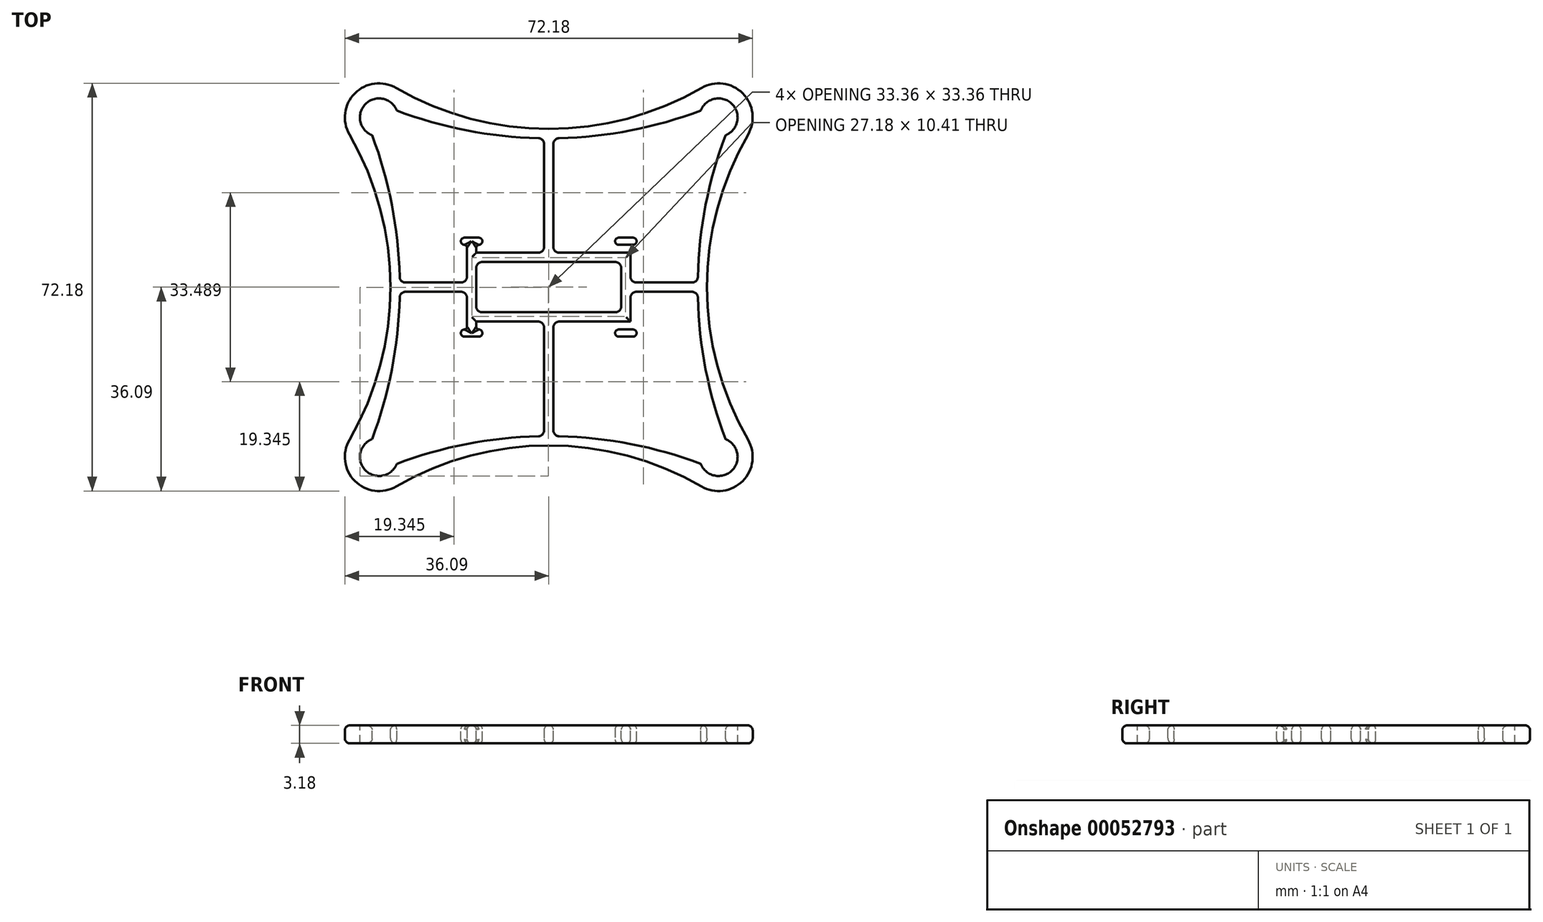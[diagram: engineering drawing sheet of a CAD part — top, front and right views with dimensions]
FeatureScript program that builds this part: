
annotation { "Feature Type Name" : "Feature", "Feature Type Description" : "" }
export const myFeature = defineFeature(function(context is Context, id is Id, definition is map)
    precondition{}
    {
        {
            var Q0;
            Q0=qCreatedBy(makeId("Top.planeOp"),FACE);
            var sketch = newSketch(context, id + "F0", { "sketchPlane" : qUnion([Q0])});
            skCircle(sketch, "E0", {"center": v(-30.05, 30.05) * mm, "radius": 3.38 * mm});
            skCircle(sketch, "E1", {"center": v(30.05, 30.05) * mm, "radius": 3.38 * mm});
            skCircle(sketch, "E2", {"center": v(30.05, -30.05) * mm, "radius": 3.38 * mm});
            skCircle(sketch, "E3", {"center": v(-30.05, -30.05) * mm, "radius": 3.38 * mm});
            skCircle(sketch, "E4", {"center": v(-30.05, 30.05) * mm, "radius": 6.05 * mm});
            skCircle(sketch, "E5", {"center": v(-30.05, -30.05) * mm, "radius": 6.05 * mm});
            skCircle(sketch, "E6", {"center": v(30.05, -30.05) * mm, "radius": 6.05 * mm});
            skCircle(sketch, "E7", {"center": v(30.05, 30.05) * mm, "radius": 6.05 * mm});
            skCircle(sketch, "E8", {"center": v(-102.57, 0) * mm, "radius": 76.2 * mm});
            skCircle(sketch, "E9", {"center": v(-81.9, 0) * mm, "radius": 53.88 * mm});
            skCircle(sketch, "E10", {"center": v(0, 102.57) * mm, "radius": 76.2 * mm});
            skCircle(sketch, "E11", {"center": v(0, 81.9) * mm, "radius": 53.88 * mm});
            skCircle(sketch, "E12", {"center": v(102.57, 0) * mm, "radius": 76.2 * mm});
            skCircle(sketch, "E13", {"center": v(81.9, 0) * mm, "radius": 53.88 * mm});
            skCircle(sketch, "E14", {"center": v(0, -102.57) * mm, "radius": 76.2 * mm});
            skCircle(sketch, "E15", {"center": v(0, -81.9) * mm, "radius": 53.88 * mm});
            skPoint(sketch, "E16.rect.middle", {"position": v(0, 0) * mm});
            skLineSegment(sketch, "E17.rect.bottom", {"start": v(14.48, 6.1) * mm, "end": v(-14.48, 6.1) * mm});
            skLineSegment(sketch, "E17.rect.top", {"start": v(14.48, -6.1) * mm, "end": v(-14.48, -6.1) * mm});
            skLineSegment(sketch, "E17.rect.left", {"start": v(14.48, 6.1) * mm, "end": v(14.48, -6.1) * mm});
            skLineSegment(sketch, "E17.rect.right", {"start": v(-14.48, 6.1) * mm, "end": v(-14.48, -6.1) * mm});
            skLineSegment(sketch, "E18.rect.bottom", {"start": v(12.83, 4.44) * mm, "end": v(-12.83, 4.45) * mm});
            skLineSegment(sketch, "E18.rect.top", {"start": v(12.83, -4.45) * mm, "end": v(-12.83, -4.44) * mm});
            skLineSegment(sketch, "E18.rect.left", {"start": v(12.83, 4.44) * mm, "end": v(12.83, -4.45) * mm});
            skLineSegment(sketch, "E18.rect.right", {"start": v(-12.83, 4.45) * mm, "end": v(-12.83, -4.44) * mm});
            skLineSegment(sketch, "E19.rect.bottom", {"start": v(0.83, 28.02) * mm, "end": v(-0.83, 28.02) * mm});
            skLineSegment(sketch, "E19.rect.top", {"start": v(0.83, -28.02) * mm, "end": v(-0.83, -28.02) * mm});
            skLineSegment(sketch, "E19.rect.left", {"start": v(0.83, 28.02) * mm, "end": v(0.83, -28.02) * mm});
            skLineSegment(sketch, "E19.rect.right", {"start": v(-0.83, 28.02) * mm, "end": v(-0.83, -28.02) * mm});
            skLineSegment(sketch, "E20.rect.bottom", {"start": v(28.02, 0.83) * mm, "end": v(-28.02, 0.83) * mm});
            skLineSegment(sketch, "E20.rect.top", {"start": v(28.02, -0.83) * mm, "end": v(-28.02, -0.83) * mm});
            skLineSegment(sketch, "E20.rect.left", {"start": v(28.02, 0.83) * mm, "end": v(28.02, -0.83) * mm});
            skLineSegment(sketch, "E20.rect.right", {"start": v(-28.02, 0.83) * mm, "end": v(-28.02, -0.83) * mm});
            skLineSegment(sketch, "E21.left", {"start": v(14.48, 6.1) * mm, "end": v(14.48, 6.1) * mm});
            skLineSegment(sketch, "E22.left", {"start": v(14.48, -6.1) * mm, "end": v(14.48, -6.1) * mm});
            skLineSegment(sketch, "E23.bottom", {"start": v(-14.48, 6.1) * mm, "end": v(-12.83, 6.1) * mm});
            skLineSegment(sketch, "E23.top", {"start": v(-14.48, 8.13) * mm, "end": v(-12.83, 8.13) * mm});
            skLineSegment(sketch, "E23.left", {"start": v(-14.48, 6.1) * mm, "end": v(-14.48, 8.13) * mm});
            skLineSegment(sketch, "E23.right", {"start": v(-12.83, 6.1) * mm, "end": v(-12.83, 8.13) * mm});
            skLineSegment(sketch, "E24.bottom", {"start": v(-14.48, -6.1) * mm, "end": v(-12.83, -6.1) * mm});
            skLineSegment(sketch, "E24.top", {"start": v(-14.48, -8.13) * mm, "end": v(-12.83, -8.13) * mm});
            skLineSegment(sketch, "E24.left", {"start": v(-14.48, -6.1) * mm, "end": v(-14.48, -8.13) * mm});
            skLineSegment(sketch, "E24.right", {"start": v(-12.83, -6.1) * mm, "end": v(-12.83, -8.13) * mm});
            skLineSegment(sketch, "E25.bottom", {"start": v(14.48, -6.1) * mm, "end": v(12.83, -6.1) * mm});
            skLineSegment(sketch, "E25.top", {"start": v(14.48, -8.13) * mm, "end": v(12.83, -8.13) * mm});
            skLineSegment(sketch, "E25.left", {"start": v(14.48, -6.1) * mm, "end": v(14.48, -8.13) * mm});
            skLineSegment(sketch, "E25.right", {"start": v(12.83, -6.1) * mm, "end": v(12.83, -8.13) * mm});
            skLineSegment(sketch, "E26.bottom", {"start": v(14.48, 6.1) * mm, "end": v(12.83, 6.1) * mm});
            skLineSegment(sketch, "E26.top", {"start": v(14.48, 8.13) * mm, "end": v(12.83, 8.13) * mm});
            skLineSegment(sketch, "E26.left", {"start": v(14.48, 6.1) * mm, "end": v(14.48, 8.13) * mm});
            skLineSegment(sketch, "E26.right", {"start": v(12.83, 6.1) * mm, "end": v(12.83, 8.13) * mm});
            skLineSegment(sketch, "E27.rect.bottom", {"start": v(-11.75, 8.76) * mm, "end": v(-15.56, 8.76) * mm});
            skLineSegment(sketch, "E27.rect.top", {"start": v(-11.75, 7.5) * mm, "end": v(-15.56, 7.5) * mm});
            skLineSegment(sketch, "E27.rect.left", {"start": v(-11.75, 8.76) * mm, "end": v(-11.75, 7.5) * mm});
            skLineSegment(sketch, "E27.rect.right", {"start": v(-15.56, 8.76) * mm, "end": v(-15.56, 7.5) * mm});
            skPoint(sketch, "E27.rect.middle", {"position": v(-13.65, 8.13) * mm});
            skLineSegment(sketch, "E28.rect.bottom", {"start": v(11.75, 8.76) * mm, "end": v(15.56, 8.76) * mm});
            skLineSegment(sketch, "E28.rect.top", {"start": v(11.75, 7.5) * mm, "end": v(15.56, 7.5) * mm});
            skLineSegment(sketch, "E28.rect.left", {"start": v(11.75, 8.76) * mm, "end": v(11.75, 7.5) * mm});
            skLineSegment(sketch, "E28.rect.right", {"start": v(15.56, 8.76) * mm, "end": v(15.56, 7.5) * mm});
            skPoint(sketch, "E28.rect.middle", {"position": v(13.65, 8.13) * mm});
            skLineSegment(sketch, "E29.rect.bottom", {"start": v(11.75, -7.5) * mm, "end": v(15.56, -7.5) * mm});
            skLineSegment(sketch, "E29.rect.top", {"start": v(11.75, -8.76) * mm, "end": v(15.56, -8.76) * mm});
            skLineSegment(sketch, "E29.rect.left", {"start": v(11.75, -7.5) * mm, "end": v(11.75, -8.76) * mm});
            skLineSegment(sketch, "E29.rect.right", {"start": v(15.56, -7.5) * mm, "end": v(15.56, -8.76) * mm});
            skPoint(sketch, "E29.rect.middle", {"position": v(13.65, -8.13) * mm});
            skLineSegment(sketch, "E30.rect.bottom", {"start": v(-11.75, -8.76) * mm, "end": v(-15.56, -8.76) * mm});
            skLineSegment(sketch, "E30.rect.top", {"start": v(-11.75, -7.5) * mm, "end": v(-15.56, -7.5) * mm});
            skLineSegment(sketch, "E30.rect.left", {"start": v(-11.75, -8.76) * mm, "end": v(-11.75, -7.5) * mm});
            skLineSegment(sketch, "E30.rect.right", {"start": v(-15.56, -8.76) * mm, "end": v(-15.56, -7.5) * mm});
            skPoint(sketch, "E30.rect.middle", {"position": v(-13.65, -8.13) * mm});
            skSolve(sketch);
        }
        {
            var Q0;
            {var subQ3=sQuery(id+"F0.wireOp",EDGE,"E4");var subQ5=sQuery(id+"F0.wireOp",EDGE,"E9");var subQ7=makeQuery(id+"F0.imprint","INTERSECT",VERTEX,{"derivedFrom":[subQ3,subQ5]});Q0=makeQuery(id+"F0.imprint","IMPRINT",FACE,{"disambiguationData":[TD([[makeQuery(id+"F0.imprint","IMPRINT",EDGE,{"disambiguationData":[TD([[subQ7,-1.0]])],"derivedFrom":subQ3}),-1.0]])]});}
            var Q1;
            {var subQ0=sQuery(id+"F0.wireOp",EDGE,"E8");var subQ1=sQuery(id+"F0.wireOp",EDGE,"E0");var subQ2=makeQuery(id+"F0.imprint","INTERSECT",VERTEX,{"disambiguationData":[OD(0.0)],"derivedFrom":[subQ1,subQ0]});Q1=makeQuery(id+"F0.imprint","IMPRINT",FACE,{"disambiguationData":[TD([[makeQuery(id+"F0.imprint","IMPRINT",EDGE,{"disambiguationData":[TD([[subQ2,-1.0]])],"derivedFrom":subQ1}),-1.0]])]});}
            var Q2;
            {var subQ0=sQuery(id+"F0.wireOp",EDGE,"E10");var subQ1=sQuery(id+"F0.wireOp",EDGE,"E0");var subQ2=makeQuery(id+"F0.imprint","INTERSECT",VERTEX,{"disambiguationData":[OD(0.0)],"derivedFrom":[subQ1,subQ0]});Q2=makeQuery(id+"F0.imprint","IMPRINT",FACE,{"disambiguationData":[TD([[makeQuery(id+"F0.imprint","IMPRINT",EDGE,{"disambiguationData":[TD([[subQ2,-1.0]])],"derivedFrom":subQ1}),-1.0]])]});}
            var Q3;
            {var subQ0=sQuery(id+"F0.wireOp",EDGE,"E0");var subQ1=sQuery(id+"F0.wireOp",EDGE,"E10");var subQ3=makeQuery(id+"F0.imprint","INTERSECT",VERTEX,{"disambiguationData":[OD(0.0)],"derivedFrom":[subQ0,subQ1]});Q3=makeQuery(id+"F0.imprint","IMPRINT",FACE,{"disambiguationData":[TD([[makeQuery(id+"F0.imprint","IMPRINT",EDGE,{"disambiguationData":[TD([[subQ3,1.0]])],"derivedFrom":subQ0}),-1.0]])]});}
            var Q4;
            {var subQ0=sQuery(id+"F0.wireOp",EDGE,"E11");var subQ3=sQuery(id+"F0.wireOp",EDGE,"E4");var subQ4=makeQuery(id+"F0.imprint","INTERSECT",VERTEX,{"derivedFrom":[subQ3,subQ0]});Q4=makeQuery(id+"F0.imprint","IMPRINT",FACE,{"disambiguationData":[TD([[makeQuery(id+"F0.imprint","IMPRINT",EDGE,{"disambiguationData":[TD([[subQ4,1.0]])],"derivedFrom":subQ3}),-1.0]])]});}
            var Q5;
            {var subQ0=sQuery(id+"F0.wireOp",EDGE,"E10");var subQ1=sQuery(id+"F0.wireOp",EDGE,"E1");var subQ5=makeQuery(id+"F0.imprint","INTERSECT",VERTEX,{"disambiguationData":[OD(0.0)],"derivedFrom":[subQ1,subQ0]});Q5=makeQuery(id+"F0.imprint","IMPRINT",FACE,{"disambiguationData":[TD([[makeQuery(id+"F0.imprint","IMPRINT",EDGE,{"disambiguationData":[TD([[subQ5,1.0]])],"derivedFrom":subQ1}),-1.0]])]});}
            var Q6;
            {var subQ1=sQuery(id+"F0.wireOp",EDGE,"E1");var subQ5=sQuery(id+"F0.wireOp",EDGE,"E10");var subQ6=makeQuery(id+"F0.imprint","INTERSECT",VERTEX,{"disambiguationData":[OD(1.0)],"derivedFrom":[subQ1,subQ5]});Q6=makeQuery(id+"F0.imprint","IMPRINT",FACE,{"disambiguationData":[TD([[makeQuery(id+"F0.imprint","IMPRINT",EDGE,{"disambiguationData":[TD([[subQ6,1.0]])],"derivedFrom":subQ1}),-1.0]])]});}
            var Q7;
            {var subQ0=sQuery(id+"F0.wireOp",EDGE,"E12");var subQ3=sQuery(id+"F0.wireOp",EDGE,"E1");var subQ4=makeQuery(id+"F0.imprint","INTERSECT",VERTEX,{"disambiguationData":[OD(0.0)],"derivedFrom":[subQ3,subQ0]});Q7=makeQuery(id+"F0.imprint","IMPRINT",FACE,{"disambiguationData":[TD([[makeQuery(id+"F0.imprint","IMPRINT",EDGE,{"disambiguationData":[TD([[subQ4,-1.0]])],"derivedFrom":subQ3}),-1.0]])]});}
            var Q8;
            {var subQ0=sQuery(id+"F0.wireOp",EDGE,"E12");var subQ1=sQuery(id+"F0.wireOp",EDGE,"E2");var subQ5=makeQuery(id+"F0.imprint","INTERSECT",VERTEX,{"disambiguationData":[OD(0.0)],"derivedFrom":[subQ1,subQ0]});Q8=makeQuery(id+"F0.imprint","IMPRINT",FACE,{"disambiguationData":[TD([[makeQuery(id+"F0.imprint","IMPRINT",EDGE,{"disambiguationData":[TD([[subQ5,1.0]])],"derivedFrom":subQ1}),-1.0]])]});}
            var Q9;
            {var subQ0=sQuery(id+"F0.wireOp",EDGE,"E12");var subQ1=sQuery(id+"F0.wireOp",EDGE,"E2");var subQ2=makeQuery(id+"F0.imprint","INTERSECT",VERTEX,{"disambiguationData":[OD(1.0)],"derivedFrom":[subQ1,subQ0]});Q9=makeQuery(id+"F0.imprint","IMPRINT",FACE,{"disambiguationData":[TD([[makeQuery(id+"F0.imprint","IMPRINT",EDGE,{"disambiguationData":[TD([[subQ2,1.0]])],"derivedFrom":subQ1}),-1.0]])]});}
            var Q10;
            {var subQ0=sQuery(id+"F0.wireOp",EDGE,"E14");var subQ3=sQuery(id+"F0.wireOp",EDGE,"E2");var subQ4=makeQuery(id+"F0.imprint","INTERSECT",VERTEX,{"disambiguationData":[OD(0.0)],"derivedFrom":[subQ3,subQ0]});Q10=makeQuery(id+"F0.imprint","IMPRINT",FACE,{"disambiguationData":[TD([[makeQuery(id+"F0.imprint","IMPRINT",EDGE,{"disambiguationData":[TD([[subQ4,-1.0]])],"derivedFrom":subQ3}),-1.0]])]});}
            var Q11;
            {var subQ0=sQuery(id+"F0.wireOp",EDGE,"E3");var subQ1=sQuery(id+"F0.wireOp",EDGE,"E14");var subQ3=makeQuery(id+"F0.imprint","INTERSECT",VERTEX,{"disambiguationData":[OD(0.0)],"derivedFrom":[subQ0,subQ1]});Q11=makeQuery(id+"F0.imprint","IMPRINT",FACE,{"disambiguationData":[TD([[makeQuery(id+"F0.imprint","IMPRINT",EDGE,{"disambiguationData":[TD([[subQ3,-1.0]])],"derivedFrom":subQ0}),-1.0]])]});}
            var Q12;
            {var subQ1=sQuery(id+"F0.wireOp",EDGE,"E3");var subQ5=sQuery(id+"F0.wireOp",EDGE,"E8");var subQ7=makeQuery(id+"F0.imprint","INTERSECT",VERTEX,{"disambiguationData":[OD(0.0)],"derivedFrom":[subQ1,subQ5]});Q12=makeQuery(id+"F0.imprint","IMPRINT",FACE,{"disambiguationData":[TD([[makeQuery(id+"F0.imprint","IMPRINT",EDGE,{"disambiguationData":[TD([[subQ7,-1.0]])],"derivedFrom":subQ1}),-1.0]])]});}
            var Q13;
            {var subQ0=sQuery(id+"F0.wireOp",EDGE,"E8");var subQ3=sQuery(id+"F0.wireOp",EDGE,"E3");var subQ5=makeQuery(id+"F0.imprint","INTERSECT",VERTEX,{"disambiguationData":[OD(0.0)],"derivedFrom":[subQ3,subQ0]});Q13=makeQuery(id+"F0.imprint","IMPRINT",FACE,{"disambiguationData":[TD([[makeQuery(id+"F0.imprint","IMPRINT",EDGE,{"disambiguationData":[TD([[subQ5,1.0]])],"derivedFrom":subQ3}),-1.0]])]});}
            var Q14;
            {var subQ0=sQuery(id+"F0.wireOp",EDGE,"E12");var subQ3=sQuery(id+"F0.wireOp",EDGE,"E1");var subQ6=makeQuery(id+"F0.imprint","INTERSECT",VERTEX,{"disambiguationData":[OD(0.0)],"derivedFrom":[subQ3,subQ0]});Q14=makeQuery(id+"F0.imprint","IMPRINT",FACE,{"disambiguationData":[TD([[makeQuery(id+"F0.imprint","IMPRINT",EDGE,{"disambiguationData":[TD([[subQ6,1.0]])],"derivedFrom":subQ3}),-1.0]])]});}
            var Q15;
            {var subQ3=sQuery(id+"F0.wireOp",EDGE,"E6");var subQ5=sQuery(id+"F0.wireOp",EDGE,"E12");var subQ7=makeQuery(id+"F0.imprint","INTERSECT",VERTEX,{"disambiguationData":[OD(0.0)],"derivedFrom":[subQ3,subQ5]});Q15=makeQuery(id+"F0.imprint","IMPRINT",FACE,{"disambiguationData":[TD([[makeQuery(id+"F0.imprint","IMPRINT",EDGE,{"disambiguationData":[TD([[subQ7,1.0]])],"derivedFrom":subQ3}),-1.0]])]});}
            var Q16;
            {var subQ0=sQuery(id+"F0.wireOp",EDGE,"97792d4c-2e40-4aaa-a942-c1651c489ece.rect.left");var subQ6=sQuery(id+"F0.wireOp",EDGE,"E17.rect.bottom");var subQ7=makeQuery(id+"F0.imprint","INTERSECT",VERTEX,{"derivedFrom":[subQ0,subQ6]});Q16=makeQuery(id+"F0.imprint","IMPRINT",FACE,{"disambiguationData":[TD([[makeQuery(id+"F0.imprint","IMPRINT",EDGE,{"disambiguationData":[TD([[subQ7,-1.0]])],"derivedFrom":subQ6}),-1.0]])]});}
            var Q17;
            {var subQ3=sQuery(id+"F0.wireOp",EDGE,"E16.rect.bottom");var subQ9=sQuery(id+"F0.wireOp",EDGE,"E18.rect.right");var subQ11=makeQuery(id+"F0.imprint","INTERSECT",VERTEX,{"derivedFrom":[subQ3,subQ9]});Q17=makeQuery(id+"F0.imprint","IMPRINT",FACE,{"disambiguationData":[TD([[makeQuery(id+"F0.imprint","IMPRINT",EDGE,{"disambiguationData":[TD([[subQ11,-1.0]])],"derivedFrom":subQ3}),-1.0]])]});}
            var Q18;
            {var subQ0=sQuery(id+"F0.wireOp",EDGE,"E17.rect.bottom");var subQ1=sQuery(id+"F0.wireOp",EDGE,"97792d4c-2e40-4aaa-a942-c1651c489ece.rect.left");var subQ2=makeQuery(id+"F0.imprint","INTERSECT",VERTEX,{"derivedFrom":[subQ1,subQ0]});Q18=makeQuery(id+"F0.imprint","IMPRINT",FACE,{"disambiguationData":[TD([[makeQuery(id+"F0.imprint","IMPRINT",EDGE,{"disambiguationData":[TD([[subQ2,-1.0]])],"derivedFrom":subQ1}),-1.0]])]});}
            var Q19;
            {var subQ0=sQuery(id+"F0.wireOp",EDGE,"E17.rect.left");var subQ3=sQuery(id+"F0.wireOp",EDGE,"E16.rect.bottom");var subQ4=makeQuery(id+"F0.imprint","INTERSECT",VERTEX,{"derivedFrom":[subQ3,subQ0]});Q19=makeQuery(id+"F0.imprint","IMPRINT",FACE,{"disambiguationData":[TD([[makeQuery(id+"F0.imprint","IMPRINT",EDGE,{"disambiguationData":[TD([[subQ4,-1.0]])],"derivedFrom":subQ3}),-1.0]])]});}
            var Q20;
            {var subQ0=sQuery(id+"F0.wireOp",EDGE,"E17.rect.left");var subQ1=sQuery(id+"F0.wireOp",EDGE,"E16.rect.bottom");var subQ2=makeQuery(id+"F0.imprint","INTERSECT",VERTEX,{"derivedFrom":[subQ1,subQ0]});Q20=makeQuery(id+"F0.imprint","IMPRINT",FACE,{"disambiguationData":[TD([[makeQuery(id+"F0.imprint","IMPRINT",EDGE,{"disambiguationData":[TD([[subQ2,-1.0]])],"derivedFrom":subQ1}),1.0]])]});}
            var Q21;
            {var subQ0=sQuery(id+"F0.wireOp",EDGE,"E17.rect.left");var subQ3=sQuery(id+"F0.wireOp",EDGE,"E16.rect.top");var subQ4=makeQuery(id+"F0.imprint","INTERSECT",VERTEX,{"derivedFrom":[subQ3,subQ0]});Q21=makeQuery(id+"F0.imprint","IMPRINT",FACE,{"disambiguationData":[TD([[makeQuery(id+"F0.imprint","IMPRINT",EDGE,{"disambiguationData":[TD([[subQ4,-1.0]])],"derivedFrom":subQ3}),1.0]])]});}
            var Q22;
            {var subQ0=sQuery(id+"F0.wireOp",EDGE,"E18.rect.top");var subQ1=sQuery(id+"F0.wireOp",EDGE,"97792d4c-2e40-4aaa-a942-c1651c489ece.rect.left");var subQ2=makeQuery(id+"F0.imprint","INTERSECT",VERTEX,{"derivedFrom":[subQ1,subQ0]});Q22=makeQuery(id+"F0.imprint","IMPRINT",FACE,{"disambiguationData":[TD([[makeQuery(id+"F0.imprint","IMPRINT",EDGE,{"disambiguationData":[TD([[subQ2,-1.0]])],"derivedFrom":subQ1}),-1.0]])]});}
            var Q23;
            {var subQ5=sQuery(id+"F0.wireOp",EDGE,"E16.rect.top");var subQ9=sQuery(id+"F0.wireOp",EDGE,"E18.rect.right");var subQ11=makeQuery(id+"F0.imprint","INTERSECT",VERTEX,{"derivedFrom":[subQ5,subQ9]});Q23=makeQuery(id+"F0.imprint","IMPRINT",FACE,{"disambiguationData":[TD([[makeQuery(id+"F0.imprint","IMPRINT",EDGE,{"disambiguationData":[TD([[subQ11,-1.0]])],"derivedFrom":subQ5}),1.0]])]});}
            var Q24;
            {var subQ0=sQuery(id+"F0.wireOp",EDGE,"E18.rect.right");var subQ1=sQuery(id+"F0.wireOp",EDGE,"E16.rect.bottom");var subQ2=makeQuery(id+"F0.imprint","INTERSECT",VERTEX,{"derivedFrom":[subQ1,subQ0]});Q24=makeQuery(id+"F0.imprint","IMPRINT",FACE,{"disambiguationData":[TD([[makeQuery(id+"F0.imprint","IMPRINT",EDGE,{"disambiguationData":[TD([[subQ2,-1.0]])],"derivedFrom":subQ1}),1.0]])]});}
            var Q25;
            {var subQ1=sQuery(id+"F0.wireOp",EDGE,"E16.rect.bottom");var subQ6=sQuery(id+"F0.wireOp",EDGE,"E17.rect.right");var subQ7=makeQuery(id+"F0.imprint","INTERSECT",VERTEX,{"derivedFrom":[subQ1,subQ6]});Q25=makeQuery(id+"F0.imprint","IMPRINT",FACE,{"disambiguationData":[TD([[makeQuery(id+"F0.imprint","IMPRINT",EDGE,{"disambiguationData":[TD([[subQ7,-1.0]])],"derivedFrom":subQ6}),-1.0]])]});}
            var Q26;
            {var subQ1=sQuery(id+"F0.wireOp",EDGE,"E16.rect.bottom");var subQ6=sQuery(id+"F0.wireOp",EDGE,"E17.rect.left");var subQ7=makeQuery(id+"F0.imprint","INTERSECT",VERTEX,{"derivedFrom":[subQ1,subQ6]});Q26=makeQuery(id+"F0.imprint","IMPRINT",FACE,{"disambiguationData":[TD([[makeQuery(id+"F0.imprint","IMPRINT",EDGE,{"disambiguationData":[TD([[subQ7,-1.0]])],"derivedFrom":subQ6}),1.0]])]});}
            var Q27;
            {var subQ0=sQuery(id+"F0.wireOp",EDGE,"97792d4c-2e40-4aaa-a942-c1651c489ece.rect.left");var subQ6=sQuery(id+"F0.wireOp",EDGE,"E17.rect.top");var subQ7=makeQuery(id+"F0.imprint","INTERSECT",VERTEX,{"derivedFrom":[subQ0,subQ6]});Q27=makeQuery(id+"F0.imprint","IMPRINT",FACE,{"disambiguationData":[TD([[makeQuery(id+"F0.imprint","IMPRINT",EDGE,{"disambiguationData":[TD([[subQ7,-1.0]])],"derivedFrom":subQ6}),1.0]])]});}
            var Q28;
            Q28=makeQuery(id+"F0.imprint","IMPRINT",FACE,{"disambiguationData":[TD([[makeQuery(id+"F0.imprint","IMPRINT",EDGE,{"derivedFrom":sQuery(id+"F0.wireOp",EDGE,"de616939-67df-4de1-98a8-b123298b16c6.bottom")}),-1.0]])]});
            var Q29;
            Q29=makeQuery(id+"F0.imprint","IMPRINT",FACE,{"disambiguationData":[TD([[makeQuery(id+"F0.imprint","IMPRINT",EDGE,{"derivedFrom":sQuery(id+"F0.wireOp",EDGE,"6e18662c-c205-4df8-b961-8c52012f615d.bottom")}),1.0]])]});
            var Q30;
            Q30=makeQuery(id+"F0.imprint","IMPRINT",FACE,{"disambiguationData":[TD([[makeQuery(id+"F0.imprint","IMPRINT",EDGE,{"derivedFrom":sQuery(id+"F0.wireOp",EDGE,"e5e8593a-10a3-4d83-983c-bc6820abb37f.bottom")}),-1.0]])]});
            var Q31;
            Q31=makeQuery(id+"F0.imprint","IMPRINT",FACE,{"disambiguationData":[TD([[makeQuery(id+"F0.imprint","IMPRINT",EDGE,{"derivedFrom":sQuery(id+"F0.wireOp",EDGE,"fe4e9a62-022c-4ccf-87c7-29a0906fb106.bottom")}),1.0]])]});
            var Q32;
            {var subQ0=sQuery(id+"F0.wireOp",EDGE,"E20.rect.bottom");var subQ1=sQuery(id+"F0.wireOp",EDGE,"E8");var subQ2=makeQuery(id+"F0.imprint","INTERSECT",VERTEX,{"derivedFrom":[subQ1,subQ0]});Q32=makeQuery(id+"F0.imprint","IMPRINT",FACE,{"disambiguationData":[TD([[makeQuery(id+"F0.imprint","IMPRINT",EDGE,{"disambiguationData":[TD([[subQ2,1.0]])],"derivedFrom":subQ1}),1.0]])]});}
            var Q33;
            {var subQ0=sQuery(id+"F0.wireOp",EDGE,"E8");var subQ1=sQuery(id+"F0.wireOp",EDGE,"E5");var subQ2=makeQuery(id+"F0.imprint","INTERSECT",VERTEX,{"disambiguationData":[OD(0.0)],"derivedFrom":[subQ1,subQ0]});Q33=makeQuery(id+"F0.imprint","IMPRINT",FACE,{"disambiguationData":[TD([[makeQuery(id+"F0.imprint","IMPRINT",EDGE,{"disambiguationData":[TD([[subQ2,-1.0]])],"derivedFrom":subQ1}),-1.0]])]});}
            var Q34;
            {var subQ0=sQuery(id+"F0.wireOp",EDGE,"E19.rect.left");var subQ1=sQuery(id+"F0.wireOp",EDGE,"E14");var subQ2=makeQuery(id+"F0.imprint","INTERSECT",VERTEX,{"derivedFrom":[subQ1,subQ0]});Q34=makeQuery(id+"F0.imprint","IMPRINT",FACE,{"disambiguationData":[TD([[makeQuery(id+"F0.imprint","IMPRINT",EDGE,{"disambiguationData":[TD([[subQ2,-1.0]])],"derivedFrom":subQ1}),1.0]])]});}
            var Q35;
            {var subQ0=sQuery(id+"F0.wireOp",EDGE,"E14");var subQ1=sQuery(id+"F0.wireOp",EDGE,"E6");var subQ2=makeQuery(id+"F0.imprint","INTERSECT",VERTEX,{"disambiguationData":[OD(0.0)],"derivedFrom":[subQ1,subQ0]});Q35=makeQuery(id+"F0.imprint","IMPRINT",FACE,{"disambiguationData":[TD([[makeQuery(id+"F0.imprint","IMPRINT",EDGE,{"disambiguationData":[TD([[subQ2,-1.0]])],"derivedFrom":subQ1}),-1.0]])]});}
            var Q36;
            {var subQ0=sQuery(id+"F0.wireOp",EDGE,"E20.rect.bottom");var subQ1=sQuery(id+"F0.wireOp",EDGE,"E12");var subQ2=makeQuery(id+"F0.imprint","INTERSECT",VERTEX,{"derivedFrom":[subQ1,subQ0]});Q36=makeQuery(id+"F0.imprint","IMPRINT",FACE,{"disambiguationData":[TD([[makeQuery(id+"F0.imprint","IMPRINT",EDGE,{"disambiguationData":[TD([[subQ2,-1.0]])],"derivedFrom":subQ1}),1.0]])]});}
            var Q37;
            {var subQ7=sQuery(id+"F0.wireOp",EDGE,"E17.rect.left");var subQ8=sQuery(id+"F0.wireOp",EDGE,"E17.rect.top");var subQ9=makeQuery(id+"F0.imprint","INTERSECT",VERTEX,{"derivedFrom":[subQ8,subQ7]});Q37=makeQuery(id+"F0.imprint","IMPRINT",FACE,{"disambiguationData":[TD([[makeQuery(id+"F0.imprint","IMPRINT",EDGE,{"disambiguationData":[TD([[subQ9,-1.0]])],"derivedFrom":subQ8}),-1.0]])]});}
            var Q38;
            {var subQ0=sQuery(id+"F0.wireOp",EDGE,"E19.rect.left");var subQ1=sQuery(id+"F0.wireOp",EDGE,"E17.rect.top");var subQ2=makeQuery(id+"F0.imprint","INTERSECT",VERTEX,{"derivedFrom":[subQ1,subQ0]});Q38=makeQuery(id+"F0.imprint","IMPRINT",FACE,{"disambiguationData":[TD([[makeQuery(id+"F0.imprint","IMPRINT",EDGE,{"disambiguationData":[TD([[subQ2,-1.0]])],"derivedFrom":subQ1}),-1.0]])]});}
            var Q39;
            {var subQ5=sQuery(id+"F0.wireOp",EDGE,"E17.rect.top");var subQ7=sQuery(id+"F0.wireOp",EDGE,"E17.rect.right");var subQ8=makeQuery(id+"F0.imprint","INTERSECT",VERTEX,{"derivedFrom":[subQ5,subQ7]});Q39=makeQuery(id+"F0.imprint","IMPRINT",FACE,{"disambiguationData":[TD([[makeQuery(id+"F0.imprint","IMPRINT",EDGE,{"disambiguationData":[TD([[subQ8,1.0]])],"derivedFrom":subQ5}),-1.0]])]});}
            var Q40;
            {var subQ0=sQuery(id+"F0.wireOp",EDGE,"E20.rect.bottom");var subQ1=sQuery(id+"F0.wireOp",EDGE,"E17.rect.right");var subQ2=makeQuery(id+"F0.imprint","INTERSECT",VERTEX,{"derivedFrom":[subQ1,subQ0]});Q40=makeQuery(id+"F0.imprint","IMPRINT",FACE,{"disambiguationData":[TD([[makeQuery(id+"F0.imprint","IMPRINT",EDGE,{"disambiguationData":[TD([[subQ2,-1.0]])],"derivedFrom":subQ1}),1.0]])]});}
            var Q41;
            {var subQ7=sQuery(id+"F0.wireOp",EDGE,"E17.rect.right");var subQ8=sQuery(id+"F0.wireOp",EDGE,"E17.rect.bottom");var subQ9=makeQuery(id+"F0.imprint","INTERSECT",VERTEX,{"derivedFrom":[subQ8,subQ7]});Q41=makeQuery(id+"F0.imprint","IMPRINT",FACE,{"disambiguationData":[TD([[makeQuery(id+"F0.imprint","IMPRINT",EDGE,{"disambiguationData":[TD([[subQ9,1.0]])],"derivedFrom":subQ8}),1.0]])]});}
            var Q42;
            {var subQ7=sQuery(id+"F0.wireOp",EDGE,"E17.rect.left");var subQ8=sQuery(id+"F0.wireOp",EDGE,"E17.rect.bottom");var subQ9=makeQuery(id+"F0.imprint","INTERSECT",VERTEX,{"derivedFrom":[subQ8,subQ7]});Q42=makeQuery(id+"F0.imprint","IMPRINT",FACE,{"disambiguationData":[TD([[makeQuery(id+"F0.imprint","IMPRINT",EDGE,{"disambiguationData":[TD([[subQ9,-1.0]])],"derivedFrom":subQ8}),1.0]])]});}
            var Q43;
            {var subQ0=sQuery(id+"F0.wireOp",EDGE,"E20.rect.bottom");var subQ1=sQuery(id+"F0.wireOp",EDGE,"E17.rect.left");var subQ2=makeQuery(id+"F0.imprint","INTERSECT",VERTEX,{"derivedFrom":[subQ1,subQ0]});Q43=makeQuery(id+"F0.imprint","IMPRINT",FACE,{"disambiguationData":[TD([[makeQuery(id+"F0.imprint","IMPRINT",EDGE,{"disambiguationData":[TD([[subQ2,-1.0]])],"derivedFrom":subQ1}),-1.0]])]});}
            var Q44;
            {var subQ0=sQuery(id+"F0.wireOp",EDGE,"E12");var subQ1=sQuery(id+"F0.wireOp",EDGE,"E7");var subQ2=makeQuery(id+"F0.imprint","INTERSECT",VERTEX,{"disambiguationData":[OD(1.0)],"derivedFrom":[subQ1,subQ0]});Q44=makeQuery(id+"F0.imprint","IMPRINT",FACE,{"disambiguationData":[TD([[makeQuery(id+"F0.imprint","IMPRINT",EDGE,{"disambiguationData":[TD([[subQ2,-1.0]])],"derivedFrom":subQ1}),-1.0]])]});}
            var Q45;
            {var subQ0=sQuery(id+"F0.wireOp",EDGE,"E19.rect.left");var subQ1=sQuery(id+"F0.wireOp",EDGE,"E17.rect.bottom");var subQ2=makeQuery(id+"F0.imprint","INTERSECT",VERTEX,{"derivedFrom":[subQ1,subQ0]});Q45=makeQuery(id+"F0.imprint","IMPRINT",FACE,{"disambiguationData":[TD([[makeQuery(id+"F0.imprint","IMPRINT",EDGE,{"disambiguationData":[TD([[subQ2,-1.0]])],"derivedFrom":subQ1}),1.0]])]});}
            var Q46;
            {var subQ0=sQuery(id+"F0.wireOp",EDGE,"E19.rect.right");var subQ1=sQuery(id+"F0.wireOp",EDGE,"E10");var subQ2=makeQuery(id+"F0.imprint","INTERSECT",VERTEX,{"derivedFrom":[subQ1,subQ0]});Q46=makeQuery(id+"F0.imprint","IMPRINT",FACE,{"disambiguationData":[TD([[makeQuery(id+"F0.imprint","IMPRINT",EDGE,{"disambiguationData":[TD([[subQ2,-1.0]])],"derivedFrom":subQ1}),1.0]])]});}
            var Q47;
            {var subQ0=sQuery(id+"F0.wireOp",EDGE,"E11");var subQ1=sQuery(id+"F0.wireOp",EDGE,"E7");var subQ2=makeQuery(id+"F0.imprint","INTERSECT",VERTEX,{"derivedFrom":[subQ1,subQ0]});Q47=makeQuery(id+"F0.imprint","IMPRINT",FACE,{"disambiguationData":[TD([[makeQuery(id+"F0.imprint","IMPRINT",EDGE,{"disambiguationData":[TD([[subQ2,-1.0]])],"derivedFrom":subQ1}),-1.0]])]});}
            var Q48;
            {var subQ7=sQuery(id+"F0.wireOp",EDGE,"f8660cd2-9a3a-46cf-8541-a55b21bbf2a2.left");Q48=makeQuery(id+"F0.imprint","IMPRINT",FACE,{"disambiguationData":[TD([[makeQuery(id+"F0.imprint","IMPRINT",EDGE,{"derivedFrom":subQ7}),1.0]])]});}
            var Q49;
            Q49=makeQuery(id+"F0.imprint","IMPRINT",FACE,{"disambiguationData":[TD([[makeQuery(id+"F0.imprint","IMPRINT",EDGE,{"derivedFrom":sQuery(id+"F0.wireOp",EDGE,"f8660cd2-9a3a-46cf-8541-a55b21bbf2a2.bottom")}),1.0]])]});
            var Q50;
            Q50=makeQuery(id+"F0.imprint","IMPRINT",FACE,{"disambiguationData":[TD([[makeQuery(id+"F0.imprint","IMPRINT",EDGE,{"derivedFrom":sQuery(id+"F0.wireOp",EDGE,"2a5b0057-8150-4ec5-9247-2ce1087ea529.bottom")}),-1.0]])]});
            var Q51;
            {var subQ7=sQuery(id+"F0.wireOp",EDGE,"2a5b0057-8150-4ec5-9247-2ce1087ea529.left");Q51=makeQuery(id+"F0.imprint","IMPRINT",FACE,{"disambiguationData":[TD([[makeQuery(id+"F0.imprint","IMPRINT",EDGE,{"derivedFrom":subQ7}),-1.0]])]});}
            var Q52;
            {var subQ7=sQuery(id+"F0.wireOp",EDGE,"E22.left");Q52=makeQuery(id+"F0.imprint","IMPRINT",FACE,{"disambiguationData":[TD([[makeQuery(id+"F0.imprint","IMPRINT",EDGE,{"derivedFrom":subQ7}),1.0]])]});}
            var Q53;
            Q53=makeQuery(id+"F0.imprint","IMPRINT",FACE,{"disambiguationData":[TD([[makeQuery(id+"F0.imprint","IMPRINT",EDGE,{"derivedFrom":sQuery(id+"F0.wireOp",EDGE,"E22.bottom")}),1.0]])]});
            var Q54;
            {var subQ7=sQuery(id+"F0.wireOp",EDGE,"E21.left");Q54=makeQuery(id+"F0.imprint","IMPRINT",FACE,{"disambiguationData":[TD([[makeQuery(id+"F0.imprint","IMPRINT",EDGE,{"derivedFrom":subQ7}),-1.0]])]});}
            var Q55;
            Q55=makeQuery(id+"F0.imprint","IMPRINT",FACE,{"disambiguationData":[TD([[makeQuery(id+"F0.imprint","IMPRINT",EDGE,{"derivedFrom":sQuery(id+"F0.wireOp",EDGE,"920944db-2e94-47ff-9106-445efe642f17.bottom")}),-1.0]])]});
            var Q56;
            {var subQ7=sQuery(id+"F0.wireOp",EDGE,"E23.bottom");Q56=makeQuery(id+"F0.imprint","IMPRINT",FACE,{"disambiguationData":[TD([[makeQuery(id+"F0.imprint","IMPRINT",EDGE,{"derivedFrom":subQ7}),-1.0]])]});}
            var Q57;
            Q57=makeQuery(id+"F0.imprint","IMPRINT",FACE,{"disambiguationData":[TD([[makeQuery(id+"F0.imprint","IMPRINT",EDGE,{"derivedFrom":sQuery(id+"F0.wireOp",EDGE,"E23.bottom")}),1.0]])]});
            var Q58;
            Q58=makeQuery(id+"F0.imprint","IMPRINT",FACE,{"disambiguationData":[TD([[makeQuery(id+"F0.imprint","IMPRINT",EDGE,{"derivedFrom":sQuery(id+"F0.wireOp",EDGE,"E26.bottom")}),-1.0]])]});
            var Q59;
            {var subQ7=sQuery(id+"F0.wireOp",EDGE,"E26.bottom");Q59=makeQuery(id+"F0.imprint","IMPRINT",FACE,{"disambiguationData":[TD([[makeQuery(id+"F0.imprint","IMPRINT",EDGE,{"derivedFrom":subQ7}),1.0]])]});}
            var Q60;
            {var subQ7=sQuery(id+"F0.wireOp",EDGE,"E25.bottom");Q60=makeQuery(id+"F0.imprint","IMPRINT",FACE,{"disambiguationData":[TD([[makeQuery(id+"F0.imprint","IMPRINT",EDGE,{"derivedFrom":subQ7}),-1.0]])]});}
            var Q61;
            Q61=makeQuery(id+"F0.imprint","IMPRINT",FACE,{"disambiguationData":[TD([[makeQuery(id+"F0.imprint","IMPRINT",EDGE,{"derivedFrom":sQuery(id+"F0.wireOp",EDGE,"E25.bottom")}),1.0]])]});
            var Q62;
            {var subQ7=sQuery(id+"F0.wireOp",EDGE,"E24.bottom");Q62=makeQuery(id+"F0.imprint","IMPRINT",FACE,{"disambiguationData":[TD([[makeQuery(id+"F0.imprint","IMPRINT",EDGE,{"derivedFrom":subQ7}),1.0]])]});}
            var Q63;
            Q63=makeQuery(id+"F0.imprint","IMPRINT",FACE,{"disambiguationData":[TD([[makeQuery(id+"F0.imprint","IMPRINT",EDGE,{"derivedFrom":sQuery(id+"F0.wireOp",EDGE,"E24.bottom")}),-1.0]])]});
            var Q64;
            {var subQ1=sQuery(id+"F0.wireOp",EDGE,"E26.top");Q64=makeQuery(id+"F0.imprint","IMPRINT",FACE,{"disambiguationData":[TD([[makeQuery(id+"F0.imprint","IMPRINT",EDGE,{"derivedFrom":subQ1}),-1.0]])]});}
            var Q65;
            {var subQ0=sQuery(id+"F0.wireOp",EDGE,"E26.top");Q65=makeQuery(id+"F0.imprint","IMPRINT",FACE,{"disambiguationData":[TD([[makeQuery(id+"F0.imprint","IMPRINT",EDGE,{"derivedFrom":subQ0}),1.0]])]});}
            var Q66;
            {var subQ0=sQuery(id+"F0.wireOp",EDGE,"E25.top");Q66=makeQuery(id+"F0.imprint","IMPRINT",FACE,{"disambiguationData":[TD([[makeQuery(id+"F0.imprint","IMPRINT",EDGE,{"derivedFrom":subQ0}),-1.0]])]});}
            var Q67;
            {var subQ4=sQuery(id+"F0.wireOp",EDGE,"E25.top");Q67=makeQuery(id+"F0.imprint","IMPRINT",FACE,{"disambiguationData":[TD([[makeQuery(id+"F0.imprint","IMPRINT",EDGE,{"derivedFrom":subQ4}),1.0]])]});}
            var Q68;
            {var subQ1=sQuery(id+"F0.wireOp",EDGE,"E24.top");Q68=makeQuery(id+"F0.imprint","IMPRINT",FACE,{"disambiguationData":[TD([[makeQuery(id+"F0.imprint","IMPRINT",EDGE,{"derivedFrom":subQ1}),-1.0]])]});}
            var Q69;
            {var subQ0=sQuery(id+"F0.wireOp",EDGE,"E24.top");Q69=makeQuery(id+"F0.imprint","IMPRINT",FACE,{"disambiguationData":[TD([[makeQuery(id+"F0.imprint","IMPRINT",EDGE,{"derivedFrom":subQ0}),1.0]])]});}
            var Q70;
            {var subQ0=sQuery(id+"F0.wireOp",EDGE,"E23.top");Q70=makeQuery(id+"F0.imprint","IMPRINT",FACE,{"disambiguationData":[TD([[makeQuery(id+"F0.imprint","IMPRINT",EDGE,{"derivedFrom":subQ0}),-1.0]])]});}
            var Q71;
            {var subQ1=sQuery(id+"F0.wireOp",EDGE,"E23.top");Q71=makeQuery(id+"F0.imprint","IMPRINT",FACE,{"disambiguationData":[TD([[makeQuery(id+"F0.imprint","IMPRINT",EDGE,{"derivedFrom":subQ1}),1.0]])]});}
            var Q72;
            {var subQ0=sQuery(id+"F0.wireOp",EDGE,"E15");var subQ1=sQuery(id+"F0.wireOp",EDGE,"E5");var subQ2=makeQuery(id+"F0.imprint","INTERSECT",VERTEX,{"derivedFrom":[subQ1,subQ0]});Q72=makeQuery(id+"F0.imprint","IMPRINT",FACE,{"disambiguationData":[TD([[makeQuery(id+"F0.imprint","IMPRINT",EDGE,{"disambiguationData":[TD([[subQ2,-1.0]])],"derivedFrom":subQ1}),-1.0]])]});}
            var Q73;
            {var subQ0=sQuery(id+"F0.wireOp",EDGE,"E8");var subQ1=sQuery(id+"F0.wireOp",EDGE,"E4");var subQ2=makeQuery(id+"F0.imprint","INTERSECT",VERTEX,{"disambiguationData":[OD(0.0)],"derivedFrom":[subQ1,subQ0]});Q73=makeQuery(id+"F0.imprint","IMPRINT",FACE,{"disambiguationData":[TD([[makeQuery(id+"F0.imprint","IMPRINT",EDGE,{"disambiguationData":[TD([[subQ2,-1.0]])],"derivedFrom":subQ1}),1.0]])]});}
            var Q74;
            {var subQ0=sQuery(id+"F0.wireOp",EDGE,"E4");var subQ1=makeQuery(id+"F0.imprint","INTERSECT",VERTEX,{"derivedFrom":[subQ0,sQuery(id+"F0.wireOp",EDGE,"E11")]});Q74=makeQuery(id+"F0.imprint","IMPRINT",FACE,{"disambiguationData":[TD([[makeQuery(id+"F0.imprint","IMPRINT",EDGE,{"disambiguationData":[TD([[subQ1,1.0]])],"derivedFrom":subQ0}),1.0]])]});}
            var Q75;
            {var subQ0=sQuery(id+"F0.wireOp",EDGE,"E10");var subQ1=sQuery(id+"F0.wireOp",EDGE,"E7");var subQ2=makeQuery(id+"F0.imprint","INTERSECT",VERTEX,{"disambiguationData":[OD(0.0)],"derivedFrom":[subQ1,subQ0]});Q75=makeQuery(id+"F0.imprint","IMPRINT",FACE,{"disambiguationData":[TD([[makeQuery(id+"F0.imprint","IMPRINT",EDGE,{"disambiguationData":[TD([[subQ2,-1.0]])],"derivedFrom":subQ1}),1.0]])]});}
            var Q76;
            {var subQ0=sQuery(id+"F0.wireOp",EDGE,"E12");var subQ1=sQuery(id+"F0.wireOp",EDGE,"E7");var subQ2=makeQuery(id+"F0.imprint","INTERSECT",VERTEX,{"disambiguationData":[OD(1.0)],"derivedFrom":[subQ1,subQ0]});Q76=makeQuery(id+"F0.imprint","IMPRINT",FACE,{"disambiguationData":[TD([[makeQuery(id+"F0.imprint","IMPRINT",EDGE,{"disambiguationData":[TD([[subQ2,-1.0]])],"derivedFrom":subQ1}),1.0]])]});}
            var Q77;
            {var subQ0=sQuery(id+"F0.wireOp",EDGE,"E12");var subQ1=sQuery(id+"F0.wireOp",EDGE,"E6");var subQ2=makeQuery(id+"F0.imprint","INTERSECT",VERTEX,{"disambiguationData":[OD(0.0)],"derivedFrom":[subQ1,subQ0]});Q77=makeQuery(id+"F0.imprint","IMPRINT",FACE,{"disambiguationData":[TD([[makeQuery(id+"F0.imprint","IMPRINT",EDGE,{"disambiguationData":[TD([[subQ2,1.0]])],"derivedFrom":subQ1}),1.0]])]});}
            var Q78;
            {var subQ0=sQuery(id+"F0.wireOp",EDGE,"E14");var subQ1=sQuery(id+"F0.wireOp",EDGE,"E6");var subQ2=makeQuery(id+"F0.imprint","INTERSECT",VERTEX,{"disambiguationData":[OD(0.0)],"derivedFrom":[subQ1,subQ0]});Q78=makeQuery(id+"F0.imprint","IMPRINT",FACE,{"disambiguationData":[TD([[makeQuery(id+"F0.imprint","IMPRINT",EDGE,{"disambiguationData":[TD([[subQ2,-1.0]])],"derivedFrom":subQ1}),1.0]])]});}
            var Q79;
            {var subQ0=sQuery(id+"F0.wireOp",EDGE,"E14");var subQ1=sQuery(id+"F0.wireOp",EDGE,"E5");var subQ2=makeQuery(id+"F0.imprint","INTERSECT",VERTEX,{"disambiguationData":[OD(0.0)],"derivedFrom":[subQ1,subQ0]});Q79=makeQuery(id+"F0.imprint","IMPRINT",FACE,{"disambiguationData":[TD([[makeQuery(id+"F0.imprint","IMPRINT",EDGE,{"disambiguationData":[TD([[subQ2,-1.0]])],"derivedFrom":subQ1}),1.0]])]});}
            var Q80;
            {var subQ0=sQuery(id+"F0.wireOp",EDGE,"E5");var subQ1=makeQuery(id+"F0.imprint","INTERSECT",VERTEX,{"derivedFrom":[subQ0,sQuery(id+"F0.wireOp",EDGE,"E9")]});Q80=makeQuery(id+"F0.imprint","IMPRINT",FACE,{"disambiguationData":[TD([[makeQuery(id+"F0.imprint","IMPRINT",EDGE,{"disambiguationData":[TD([[subQ1,1.0]])],"derivedFrom":subQ0}),1.0]])]});}
            extrude(context, id + "F1", {"entities" : qUnion([Q0, Q1, Q2, Q3, Q4, Q5, Q6, Q7, Q8, Q9, Q10, Q11, Q12, Q13, Q14, Q15, Q16, Q17, Q18, Q19, Q20, Q21, Q22, Q23, Q24, Q25, Q26, Q27, Q28, Q29, Q30, Q31, Q32, Q33, Q34, Q35, Q36, Q37, Q38, Q39, Q40, Q41, Q42, Q43, Q44, Q45, Q46, Q47, Q48, Q49, Q50, Q51, Q52, Q53, Q54, Q55, Q56, Q57, Q58, Q59, Q60, Q61, Q62, Q63, Q64, Q65, Q66, Q67, Q68, Q69, Q70, Q71, Q72, Q73, Q74, Q75, Q76, Q77, Q78, Q79, Q80]), "oppositeDirection" : true, "depth" : 3.17 * mm});
        }
        {
            var Q0;
            Q0=makeQuery(id+"F1.opExtrude","CAP_EDGE",EDGE,{"disambiguationData":[OSD([sQuery(id+"F0.wireOp",EDGE,"a5322268-e1dc-436a-8e73-038b822e4c18")])],"isStart":false});
            var Q1;
            Q1=makeQuery(id+"F1.opExtrude","CAP_EDGE",EDGE,{"disambiguationData":[OSD([sQuery(id+"F0.wireOp",EDGE,"E7")])],"isStart":false});
            var Q2;
            Q2=makeQuery(id+"F1.opExtrude","CAP_EDGE",EDGE,{"disambiguationData":[OSD([sQuery(id+"F0.wireOp",EDGE,"1cb2681a-f61c-4038-b64f-4d8f3c1fa337")])],"isStart":true});
            var Q3;
            Q3=makeQuery(id+"F1.opExtrude","CAP_EDGE",EDGE,{"disambiguationData":[OSD([sQuery(id+"F0.wireOp",EDGE,"1cb2681a-f61c-4038-b64f-4d8f3c1fa337")])],"isStart":false});
            var Q4;
            Q4=makeQuery(id+"F1.opExtrude","CAP_EDGE",EDGE,{"disambiguationData":[OSD([sQuery(id+"F0.wireOp",EDGE,"E6")])],"isStart":false});
            var Q5;
            Q5=makeQuery(id+"F1.opExtrude","CAP_EDGE",EDGE,{"disambiguationData":[OSD([sQuery(id+"F0.wireOp",EDGE,"90b38568-d89f-4760-90db-baeff50cd179")])],"isStart":false});
            var Q6;
            Q6=makeQuery(id+"F1.opExtrude","CAP_EDGE",EDGE,{"disambiguationData":[OSD([sQuery(id+"F0.wireOp",EDGE,"E5")])],"isStart":false});
            var Q7;
            Q7=makeQuery(id+"F1.opExtrude","CAP_EDGE",EDGE,{"disambiguationData":[OSD([sQuery(id+"F0.wireOp",EDGE,"a8b6ce6c-9c41-4146-a937-b0af54ecc49b")])],"isStart":false});
            var Q8;
            Q8=makeQuery(id+"F1.opExtrude","CAP_EDGE",EDGE,{"disambiguationData":[OSD([sQuery(id+"F0.wireOp",EDGE,"E4")])],"isStart":false});
            var Q9;
            Q9=makeQuery(id+"F1.opExtrude","CAP_EDGE",EDGE,{"disambiguationData":[OSD([sQuery(id+"F0.wireOp",EDGE,"E6")])],"isStart":true});
            var Q10;
            Q10=makeQuery(id+"F1.opExtrude","CAP_EDGE",EDGE,{"disambiguationData":[OSD([sQuery(id+"F0.wireOp",EDGE,"90b38568-d89f-4760-90db-baeff50cd179")])],"isStart":true});
            var Q11;
            Q11=makeQuery(id+"F1.opExtrude","CAP_EDGE",EDGE,{"disambiguationData":[OSD([sQuery(id+"F0.wireOp",EDGE,"E5")])],"isStart":true});
            var Q12;
            Q12=makeQuery(id+"F1.opExtrude","CAP_EDGE",EDGE,{"disambiguationData":[OSD([sQuery(id+"F0.wireOp",EDGE,"a8b6ce6c-9c41-4146-a937-b0af54ecc49b")])],"isStart":true});
            var Q13;
            Q13=makeQuery(id+"F1.opExtrude","CAP_EDGE",EDGE,{"disambiguationData":[OSD([sQuery(id+"F0.wireOp",EDGE,"a5322268-e1dc-436a-8e73-038b822e4c18")])],"isStart":true});
            var Q14;
            Q14=makeQuery(id+"F1.opExtrude","CAP_EDGE",EDGE,{"disambiguationData":[OSD([sQuery(id+"F0.wireOp",EDGE,"E7")])],"isStart":true});
            var Q15;
            Q15=makeQuery(id+"F1.opExtrude","CAP_EDGE",EDGE,{"disambiguationData":[OSD([sQuery(id+"F0.wireOp",EDGE,"E4")])],"isStart":true});
            fillet(context, id + "F2", {"entities" : qUnion([Q0, Q1, Q2, Q3, Q4, Q5, Q6, Q7, Q8, Q9, Q10, Q11, Q12, Q13, Q14, Q15]), "radius" : 0.89 * mm, "tangentPropagation" : true, "allowEdgeOverflow" : false});
        }
        {
            var Q0;
            Q0=makeQuery(id+"F1.opExtrude","SWEPT_EDGE",EDGE,{"disambiguationData":[OSD([sQuery(id+"F0.wireOp",EDGE,"E10"),sQuery(id+"F0.wireOp",EDGE,"E19.rect.right")])]});
            var Q1;
            Q1=makeQuery(id+"F1.opExtrude","SWEPT_EDGE",EDGE,{"disambiguationData":[OSD([sQuery(id+"F0.wireOp",EDGE,"E12"),sQuery(id+"F0.wireOp",EDGE,"E20.rect.top")])]});
            var Q2;
            Q2=makeQuery(id+"F1.opExtrude","SWEPT_EDGE",EDGE,{"disambiguationData":[OSD([sQuery(id+"F0.wireOp",EDGE,"E17.rect.right"),sQuery(id+"F0.wireOp",EDGE,"E20.rect.top")])]});
            var Q3;
            Q3=makeQuery(id+"F1.opExtrude","SWEPT_EDGE",EDGE,{"disambiguationData":[OSD([sQuery(id+"F0.wireOp",EDGE,"E17.rect.right"),sQuery(id+"F0.wireOp",EDGE,"E20.rect.bottom")])]});
            var Q4;
            Q4=makeQuery(id+"F1.opExtrude","SWEPT_EDGE",EDGE,{"disambiguationData":[OSD([sQuery(id+"F0.wireOp",EDGE,"E17.rect.bottom"),sQuery(id+"F0.wireOp",EDGE,"E19.rect.right")])]});
            var Q5;
            Q5=makeQuery(id+"F1.opExtrude","SWEPT_EDGE",EDGE,{"disambiguationData":[OSD([sQuery(id+"F0.wireOp",EDGE,"E14"),sQuery(id+"F0.wireOp",EDGE,"E19.rect.right")])]});
            var Q6;
            Q6=makeQuery(id+"F1.opExtrude","SWEPT_EDGE",EDGE,{"disambiguationData":[OSD([sQuery(id+"F0.wireOp",EDGE,"E14"),sQuery(id+"F0.wireOp",EDGE,"E19.rect.left")])]});
            var Q7;
            Q7=makeQuery(id+"F1.opExtrude","SWEPT_EDGE",EDGE,{"disambiguationData":[OSD([sQuery(id+"F0.wireOp",EDGE,"E17.rect.bottom"),sQuery(id+"F0.wireOp",EDGE,"E19.rect.left")])]});
            var Q8;
            Q8=makeQuery(id+"F1.opExtrude","SWEPT_EDGE",EDGE,{"disambiguationData":[OSD([sQuery(id+"F0.wireOp",EDGE,"E17.rect.left"),sQuery(id+"F0.wireOp",EDGE,"E20.rect.bottom")])]});
            var Q9;
            Q9=makeQuery(id+"F1.opExtrude","SWEPT_EDGE",EDGE,{"disambiguationData":[OSD([sQuery(id+"F0.wireOp",EDGE,"E17.rect.left"),sQuery(id+"F0.wireOp",EDGE,"E20.rect.top")])]});
            var Q10;
            Q10=makeQuery(id+"F1.opExtrude","SWEPT_EDGE",EDGE,{"disambiguationData":[OSD([sQuery(id+"F0.wireOp",EDGE,"E17.rect.top"),sQuery(id+"F0.wireOp",EDGE,"E19.rect.left")])]});
            var Q11;
            Q11=makeQuery(id+"F1.opExtrude","SWEPT_EDGE",EDGE,{"disambiguationData":[OSD([sQuery(id+"F0.wireOp",EDGE,"E18.rect.top"),sQuery(id+"F0.wireOp",EDGE,"E18.rect.left")])]});
            var Q12;
            Q12=makeQuery(id+"F1.opExtrude","SWEPT_EDGE",EDGE,{"disambiguationData":[OSD([sQuery(id+"F0.wireOp",EDGE,"E18.rect.bottom"),sQuery(id+"F0.wireOp",EDGE,"E18.rect.left")])]});
            var Q13;
            Q13=makeQuery(id+"F1.opExtrude","SWEPT_EDGE",EDGE,{"disambiguationData":[OSD([sQuery(id+"F0.wireOp",EDGE,"E18.rect.bottom"),sQuery(id+"F0.wireOp",EDGE,"E18.rect.right")])]});
            var Q14;
            Q14=makeQuery(id+"F1.opExtrude","SWEPT_EDGE",EDGE,{"disambiguationData":[OSD([sQuery(id+"F0.wireOp",EDGE,"E18.rect.top"),sQuery(id+"F0.wireOp",EDGE,"E18.rect.right")])]});
            var Q15;
            Q15=makeQuery(id+"F1.opExtrude","SWEPT_EDGE",EDGE,{"disambiguationData":[OSD([sQuery(id+"F0.wireOp",EDGE,"E10"),sQuery(id+"F0.wireOp",EDGE,"E19.rect.left")])]});
            var Q16;
            Q16=makeQuery(id+"F1.opExtrude","SWEPT_EDGE",EDGE,{"disambiguationData":[OSD([sQuery(id+"F0.wireOp",EDGE,"E8"),sQuery(id+"F0.wireOp",EDGE,"E20.rect.bottom")])]});
            var Q17;
            Q17=makeQuery(id+"F1.opExtrude","SWEPT_EDGE",EDGE,{"disambiguationData":[OSD([sQuery(id+"F0.wireOp",EDGE,"E12"),sQuery(id+"F0.wireOp",EDGE,"E20.rect.bottom")])]});
            var Q18;
            Q18=makeQuery(id+"F1.opExtrude","SWEPT_EDGE",EDGE,{"disambiguationData":[OSD([sQuery(id+"F0.wireOp",EDGE,"E17.rect.top"),sQuery(id+"F0.wireOp",EDGE,"E19.rect.right")])]});
            var Q19;
            Q19=makeQuery(id+"F1.opExtrude","SWEPT_EDGE",EDGE,{"disambiguationData":[OSD([sQuery(id+"F0.wireOp",EDGE,"E8"),sQuery(id+"F0.wireOp",EDGE,"E20.rect.top")])]});
            fillet(context, id + "F3", {"entities" : qUnion([Q0, Q1, Q2, Q3, Q4, Q5, Q6, Q7, Q8, Q9, Q10, Q11, Q12, Q13, Q14, Q15, Q16, Q17, Q18, Q19]), "radius" : 1.02 * mm, "tangentPropagation" : true, "allowEdgeOverflow" : false});
        }
        {
            var Q0;
            {var subQ0=sQuery(id+"F0.wireOp",EDGE,"E20.rect.bottom");Q0=makeQuery(id+"F1.opExtrude","CAP_EDGE",EDGE,{"disambiguationData":[OSD([subQ0]),TDD([makeQuery(id+"F0.imprint","IMPRINT",EDGE,{"disambiguationData":[TD([[makeQuery(id+"F0.imprint","INTERSECT",VERTEX,{"derivedFrom":[sQuery(id+"F0.wireOp",EDGE,"E8"),subQ0]}),1.0]])],"derivedFrom":subQ0})])],"isStart":true});}
            var Q1;
            {var subQ0=sQuery(id+"F0.wireOp",EDGE,"E20.rect.bottom");var subQ1=sQuery(id+"F0.wireOp",EDGE,"E8");Q1=makeQuery(id+"F3.opFillet","BLEND_EDGE",EDGE,{"blendedFrom":[makeQuery(id+"F1.opExtrude","SWEPT_EDGE",EDGE,{"disambiguationData":[OSD([subQ1,subQ0])]}),makeQuery(id+"F1.opExtrude","CAP_FACE",FACE,{"disambiguationData":[OSD([sQuery(id+"F0.wireOp",EDGE,"E0"),sQuery(id+"F0.wireOp",EDGE,"E1"),sQuery(id+"F0.wireOp",EDGE,"E2"),sQuery(id+"F0.wireOp",EDGE,"E3"),sQuery(id+"F0.wireOp",EDGE,"E4"),sQuery(id+"F0.wireOp",EDGE,"E5"),sQuery(id+"F0.wireOp",EDGE,"E6"),sQuery(id+"F0.wireOp",EDGE,"E7"),subQ1,sQuery(id+"F0.wireOp",EDGE,"E9"),sQuery(id+"F0.wireOp",EDGE,"E10"),sQuery(id+"F0.wireOp",EDGE,"E11"),sQuery(id+"F0.wireOp",EDGE,"E12"),sQuery(id+"F0.wireOp",EDGE,"E13"),sQuery(id+"F0.wireOp",EDGE,"E14"),sQuery(id+"F0.wireOp",EDGE,"E15"),sQuery(id+"F0.wireOp",EDGE,"E17.rect.bottom"),sQuery(id+"F0.wireOp",EDGE,"E17.rect.top"),sQuery(id+"F0.wireOp",EDGE,"E17.rect.left"),sQuery(id+"F0.wireOp",EDGE,"E17.rect.right"),sQuery(id+"F0.wireOp",EDGE,"E18.rect.bottom"),sQuery(id+"F0.wireOp",EDGE,"E18.rect.top"),sQuery(id+"F0.wireOp",EDGE,"E18.rect.left"),sQuery(id+"F0.wireOp",EDGE,"E18.rect.right"),sQuery(id+"F0.wireOp",EDGE,"E19.rect.left"),sQuery(id+"F0.wireOp",EDGE,"E19.rect.right"),subQ0,sQuery(id+"F0.wireOp",EDGE,"E20.rect.top"),sQuery(id+"F0.wireOp",EDGE,"E23.top"),sQuery(id+"F0.wireOp",EDGE,"E23.left"),sQuery(id+"F0.wireOp",EDGE,"E23.right"),sQuery(id+"F0.wireOp",EDGE,"E24.top"),sQuery(id+"F0.wireOp",EDGE,"E24.left"),sQuery(id+"F0.wireOp",EDGE,"E24.right"),sQuery(id+"F0.wireOp",EDGE,"E25.top"),sQuery(id+"F0.wireOp",EDGE,"E25.left"),sQuery(id+"F0.wireOp",EDGE,"E25.right"),sQuery(id+"F0.wireOp",EDGE,"E26.top"),sQuery(id+"F0.wireOp",EDGE,"E26.left"),sQuery(id+"F0.wireOp",EDGE,"E26.right")])],"isStart":true})],"blendedInto":[makeQuery(id+"F1.opExtrude","CAP_FACE",FACE,{"disambiguationData":[OSD([sQuery(id+"F0.wireOp",EDGE,"E0"),sQuery(id+"F0.wireOp",EDGE,"E1"),sQuery(id+"F0.wireOp",EDGE,"E2"),sQuery(id+"F0.wireOp",EDGE,"E3"),sQuery(id+"F0.wireOp",EDGE,"E4"),sQuery(id+"F0.wireOp",EDGE,"E5"),sQuery(id+"F0.wireOp",EDGE,"E6"),sQuery(id+"F0.wireOp",EDGE,"E7"),subQ1,sQuery(id+"F0.wireOp",EDGE,"E9"),sQuery(id+"F0.wireOp",EDGE,"E10"),sQuery(id+"F0.wireOp",EDGE,"E11"),sQuery(id+"F0.wireOp",EDGE,"E12"),sQuery(id+"F0.wireOp",EDGE,"E13"),sQuery(id+"F0.wireOp",EDGE,"E14"),sQuery(id+"F0.wireOp",EDGE,"E15"),sQuery(id+"F0.wireOp",EDGE,"E17.rect.bottom"),sQuery(id+"F0.wireOp",EDGE,"E17.rect.top"),sQuery(id+"F0.wireOp",EDGE,"E17.rect.left"),sQuery(id+"F0.wireOp",EDGE,"E17.rect.right"),sQuery(id+"F0.wireOp",EDGE,"E18.rect.bottom"),sQuery(id+"F0.wireOp",EDGE,"E18.rect.top"),sQuery(id+"F0.wireOp",EDGE,"E18.rect.left"),sQuery(id+"F0.wireOp",EDGE,"E18.rect.right"),sQuery(id+"F0.wireOp",EDGE,"E19.rect.left"),sQuery(id+"F0.wireOp",EDGE,"E19.rect.right"),subQ0,sQuery(id+"F0.wireOp",EDGE,"E20.rect.top"),sQuery(id+"F0.wireOp",EDGE,"E23.top"),sQuery(id+"F0.wireOp",EDGE,"E23.left"),sQuery(id+"F0.wireOp",EDGE,"E23.right"),sQuery(id+"F0.wireOp",EDGE,"E24.top"),sQuery(id+"F0.wireOp",EDGE,"E24.left"),sQuery(id+"F0.wireOp",EDGE,"E24.right"),sQuery(id+"F0.wireOp",EDGE,"E25.top"),sQuery(id+"F0.wireOp",EDGE,"E25.left"),sQuery(id+"F0.wireOp",EDGE,"E25.right"),sQuery(id+"F0.wireOp",EDGE,"E26.top"),sQuery(id+"F0.wireOp",EDGE,"E26.left"),sQuery(id+"F0.wireOp",EDGE,"E26.right")])],"isStart":true})]});}
            var Q2;
            {var subQ0=sQuery(id+"F0.wireOp",EDGE,"E8");var subQ1=makeQuery(id+"F0.imprint","INTERSECT",VERTEX,{"disambiguationData":[OD(1.0)],"derivedFrom":[sQuery(id+"F0.wireOp",EDGE,"E4"),subQ0]});Q2=makeQuery(id+"F1.opExtrude","CAP_EDGE",EDGE,{"disambiguationData":[OSD([subQ0]),TDD([makeQuery(id+"F0.imprint","IMPRINT",EDGE,{"disambiguationData":[TD([[subQ1,1.0]])],"derivedFrom":subQ0}),makeQuery(id+"F0.imprint","IMPRINT",EDGE,{"disambiguationData":[TD([[makeQuery(id+"F0.imprint","INTERSECT",VERTEX,{"disambiguationData":[OD(1.0)],"derivedFrom":[sQuery(id+"F0.wireOp",EDGE,"E0"),subQ0]}),1.0]])],"derivedFrom":subQ0})])],"isStart":true});}
            var Q3;
            {var subQ0=sQuery(id+"F0.wireOp",EDGE,"E20.rect.bottom");var subQ1=sQuery(id+"F0.wireOp",EDGE,"E17.rect.right");Q3=makeQuery(id+"F3.opFillet","BLEND_EDGE",EDGE,{"blendedFrom":[makeQuery(id+"F1.opExtrude","SWEPT_EDGE",EDGE,{"disambiguationData":[OSD([subQ1,subQ0])]}),makeQuery(id+"F1.opExtrude","CAP_FACE",FACE,{"disambiguationData":[OSD([sQuery(id+"F0.wireOp",EDGE,"E0"),sQuery(id+"F0.wireOp",EDGE,"E1"),sQuery(id+"F0.wireOp",EDGE,"E2"),sQuery(id+"F0.wireOp",EDGE,"E3"),sQuery(id+"F0.wireOp",EDGE,"E4"),sQuery(id+"F0.wireOp",EDGE,"E5"),sQuery(id+"F0.wireOp",EDGE,"E6"),sQuery(id+"F0.wireOp",EDGE,"E7"),sQuery(id+"F0.wireOp",EDGE,"E8"),sQuery(id+"F0.wireOp",EDGE,"E9"),sQuery(id+"F0.wireOp",EDGE,"E10"),sQuery(id+"F0.wireOp",EDGE,"E11"),sQuery(id+"F0.wireOp",EDGE,"E12"),sQuery(id+"F0.wireOp",EDGE,"E13"),sQuery(id+"F0.wireOp",EDGE,"E14"),sQuery(id+"F0.wireOp",EDGE,"E15"),sQuery(id+"F0.wireOp",EDGE,"E17.rect.bottom"),sQuery(id+"F0.wireOp",EDGE,"E17.rect.top"),sQuery(id+"F0.wireOp",EDGE,"E17.rect.left"),subQ1,sQuery(id+"F0.wireOp",EDGE,"E18.rect.bottom"),sQuery(id+"F0.wireOp",EDGE,"E18.rect.top"),sQuery(id+"F0.wireOp",EDGE,"E18.rect.left"),sQuery(id+"F0.wireOp",EDGE,"E18.rect.right"),sQuery(id+"F0.wireOp",EDGE,"E19.rect.left"),sQuery(id+"F0.wireOp",EDGE,"E19.rect.right"),subQ0,sQuery(id+"F0.wireOp",EDGE,"E20.rect.top"),sQuery(id+"F0.wireOp",EDGE,"E23.top"),sQuery(id+"F0.wireOp",EDGE,"E23.left"),sQuery(id+"F0.wireOp",EDGE,"E23.right"),sQuery(id+"F0.wireOp",EDGE,"E24.top"),sQuery(id+"F0.wireOp",EDGE,"E24.left"),sQuery(id+"F0.wireOp",EDGE,"E24.right"),sQuery(id+"F0.wireOp",EDGE,"E25.top"),sQuery(id+"F0.wireOp",EDGE,"E25.left"),sQuery(id+"F0.wireOp",EDGE,"E25.right"),sQuery(id+"F0.wireOp",EDGE,"E26.top"),sQuery(id+"F0.wireOp",EDGE,"E26.left"),sQuery(id+"F0.wireOp",EDGE,"E26.right")])],"isStart":true})],"blendedInto":[makeQuery(id+"F1.opExtrude","CAP_FACE",FACE,{"disambiguationData":[OSD([sQuery(id+"F0.wireOp",EDGE,"E0"),sQuery(id+"F0.wireOp",EDGE,"E1"),sQuery(id+"F0.wireOp",EDGE,"E2"),sQuery(id+"F0.wireOp",EDGE,"E3"),sQuery(id+"F0.wireOp",EDGE,"E4"),sQuery(id+"F0.wireOp",EDGE,"E5"),sQuery(id+"F0.wireOp",EDGE,"E6"),sQuery(id+"F0.wireOp",EDGE,"E7"),sQuery(id+"F0.wireOp",EDGE,"E8"),sQuery(id+"F0.wireOp",EDGE,"E9"),sQuery(id+"F0.wireOp",EDGE,"E10"),sQuery(id+"F0.wireOp",EDGE,"E11"),sQuery(id+"F0.wireOp",EDGE,"E12"),sQuery(id+"F0.wireOp",EDGE,"E13"),sQuery(id+"F0.wireOp",EDGE,"E14"),sQuery(id+"F0.wireOp",EDGE,"E15"),sQuery(id+"F0.wireOp",EDGE,"E17.rect.bottom"),sQuery(id+"F0.wireOp",EDGE,"E17.rect.top"),sQuery(id+"F0.wireOp",EDGE,"E17.rect.left"),subQ1,sQuery(id+"F0.wireOp",EDGE,"E18.rect.bottom"),sQuery(id+"F0.wireOp",EDGE,"E18.rect.top"),sQuery(id+"F0.wireOp",EDGE,"E18.rect.left"),sQuery(id+"F0.wireOp",EDGE,"E18.rect.right"),sQuery(id+"F0.wireOp",EDGE,"E19.rect.left"),sQuery(id+"F0.wireOp",EDGE,"E19.rect.right"),subQ0,sQuery(id+"F0.wireOp",EDGE,"E20.rect.top"),sQuery(id+"F0.wireOp",EDGE,"E23.top"),sQuery(id+"F0.wireOp",EDGE,"E23.left"),sQuery(id+"F0.wireOp",EDGE,"E23.right"),sQuery(id+"F0.wireOp",EDGE,"E24.top"),sQuery(id+"F0.wireOp",EDGE,"E24.left"),sQuery(id+"F0.wireOp",EDGE,"E24.right"),sQuery(id+"F0.wireOp",EDGE,"E25.top"),sQuery(id+"F0.wireOp",EDGE,"E25.left"),sQuery(id+"F0.wireOp",EDGE,"E25.right"),sQuery(id+"F0.wireOp",EDGE,"E26.top"),sQuery(id+"F0.wireOp",EDGE,"E26.left"),sQuery(id+"F0.wireOp",EDGE,"E26.right")])],"isStart":true})]});}
            var Q4;
            {var subQ0=sQuery(id+"F0.wireOp",EDGE,"E20.rect.top");Q4=makeQuery(id+"F1.opExtrude","CAP_EDGE",EDGE,{"disambiguationData":[OSD([subQ0]),TDD([makeQuery(id+"F0.imprint","IMPRINT",EDGE,{"disambiguationData":[TD([[makeQuery(id+"F0.imprint","INTERSECT",VERTEX,{"derivedFrom":[sQuery(id+"F0.wireOp",EDGE,"E8"),subQ0]}),1.0]])],"derivedFrom":subQ0})])],"isStart":true});}
            var Q5;
            {var subQ0=sQuery(id+"F0.wireOp",EDGE,"E20.rect.top");var subQ1=sQuery(id+"F0.wireOp",EDGE,"E8");Q5=makeQuery(id+"F3.opFillet","BLEND_EDGE",EDGE,{"blendedFrom":[makeQuery(id+"F1.opExtrude","SWEPT_EDGE",EDGE,{"disambiguationData":[OSD([subQ1,subQ0])]}),makeQuery(id+"F1.opExtrude","CAP_FACE",FACE,{"disambiguationData":[OSD([sQuery(id+"F0.wireOp",EDGE,"E0"),sQuery(id+"F0.wireOp",EDGE,"E1"),sQuery(id+"F0.wireOp",EDGE,"E2"),sQuery(id+"F0.wireOp",EDGE,"E3"),sQuery(id+"F0.wireOp",EDGE,"E4"),sQuery(id+"F0.wireOp",EDGE,"E5"),sQuery(id+"F0.wireOp",EDGE,"E6"),sQuery(id+"F0.wireOp",EDGE,"E7"),subQ1,sQuery(id+"F0.wireOp",EDGE,"E9"),sQuery(id+"F0.wireOp",EDGE,"E10"),sQuery(id+"F0.wireOp",EDGE,"E11"),sQuery(id+"F0.wireOp",EDGE,"E12"),sQuery(id+"F0.wireOp",EDGE,"E13"),sQuery(id+"F0.wireOp",EDGE,"E14"),sQuery(id+"F0.wireOp",EDGE,"E15"),sQuery(id+"F0.wireOp",EDGE,"E17.rect.bottom"),sQuery(id+"F0.wireOp",EDGE,"E17.rect.top"),sQuery(id+"F0.wireOp",EDGE,"E17.rect.left"),sQuery(id+"F0.wireOp",EDGE,"E17.rect.right"),sQuery(id+"F0.wireOp",EDGE,"E18.rect.bottom"),sQuery(id+"F0.wireOp",EDGE,"E18.rect.top"),sQuery(id+"F0.wireOp",EDGE,"E18.rect.left"),sQuery(id+"F0.wireOp",EDGE,"E18.rect.right"),sQuery(id+"F0.wireOp",EDGE,"E19.rect.left"),sQuery(id+"F0.wireOp",EDGE,"E19.rect.right"),sQuery(id+"F0.wireOp",EDGE,"E20.rect.bottom"),subQ0,sQuery(id+"F0.wireOp",EDGE,"E23.top"),sQuery(id+"F0.wireOp",EDGE,"E23.left"),sQuery(id+"F0.wireOp",EDGE,"E23.right"),sQuery(id+"F0.wireOp",EDGE,"E24.top"),sQuery(id+"F0.wireOp",EDGE,"E24.left"),sQuery(id+"F0.wireOp",EDGE,"E24.right"),sQuery(id+"F0.wireOp",EDGE,"E25.top"),sQuery(id+"F0.wireOp",EDGE,"E25.left"),sQuery(id+"F0.wireOp",EDGE,"E25.right"),sQuery(id+"F0.wireOp",EDGE,"E26.top"),sQuery(id+"F0.wireOp",EDGE,"E26.left"),sQuery(id+"F0.wireOp",EDGE,"E26.right")])],"isStart":true})],"blendedInto":[makeQuery(id+"F1.opExtrude","CAP_FACE",FACE,{"disambiguationData":[OSD([sQuery(id+"F0.wireOp",EDGE,"E0"),sQuery(id+"F0.wireOp",EDGE,"E1"),sQuery(id+"F0.wireOp",EDGE,"E2"),sQuery(id+"F0.wireOp",EDGE,"E3"),sQuery(id+"F0.wireOp",EDGE,"E4"),sQuery(id+"F0.wireOp",EDGE,"E5"),sQuery(id+"F0.wireOp",EDGE,"E6"),sQuery(id+"F0.wireOp",EDGE,"E7"),subQ1,sQuery(id+"F0.wireOp",EDGE,"E9"),sQuery(id+"F0.wireOp",EDGE,"E10"),sQuery(id+"F0.wireOp",EDGE,"E11"),sQuery(id+"F0.wireOp",EDGE,"E12"),sQuery(id+"F0.wireOp",EDGE,"E13"),sQuery(id+"F0.wireOp",EDGE,"E14"),sQuery(id+"F0.wireOp",EDGE,"E15"),sQuery(id+"F0.wireOp",EDGE,"E17.rect.bottom"),sQuery(id+"F0.wireOp",EDGE,"E17.rect.top"),sQuery(id+"F0.wireOp",EDGE,"E17.rect.left"),sQuery(id+"F0.wireOp",EDGE,"E17.rect.right"),sQuery(id+"F0.wireOp",EDGE,"E18.rect.bottom"),sQuery(id+"F0.wireOp",EDGE,"E18.rect.top"),sQuery(id+"F0.wireOp",EDGE,"E18.rect.left"),sQuery(id+"F0.wireOp",EDGE,"E18.rect.right"),sQuery(id+"F0.wireOp",EDGE,"E19.rect.left"),sQuery(id+"F0.wireOp",EDGE,"E19.rect.right"),sQuery(id+"F0.wireOp",EDGE,"E20.rect.bottom"),subQ0,sQuery(id+"F0.wireOp",EDGE,"E23.top"),sQuery(id+"F0.wireOp",EDGE,"E23.left"),sQuery(id+"F0.wireOp",EDGE,"E23.right"),sQuery(id+"F0.wireOp",EDGE,"E24.top"),sQuery(id+"F0.wireOp",EDGE,"E24.left"),sQuery(id+"F0.wireOp",EDGE,"E24.right"),sQuery(id+"F0.wireOp",EDGE,"E25.top"),sQuery(id+"F0.wireOp",EDGE,"E25.left"),sQuery(id+"F0.wireOp",EDGE,"E25.right"),sQuery(id+"F0.wireOp",EDGE,"E26.top"),sQuery(id+"F0.wireOp",EDGE,"E26.left"),sQuery(id+"F0.wireOp",EDGE,"E26.right")])],"isStart":true})]});}
            var Q6;
            {var subQ0=sQuery(id+"F0.wireOp",EDGE,"E8");var subQ1=makeQuery(id+"F0.imprint","INTERSECT",VERTEX,{"disambiguationData":[OD(0.0)],"derivedFrom":[sQuery(id+"F0.wireOp",EDGE,"E5"),subQ0]});Q6=makeQuery(id+"F1.opExtrude","CAP_EDGE",EDGE,{"disambiguationData":[OSD([subQ0]),TDD([makeQuery(id+"F0.imprint","IMPRINT",EDGE,{"disambiguationData":[TD([[makeQuery(id+"F0.imprint","INTERSECT",VERTEX,{"disambiguationData":[OD(1.0)],"derivedFrom":[sQuery(id+"F0.wireOp",EDGE,"E3"),subQ0]}),-1.0]])],"derivedFrom":subQ0}),makeQuery(id+"F0.imprint","IMPRINT",EDGE,{"disambiguationData":[TD([[subQ1,-1.0]])],"derivedFrom":subQ0})])],"isStart":true});}
            var Q7;
            {var subQ0=sQuery(id+"F0.wireOp",EDGE,"E20.rect.top");var subQ1=sQuery(id+"F0.wireOp",EDGE,"E17.rect.right");Q7=makeQuery(id+"F3.opFillet","BLEND_EDGE",EDGE,{"blendedFrom":[makeQuery(id+"F1.opExtrude","SWEPT_EDGE",EDGE,{"disambiguationData":[OSD([subQ1,subQ0])]}),makeQuery(id+"F1.opExtrude","CAP_FACE",FACE,{"disambiguationData":[OSD([sQuery(id+"F0.wireOp",EDGE,"E0"),sQuery(id+"F0.wireOp",EDGE,"E1"),sQuery(id+"F0.wireOp",EDGE,"E2"),sQuery(id+"F0.wireOp",EDGE,"E3"),sQuery(id+"F0.wireOp",EDGE,"E4"),sQuery(id+"F0.wireOp",EDGE,"E5"),sQuery(id+"F0.wireOp",EDGE,"E6"),sQuery(id+"F0.wireOp",EDGE,"E7"),sQuery(id+"F0.wireOp",EDGE,"E8"),sQuery(id+"F0.wireOp",EDGE,"E9"),sQuery(id+"F0.wireOp",EDGE,"E10"),sQuery(id+"F0.wireOp",EDGE,"E11"),sQuery(id+"F0.wireOp",EDGE,"E12"),sQuery(id+"F0.wireOp",EDGE,"E13"),sQuery(id+"F0.wireOp",EDGE,"E14"),sQuery(id+"F0.wireOp",EDGE,"E15"),sQuery(id+"F0.wireOp",EDGE,"E17.rect.bottom"),sQuery(id+"F0.wireOp",EDGE,"E17.rect.top"),sQuery(id+"F0.wireOp",EDGE,"E17.rect.left"),subQ1,sQuery(id+"F0.wireOp",EDGE,"E18.rect.bottom"),sQuery(id+"F0.wireOp",EDGE,"E18.rect.top"),sQuery(id+"F0.wireOp",EDGE,"E18.rect.left"),sQuery(id+"F0.wireOp",EDGE,"E18.rect.right"),sQuery(id+"F0.wireOp",EDGE,"E19.rect.left"),sQuery(id+"F0.wireOp",EDGE,"E19.rect.right"),sQuery(id+"F0.wireOp",EDGE,"E20.rect.bottom"),subQ0,sQuery(id+"F0.wireOp",EDGE,"E23.top"),sQuery(id+"F0.wireOp",EDGE,"E23.left"),sQuery(id+"F0.wireOp",EDGE,"E23.right"),sQuery(id+"F0.wireOp",EDGE,"E24.top"),sQuery(id+"F0.wireOp",EDGE,"E24.left"),sQuery(id+"F0.wireOp",EDGE,"E24.right"),sQuery(id+"F0.wireOp",EDGE,"E25.top"),sQuery(id+"F0.wireOp",EDGE,"E25.left"),sQuery(id+"F0.wireOp",EDGE,"E25.right"),sQuery(id+"F0.wireOp",EDGE,"E26.top"),sQuery(id+"F0.wireOp",EDGE,"E26.left"),sQuery(id+"F0.wireOp",EDGE,"E26.right")])],"isStart":true})],"blendedInto":[makeQuery(id+"F1.opExtrude","CAP_FACE",FACE,{"disambiguationData":[OSD([sQuery(id+"F0.wireOp",EDGE,"E0"),sQuery(id+"F0.wireOp",EDGE,"E1"),sQuery(id+"F0.wireOp",EDGE,"E2"),sQuery(id+"F0.wireOp",EDGE,"E3"),sQuery(id+"F0.wireOp",EDGE,"E4"),sQuery(id+"F0.wireOp",EDGE,"E5"),sQuery(id+"F0.wireOp",EDGE,"E6"),sQuery(id+"F0.wireOp",EDGE,"E7"),sQuery(id+"F0.wireOp",EDGE,"E8"),sQuery(id+"F0.wireOp",EDGE,"E9"),sQuery(id+"F0.wireOp",EDGE,"E10"),sQuery(id+"F0.wireOp",EDGE,"E11"),sQuery(id+"F0.wireOp",EDGE,"E12"),sQuery(id+"F0.wireOp",EDGE,"E13"),sQuery(id+"F0.wireOp",EDGE,"E14"),sQuery(id+"F0.wireOp",EDGE,"E15"),sQuery(id+"F0.wireOp",EDGE,"E17.rect.bottom"),sQuery(id+"F0.wireOp",EDGE,"E17.rect.top"),sQuery(id+"F0.wireOp",EDGE,"E17.rect.left"),subQ1,sQuery(id+"F0.wireOp",EDGE,"E18.rect.bottom"),sQuery(id+"F0.wireOp",EDGE,"E18.rect.top"),sQuery(id+"F0.wireOp",EDGE,"E18.rect.left"),sQuery(id+"F0.wireOp",EDGE,"E18.rect.right"),sQuery(id+"F0.wireOp",EDGE,"E19.rect.left"),sQuery(id+"F0.wireOp",EDGE,"E19.rect.right"),sQuery(id+"F0.wireOp",EDGE,"E20.rect.bottom"),subQ0,sQuery(id+"F0.wireOp",EDGE,"E23.top"),sQuery(id+"F0.wireOp",EDGE,"E23.left"),sQuery(id+"F0.wireOp",EDGE,"E23.right"),sQuery(id+"F0.wireOp",EDGE,"E24.top"),sQuery(id+"F0.wireOp",EDGE,"E24.left"),sQuery(id+"F0.wireOp",EDGE,"E24.right"),sQuery(id+"F0.wireOp",EDGE,"E25.top"),sQuery(id+"F0.wireOp",EDGE,"E25.left"),sQuery(id+"F0.wireOp",EDGE,"E25.right"),sQuery(id+"F0.wireOp",EDGE,"E26.top"),sQuery(id+"F0.wireOp",EDGE,"E26.left"),sQuery(id+"F0.wireOp",EDGE,"E26.right")])],"isStart":true})]});}
            var Q8;
            {var subQ0=sQuery(id+"F0.wireOp",EDGE,"E10");var subQ1=makeQuery(id+"F0.imprint","INTERSECT",VERTEX,{"disambiguationData":[OD(1.0)],"derivedFrom":[sQuery(id+"F0.wireOp",EDGE,"E4"),subQ0]});Q8=makeQuery(id+"F1.opExtrude","CAP_EDGE",EDGE,{"disambiguationData":[OSD([subQ0]),TDD([makeQuery(id+"F0.imprint","IMPRINT",EDGE,{"disambiguationData":[TD([[makeQuery(id+"F0.imprint","INTERSECT",VERTEX,{"disambiguationData":[OD(1.0)],"derivedFrom":[sQuery(id+"F0.wireOp",EDGE,"E0"),subQ0]}),-1.0]])],"derivedFrom":subQ0}),makeQuery(id+"F0.imprint","IMPRINT",EDGE,{"disambiguationData":[TD([[subQ1,-1.0]])],"derivedFrom":subQ0})])],"isStart":true});}
            var Q9;
            {var subQ0=sQuery(id+"F0.wireOp",EDGE,"E19.rect.right");var subQ1=sQuery(id+"F0.wireOp",EDGE,"E10");Q9=makeQuery(id+"F3.opFillet","BLEND_EDGE",EDGE,{"blendedFrom":[makeQuery(id+"F1.opExtrude","SWEPT_EDGE",EDGE,{"disambiguationData":[OSD([subQ1,subQ0])]}),makeQuery(id+"F1.opExtrude","CAP_FACE",FACE,{"disambiguationData":[OSD([sQuery(id+"F0.wireOp",EDGE,"E0"),sQuery(id+"F0.wireOp",EDGE,"E1"),sQuery(id+"F0.wireOp",EDGE,"E2"),sQuery(id+"F0.wireOp",EDGE,"E3"),sQuery(id+"F0.wireOp",EDGE,"E4"),sQuery(id+"F0.wireOp",EDGE,"E5"),sQuery(id+"F0.wireOp",EDGE,"E6"),sQuery(id+"F0.wireOp",EDGE,"E7"),sQuery(id+"F0.wireOp",EDGE,"E8"),sQuery(id+"F0.wireOp",EDGE,"E9"),subQ1,sQuery(id+"F0.wireOp",EDGE,"E11"),sQuery(id+"F0.wireOp",EDGE,"E12"),sQuery(id+"F0.wireOp",EDGE,"E13"),sQuery(id+"F0.wireOp",EDGE,"E14"),sQuery(id+"F0.wireOp",EDGE,"E15"),sQuery(id+"F0.wireOp",EDGE,"E17.rect.bottom"),sQuery(id+"F0.wireOp",EDGE,"E17.rect.top"),sQuery(id+"F0.wireOp",EDGE,"E17.rect.left"),sQuery(id+"F0.wireOp",EDGE,"E17.rect.right"),sQuery(id+"F0.wireOp",EDGE,"E18.rect.bottom"),sQuery(id+"F0.wireOp",EDGE,"E18.rect.top"),sQuery(id+"F0.wireOp",EDGE,"E18.rect.left"),sQuery(id+"F0.wireOp",EDGE,"E18.rect.right"),sQuery(id+"F0.wireOp",EDGE,"E19.rect.left"),subQ0,sQuery(id+"F0.wireOp",EDGE,"E20.rect.bottom"),sQuery(id+"F0.wireOp",EDGE,"E20.rect.top"),sQuery(id+"F0.wireOp",EDGE,"E23.top"),sQuery(id+"F0.wireOp",EDGE,"E23.left"),sQuery(id+"F0.wireOp",EDGE,"E23.right"),sQuery(id+"F0.wireOp",EDGE,"E24.top"),sQuery(id+"F0.wireOp",EDGE,"E24.left"),sQuery(id+"F0.wireOp",EDGE,"E24.right"),sQuery(id+"F0.wireOp",EDGE,"E25.top"),sQuery(id+"F0.wireOp",EDGE,"E25.left"),sQuery(id+"F0.wireOp",EDGE,"E25.right"),sQuery(id+"F0.wireOp",EDGE,"E26.top"),sQuery(id+"F0.wireOp",EDGE,"E26.left"),sQuery(id+"F0.wireOp",EDGE,"E26.right")])],"isStart":true})],"blendedInto":[makeQuery(id+"F1.opExtrude","CAP_FACE",FACE,{"disambiguationData":[OSD([sQuery(id+"F0.wireOp",EDGE,"E0"),sQuery(id+"F0.wireOp",EDGE,"E1"),sQuery(id+"F0.wireOp",EDGE,"E2"),sQuery(id+"F0.wireOp",EDGE,"E3"),sQuery(id+"F0.wireOp",EDGE,"E4"),sQuery(id+"F0.wireOp",EDGE,"E5"),sQuery(id+"F0.wireOp",EDGE,"E6"),sQuery(id+"F0.wireOp",EDGE,"E7"),sQuery(id+"F0.wireOp",EDGE,"E8"),sQuery(id+"F0.wireOp",EDGE,"E9"),subQ1,sQuery(id+"F0.wireOp",EDGE,"E11"),sQuery(id+"F0.wireOp",EDGE,"E12"),sQuery(id+"F0.wireOp",EDGE,"E13"),sQuery(id+"F0.wireOp",EDGE,"E14"),sQuery(id+"F0.wireOp",EDGE,"E15"),sQuery(id+"F0.wireOp",EDGE,"E17.rect.bottom"),sQuery(id+"F0.wireOp",EDGE,"E17.rect.top"),sQuery(id+"F0.wireOp",EDGE,"E17.rect.left"),sQuery(id+"F0.wireOp",EDGE,"E17.rect.right"),sQuery(id+"F0.wireOp",EDGE,"E18.rect.bottom"),sQuery(id+"F0.wireOp",EDGE,"E18.rect.top"),sQuery(id+"F0.wireOp",EDGE,"E18.rect.left"),sQuery(id+"F0.wireOp",EDGE,"E18.rect.right"),sQuery(id+"F0.wireOp",EDGE,"E19.rect.left"),subQ0,sQuery(id+"F0.wireOp",EDGE,"E20.rect.bottom"),sQuery(id+"F0.wireOp",EDGE,"E20.rect.top"),sQuery(id+"F0.wireOp",EDGE,"E23.top"),sQuery(id+"F0.wireOp",EDGE,"E23.left"),sQuery(id+"F0.wireOp",EDGE,"E23.right"),sQuery(id+"F0.wireOp",EDGE,"E24.top"),sQuery(id+"F0.wireOp",EDGE,"E24.left"),sQuery(id+"F0.wireOp",EDGE,"E24.right"),sQuery(id+"F0.wireOp",EDGE,"E25.top"),sQuery(id+"F0.wireOp",EDGE,"E25.left"),sQuery(id+"F0.wireOp",EDGE,"E25.right"),sQuery(id+"F0.wireOp",EDGE,"E26.top"),sQuery(id+"F0.wireOp",EDGE,"E26.left"),sQuery(id+"F0.wireOp",EDGE,"E26.right")])],"isStart":true})]});}
            var Q10;
            {var subQ0=sQuery(id+"F0.wireOp",EDGE,"E19.rect.right");Q10=makeQuery(id+"F1.opExtrude","CAP_EDGE",EDGE,{"disambiguationData":[OSD([subQ0]),TDD([makeQuery(id+"F0.imprint","IMPRINT",EDGE,{"disambiguationData":[TD([[makeQuery(id+"F0.imprint","INTERSECT",VERTEX,{"derivedFrom":[sQuery(id+"F0.wireOp",EDGE,"E10"),subQ0]}),-1.0]])],"derivedFrom":subQ0})])],"isStart":true});}
            var Q11;
            {var subQ0=sQuery(id+"F0.wireOp",EDGE,"E19.rect.right");var subQ1=sQuery(id+"F0.wireOp",EDGE,"E17.rect.bottom");Q11=makeQuery(id+"F3.opFillet","BLEND_EDGE",EDGE,{"blendedFrom":[makeQuery(id+"F1.opExtrude","SWEPT_EDGE",EDGE,{"disambiguationData":[OSD([subQ1,subQ0])]}),makeQuery(id+"F1.opExtrude","CAP_FACE",FACE,{"disambiguationData":[OSD([sQuery(id+"F0.wireOp",EDGE,"E0"),sQuery(id+"F0.wireOp",EDGE,"E1"),sQuery(id+"F0.wireOp",EDGE,"E2"),sQuery(id+"F0.wireOp",EDGE,"E3"),sQuery(id+"F0.wireOp",EDGE,"E4"),sQuery(id+"F0.wireOp",EDGE,"E5"),sQuery(id+"F0.wireOp",EDGE,"E6"),sQuery(id+"F0.wireOp",EDGE,"E7"),sQuery(id+"F0.wireOp",EDGE,"E8"),sQuery(id+"F0.wireOp",EDGE,"E9"),sQuery(id+"F0.wireOp",EDGE,"E10"),sQuery(id+"F0.wireOp",EDGE,"E11"),sQuery(id+"F0.wireOp",EDGE,"E12"),sQuery(id+"F0.wireOp",EDGE,"E13"),sQuery(id+"F0.wireOp",EDGE,"E14"),sQuery(id+"F0.wireOp",EDGE,"E15"),subQ1,sQuery(id+"F0.wireOp",EDGE,"E17.rect.top"),sQuery(id+"F0.wireOp",EDGE,"E17.rect.left"),sQuery(id+"F0.wireOp",EDGE,"E17.rect.right"),sQuery(id+"F0.wireOp",EDGE,"E18.rect.bottom"),sQuery(id+"F0.wireOp",EDGE,"E18.rect.top"),sQuery(id+"F0.wireOp",EDGE,"E18.rect.left"),sQuery(id+"F0.wireOp",EDGE,"E18.rect.right"),sQuery(id+"F0.wireOp",EDGE,"E19.rect.left"),subQ0,sQuery(id+"F0.wireOp",EDGE,"E20.rect.bottom"),sQuery(id+"F0.wireOp",EDGE,"E20.rect.top"),sQuery(id+"F0.wireOp",EDGE,"E23.top"),sQuery(id+"F0.wireOp",EDGE,"E23.left"),sQuery(id+"F0.wireOp",EDGE,"E23.right"),sQuery(id+"F0.wireOp",EDGE,"E24.top"),sQuery(id+"F0.wireOp",EDGE,"E24.left"),sQuery(id+"F0.wireOp",EDGE,"E24.right"),sQuery(id+"F0.wireOp",EDGE,"E25.top"),sQuery(id+"F0.wireOp",EDGE,"E25.left"),sQuery(id+"F0.wireOp",EDGE,"E25.right"),sQuery(id+"F0.wireOp",EDGE,"E26.top"),sQuery(id+"F0.wireOp",EDGE,"E26.left"),sQuery(id+"F0.wireOp",EDGE,"E26.right")])],"isStart":true})],"blendedInto":[makeQuery(id+"F1.opExtrude","CAP_FACE",FACE,{"disambiguationData":[OSD([sQuery(id+"F0.wireOp",EDGE,"E0"),sQuery(id+"F0.wireOp",EDGE,"E1"),sQuery(id+"F0.wireOp",EDGE,"E2"),sQuery(id+"F0.wireOp",EDGE,"E3"),sQuery(id+"F0.wireOp",EDGE,"E4"),sQuery(id+"F0.wireOp",EDGE,"E5"),sQuery(id+"F0.wireOp",EDGE,"E6"),sQuery(id+"F0.wireOp",EDGE,"E7"),sQuery(id+"F0.wireOp",EDGE,"E8"),sQuery(id+"F0.wireOp",EDGE,"E9"),sQuery(id+"F0.wireOp",EDGE,"E10"),sQuery(id+"F0.wireOp",EDGE,"E11"),sQuery(id+"F0.wireOp",EDGE,"E12"),sQuery(id+"F0.wireOp",EDGE,"E13"),sQuery(id+"F0.wireOp",EDGE,"E14"),sQuery(id+"F0.wireOp",EDGE,"E15"),subQ1,sQuery(id+"F0.wireOp",EDGE,"E17.rect.top"),sQuery(id+"F0.wireOp",EDGE,"E17.rect.left"),sQuery(id+"F0.wireOp",EDGE,"E17.rect.right"),sQuery(id+"F0.wireOp",EDGE,"E18.rect.bottom"),sQuery(id+"F0.wireOp",EDGE,"E18.rect.top"),sQuery(id+"F0.wireOp",EDGE,"E18.rect.left"),sQuery(id+"F0.wireOp",EDGE,"E18.rect.right"),sQuery(id+"F0.wireOp",EDGE,"E19.rect.left"),subQ0,sQuery(id+"F0.wireOp",EDGE,"E20.rect.bottom"),sQuery(id+"F0.wireOp",EDGE,"E20.rect.top"),sQuery(id+"F0.wireOp",EDGE,"E23.top"),sQuery(id+"F0.wireOp",EDGE,"E23.left"),sQuery(id+"F0.wireOp",EDGE,"E23.right"),sQuery(id+"F0.wireOp",EDGE,"E24.top"),sQuery(id+"F0.wireOp",EDGE,"E24.left"),sQuery(id+"F0.wireOp",EDGE,"E24.right"),sQuery(id+"F0.wireOp",EDGE,"E25.top"),sQuery(id+"F0.wireOp",EDGE,"E25.left"),sQuery(id+"F0.wireOp",EDGE,"E25.right"),sQuery(id+"F0.wireOp",EDGE,"E26.top"),sQuery(id+"F0.wireOp",EDGE,"E26.left"),sQuery(id+"F0.wireOp",EDGE,"E26.right")])],"isStart":true})]});}
            var Q12;
            {var subQ0=sQuery(id+"F0.wireOp",EDGE,"E17.rect.bottom");Q12=makeQuery(id+"F1.opExtrude","CAP_EDGE",EDGE,{"disambiguationData":[OSD([subQ0]),TDD([makeQuery(id+"F0.imprint","IMPRINT",EDGE,{"disambiguationData":[TD([[makeQuery(id+"F0.imprint","INTERSECT",VERTEX,{"derivedFrom":[subQ0,sQuery(id+"F0.wireOp",EDGE,"E19.rect.right")]}),-1.0]])],"derivedFrom":subQ0})])],"isStart":true});}
            var Q13;
            {var subQ0=sQuery(id+"F0.wireOp",EDGE,"E17.rect.bottom");Q13=makeQuery(id+"F1.opExtrude","CAP_EDGE",EDGE,{"disambiguationData":[OSD([subQ0]),TDD([makeQuery(id+"F0.imprint","IMPRINT",EDGE,{"disambiguationData":[TD([[makeQuery(id+"F0.imprint","INTERSECT",VERTEX,{"derivedFrom":[subQ0,sQuery(id+"F0.wireOp",EDGE,"E19.rect.left")]}),1.0]])],"derivedFrom":subQ0})])],"isStart":true});}
            var Q14;
            {var subQ0=sQuery(id+"F0.wireOp",EDGE,"E19.rect.left");var subQ1=sQuery(id+"F0.wireOp",EDGE,"E17.rect.bottom");Q14=makeQuery(id+"F3.opFillet","BLEND_EDGE",EDGE,{"blendedFrom":[makeQuery(id+"F1.opExtrude","SWEPT_EDGE",EDGE,{"disambiguationData":[OSD([subQ1,subQ0])]}),makeQuery(id+"F1.opExtrude","CAP_FACE",FACE,{"disambiguationData":[OSD([sQuery(id+"F0.wireOp",EDGE,"E0"),sQuery(id+"F0.wireOp",EDGE,"E1"),sQuery(id+"F0.wireOp",EDGE,"E2"),sQuery(id+"F0.wireOp",EDGE,"E3"),sQuery(id+"F0.wireOp",EDGE,"E4"),sQuery(id+"F0.wireOp",EDGE,"E5"),sQuery(id+"F0.wireOp",EDGE,"E6"),sQuery(id+"F0.wireOp",EDGE,"E7"),sQuery(id+"F0.wireOp",EDGE,"E8"),sQuery(id+"F0.wireOp",EDGE,"E9"),sQuery(id+"F0.wireOp",EDGE,"E10"),sQuery(id+"F0.wireOp",EDGE,"E11"),sQuery(id+"F0.wireOp",EDGE,"E12"),sQuery(id+"F0.wireOp",EDGE,"E13"),sQuery(id+"F0.wireOp",EDGE,"E14"),sQuery(id+"F0.wireOp",EDGE,"E15"),subQ1,sQuery(id+"F0.wireOp",EDGE,"E17.rect.top"),sQuery(id+"F0.wireOp",EDGE,"E17.rect.left"),sQuery(id+"F0.wireOp",EDGE,"E17.rect.right"),sQuery(id+"F0.wireOp",EDGE,"E18.rect.bottom"),sQuery(id+"F0.wireOp",EDGE,"E18.rect.top"),sQuery(id+"F0.wireOp",EDGE,"E18.rect.left"),sQuery(id+"F0.wireOp",EDGE,"E18.rect.right"),subQ0,sQuery(id+"F0.wireOp",EDGE,"E19.rect.right"),sQuery(id+"F0.wireOp",EDGE,"E20.rect.bottom"),sQuery(id+"F0.wireOp",EDGE,"E20.rect.top"),sQuery(id+"F0.wireOp",EDGE,"E23.top"),sQuery(id+"F0.wireOp",EDGE,"E23.left"),sQuery(id+"F0.wireOp",EDGE,"E23.right"),sQuery(id+"F0.wireOp",EDGE,"E24.top"),sQuery(id+"F0.wireOp",EDGE,"E24.left"),sQuery(id+"F0.wireOp",EDGE,"E24.right"),sQuery(id+"F0.wireOp",EDGE,"E25.top"),sQuery(id+"F0.wireOp",EDGE,"E25.left"),sQuery(id+"F0.wireOp",EDGE,"E25.right"),sQuery(id+"F0.wireOp",EDGE,"E26.top"),sQuery(id+"F0.wireOp",EDGE,"E26.left"),sQuery(id+"F0.wireOp",EDGE,"E26.right")])],"isStart":true})],"blendedInto":[makeQuery(id+"F1.opExtrude","CAP_FACE",FACE,{"disambiguationData":[OSD([sQuery(id+"F0.wireOp",EDGE,"E0"),sQuery(id+"F0.wireOp",EDGE,"E1"),sQuery(id+"F0.wireOp",EDGE,"E2"),sQuery(id+"F0.wireOp",EDGE,"E3"),sQuery(id+"F0.wireOp",EDGE,"E4"),sQuery(id+"F0.wireOp",EDGE,"E5"),sQuery(id+"F0.wireOp",EDGE,"E6"),sQuery(id+"F0.wireOp",EDGE,"E7"),sQuery(id+"F0.wireOp",EDGE,"E8"),sQuery(id+"F0.wireOp",EDGE,"E9"),sQuery(id+"F0.wireOp",EDGE,"E10"),sQuery(id+"F0.wireOp",EDGE,"E11"),sQuery(id+"F0.wireOp",EDGE,"E12"),sQuery(id+"F0.wireOp",EDGE,"E13"),sQuery(id+"F0.wireOp",EDGE,"E14"),sQuery(id+"F0.wireOp",EDGE,"E15"),subQ1,sQuery(id+"F0.wireOp",EDGE,"E17.rect.top"),sQuery(id+"F0.wireOp",EDGE,"E17.rect.left"),sQuery(id+"F0.wireOp",EDGE,"E17.rect.right"),sQuery(id+"F0.wireOp",EDGE,"E18.rect.bottom"),sQuery(id+"F0.wireOp",EDGE,"E18.rect.top"),sQuery(id+"F0.wireOp",EDGE,"E18.rect.left"),sQuery(id+"F0.wireOp",EDGE,"E18.rect.right"),subQ0,sQuery(id+"F0.wireOp",EDGE,"E19.rect.right"),sQuery(id+"F0.wireOp",EDGE,"E20.rect.bottom"),sQuery(id+"F0.wireOp",EDGE,"E20.rect.top"),sQuery(id+"F0.wireOp",EDGE,"E23.top"),sQuery(id+"F0.wireOp",EDGE,"E23.left"),sQuery(id+"F0.wireOp",EDGE,"E23.right"),sQuery(id+"F0.wireOp",EDGE,"E24.top"),sQuery(id+"F0.wireOp",EDGE,"E24.left"),sQuery(id+"F0.wireOp",EDGE,"E24.right"),sQuery(id+"F0.wireOp",EDGE,"E25.top"),sQuery(id+"F0.wireOp",EDGE,"E25.left"),sQuery(id+"F0.wireOp",EDGE,"E25.right"),sQuery(id+"F0.wireOp",EDGE,"E26.top"),sQuery(id+"F0.wireOp",EDGE,"E26.left"),sQuery(id+"F0.wireOp",EDGE,"E26.right")])],"isStart":true})]});}
            var Q15;
            {var subQ0=sQuery(id+"F0.wireOp",EDGE,"E19.rect.left");Q15=makeQuery(id+"F1.opExtrude","CAP_EDGE",EDGE,{"disambiguationData":[OSD([subQ0]),TDD([makeQuery(id+"F0.imprint","IMPRINT",EDGE,{"disambiguationData":[TD([[makeQuery(id+"F0.imprint","INTERSECT",VERTEX,{"derivedFrom":[sQuery(id+"F0.wireOp",EDGE,"E10"),subQ0]}),-1.0]])],"derivedFrom":subQ0})])],"isStart":true});}
            var Q16;
            {var subQ0=sQuery(id+"F0.wireOp",EDGE,"E19.rect.left");var subQ1=sQuery(id+"F0.wireOp",EDGE,"E10");Q16=makeQuery(id+"F3.opFillet","BLEND_EDGE",EDGE,{"blendedFrom":[makeQuery(id+"F1.opExtrude","SWEPT_EDGE",EDGE,{"disambiguationData":[OSD([subQ1,subQ0])]}),makeQuery(id+"F1.opExtrude","CAP_FACE",FACE,{"disambiguationData":[OSD([sQuery(id+"F0.wireOp",EDGE,"E0"),sQuery(id+"F0.wireOp",EDGE,"E1"),sQuery(id+"F0.wireOp",EDGE,"E2"),sQuery(id+"F0.wireOp",EDGE,"E3"),sQuery(id+"F0.wireOp",EDGE,"E4"),sQuery(id+"F0.wireOp",EDGE,"E5"),sQuery(id+"F0.wireOp",EDGE,"E6"),sQuery(id+"F0.wireOp",EDGE,"E7"),sQuery(id+"F0.wireOp",EDGE,"E8"),sQuery(id+"F0.wireOp",EDGE,"E9"),subQ1,sQuery(id+"F0.wireOp",EDGE,"E11"),sQuery(id+"F0.wireOp",EDGE,"E12"),sQuery(id+"F0.wireOp",EDGE,"E13"),sQuery(id+"F0.wireOp",EDGE,"E14"),sQuery(id+"F0.wireOp",EDGE,"E15"),sQuery(id+"F0.wireOp",EDGE,"E17.rect.bottom"),sQuery(id+"F0.wireOp",EDGE,"E17.rect.top"),sQuery(id+"F0.wireOp",EDGE,"E17.rect.left"),sQuery(id+"F0.wireOp",EDGE,"E17.rect.right"),sQuery(id+"F0.wireOp",EDGE,"E18.rect.bottom"),sQuery(id+"F0.wireOp",EDGE,"E18.rect.top"),sQuery(id+"F0.wireOp",EDGE,"E18.rect.left"),sQuery(id+"F0.wireOp",EDGE,"E18.rect.right"),subQ0,sQuery(id+"F0.wireOp",EDGE,"E19.rect.right"),sQuery(id+"F0.wireOp",EDGE,"E20.rect.bottom"),sQuery(id+"F0.wireOp",EDGE,"E20.rect.top"),sQuery(id+"F0.wireOp",EDGE,"E23.top"),sQuery(id+"F0.wireOp",EDGE,"E23.left"),sQuery(id+"F0.wireOp",EDGE,"E23.right"),sQuery(id+"F0.wireOp",EDGE,"E24.top"),sQuery(id+"F0.wireOp",EDGE,"E24.left"),sQuery(id+"F0.wireOp",EDGE,"E24.right"),sQuery(id+"F0.wireOp",EDGE,"E25.top"),sQuery(id+"F0.wireOp",EDGE,"E25.left"),sQuery(id+"F0.wireOp",EDGE,"E25.right"),sQuery(id+"F0.wireOp",EDGE,"E26.top"),sQuery(id+"F0.wireOp",EDGE,"E26.left"),sQuery(id+"F0.wireOp",EDGE,"E26.right")])],"isStart":true})],"blendedInto":[makeQuery(id+"F1.opExtrude","CAP_FACE",FACE,{"disambiguationData":[OSD([sQuery(id+"F0.wireOp",EDGE,"E0"),sQuery(id+"F0.wireOp",EDGE,"E1"),sQuery(id+"F0.wireOp",EDGE,"E2"),sQuery(id+"F0.wireOp",EDGE,"E3"),sQuery(id+"F0.wireOp",EDGE,"E4"),sQuery(id+"F0.wireOp",EDGE,"E5"),sQuery(id+"F0.wireOp",EDGE,"E6"),sQuery(id+"F0.wireOp",EDGE,"E7"),sQuery(id+"F0.wireOp",EDGE,"E8"),sQuery(id+"F0.wireOp",EDGE,"E9"),subQ1,sQuery(id+"F0.wireOp",EDGE,"E11"),sQuery(id+"F0.wireOp",EDGE,"E12"),sQuery(id+"F0.wireOp",EDGE,"E13"),sQuery(id+"F0.wireOp",EDGE,"E14"),sQuery(id+"F0.wireOp",EDGE,"E15"),sQuery(id+"F0.wireOp",EDGE,"E17.rect.bottom"),sQuery(id+"F0.wireOp",EDGE,"E17.rect.top"),sQuery(id+"F0.wireOp",EDGE,"E17.rect.left"),sQuery(id+"F0.wireOp",EDGE,"E17.rect.right"),sQuery(id+"F0.wireOp",EDGE,"E18.rect.bottom"),sQuery(id+"F0.wireOp",EDGE,"E18.rect.top"),sQuery(id+"F0.wireOp",EDGE,"E18.rect.left"),sQuery(id+"F0.wireOp",EDGE,"E18.rect.right"),subQ0,sQuery(id+"F0.wireOp",EDGE,"E19.rect.right"),sQuery(id+"F0.wireOp",EDGE,"E20.rect.bottom"),sQuery(id+"F0.wireOp",EDGE,"E20.rect.top"),sQuery(id+"F0.wireOp",EDGE,"E23.top"),sQuery(id+"F0.wireOp",EDGE,"E23.left"),sQuery(id+"F0.wireOp",EDGE,"E23.right"),sQuery(id+"F0.wireOp",EDGE,"E24.top"),sQuery(id+"F0.wireOp",EDGE,"E24.left"),sQuery(id+"F0.wireOp",EDGE,"E24.right"),sQuery(id+"F0.wireOp",EDGE,"E25.top"),sQuery(id+"F0.wireOp",EDGE,"E25.left"),sQuery(id+"F0.wireOp",EDGE,"E25.right"),sQuery(id+"F0.wireOp",EDGE,"E26.top"),sQuery(id+"F0.wireOp",EDGE,"E26.left"),sQuery(id+"F0.wireOp",EDGE,"E26.right")])],"isStart":true})]});}
            var Q17;
            {var subQ0=sQuery(id+"F0.wireOp",EDGE,"E10");var subQ1=makeQuery(id+"F0.imprint","INTERSECT",VERTEX,{"disambiguationData":[OD(1.0)],"derivedFrom":[sQuery(id+"F0.wireOp",EDGE,"E7"),subQ0]});Q17=makeQuery(id+"F1.opExtrude","CAP_EDGE",EDGE,{"disambiguationData":[OSD([subQ0]),TDD([makeQuery(id+"F0.imprint","IMPRINT",EDGE,{"disambiguationData":[TD([[subQ1,1.0]])],"derivedFrom":subQ0}),makeQuery(id+"F0.imprint","IMPRINT",EDGE,{"disambiguationData":[TD([[makeQuery(id+"F0.imprint","INTERSECT",VERTEX,{"disambiguationData":[OD(1.0)],"derivedFrom":[sQuery(id+"F0.wireOp",EDGE,"E1"),subQ0]}),1.0]])],"derivedFrom":subQ0})])],"isStart":true});}
            var Q18;
            {var subQ0=sQuery(id+"F0.wireOp",EDGE,"E12");var subQ1=makeQuery(id+"F0.imprint","INTERSECT",VERTEX,{"disambiguationData":[OD(1.0)],"derivedFrom":[sQuery(id+"F0.wireOp",EDGE,"E7"),subQ0]});Q18=makeQuery(id+"F1.opExtrude","CAP_EDGE",EDGE,{"disambiguationData":[OSD([subQ0]),TDD([makeQuery(id+"F0.imprint","IMPRINT",EDGE,{"disambiguationData":[TD([[makeQuery(id+"F0.imprint","INTERSECT",VERTEX,{"disambiguationData":[OD(1.0)],"derivedFrom":[sQuery(id+"F0.wireOp",EDGE,"E1"),subQ0]}),-1.0]])],"derivedFrom":subQ0}),makeQuery(id+"F0.imprint","IMPRINT",EDGE,{"disambiguationData":[TD([[subQ1,-1.0]])],"derivedFrom":subQ0})])],"isStart":true});}
            var Q19;
            {var subQ0=sQuery(id+"F0.wireOp",EDGE,"E20.rect.bottom");var subQ1=sQuery(id+"F0.wireOp",EDGE,"E12");Q19=makeQuery(id+"F3.opFillet","BLEND_EDGE",EDGE,{"blendedFrom":[makeQuery(id+"F1.opExtrude","SWEPT_EDGE",EDGE,{"disambiguationData":[OSD([subQ1,subQ0])]}),makeQuery(id+"F1.opExtrude","CAP_FACE",FACE,{"disambiguationData":[OSD([sQuery(id+"F0.wireOp",EDGE,"E0"),sQuery(id+"F0.wireOp",EDGE,"E1"),sQuery(id+"F0.wireOp",EDGE,"E2"),sQuery(id+"F0.wireOp",EDGE,"E3"),sQuery(id+"F0.wireOp",EDGE,"E4"),sQuery(id+"F0.wireOp",EDGE,"E5"),sQuery(id+"F0.wireOp",EDGE,"E6"),sQuery(id+"F0.wireOp",EDGE,"E7"),sQuery(id+"F0.wireOp",EDGE,"E8"),sQuery(id+"F0.wireOp",EDGE,"E9"),sQuery(id+"F0.wireOp",EDGE,"E10"),sQuery(id+"F0.wireOp",EDGE,"E11"),subQ1,sQuery(id+"F0.wireOp",EDGE,"E13"),sQuery(id+"F0.wireOp",EDGE,"E14"),sQuery(id+"F0.wireOp",EDGE,"E15"),sQuery(id+"F0.wireOp",EDGE,"E17.rect.bottom"),sQuery(id+"F0.wireOp",EDGE,"E17.rect.top"),sQuery(id+"F0.wireOp",EDGE,"E17.rect.left"),sQuery(id+"F0.wireOp",EDGE,"E17.rect.right"),sQuery(id+"F0.wireOp",EDGE,"E18.rect.bottom"),sQuery(id+"F0.wireOp",EDGE,"E18.rect.top"),sQuery(id+"F0.wireOp",EDGE,"E18.rect.left"),sQuery(id+"F0.wireOp",EDGE,"E18.rect.right"),sQuery(id+"F0.wireOp",EDGE,"E19.rect.left"),sQuery(id+"F0.wireOp",EDGE,"E19.rect.right"),subQ0,sQuery(id+"F0.wireOp",EDGE,"E20.rect.top"),sQuery(id+"F0.wireOp",EDGE,"E23.top"),sQuery(id+"F0.wireOp",EDGE,"E23.left"),sQuery(id+"F0.wireOp",EDGE,"E23.right"),sQuery(id+"F0.wireOp",EDGE,"E24.top"),sQuery(id+"F0.wireOp",EDGE,"E24.left"),sQuery(id+"F0.wireOp",EDGE,"E24.right"),sQuery(id+"F0.wireOp",EDGE,"E25.top"),sQuery(id+"F0.wireOp",EDGE,"E25.left"),sQuery(id+"F0.wireOp",EDGE,"E25.right"),sQuery(id+"F0.wireOp",EDGE,"E26.top"),sQuery(id+"F0.wireOp",EDGE,"E26.left"),sQuery(id+"F0.wireOp",EDGE,"E26.right")])],"isStart":true})],"blendedInto":[makeQuery(id+"F1.opExtrude","CAP_FACE",FACE,{"disambiguationData":[OSD([sQuery(id+"F0.wireOp",EDGE,"E0"),sQuery(id+"F0.wireOp",EDGE,"E1"),sQuery(id+"F0.wireOp",EDGE,"E2"),sQuery(id+"F0.wireOp",EDGE,"E3"),sQuery(id+"F0.wireOp",EDGE,"E4"),sQuery(id+"F0.wireOp",EDGE,"E5"),sQuery(id+"F0.wireOp",EDGE,"E6"),sQuery(id+"F0.wireOp",EDGE,"E7"),sQuery(id+"F0.wireOp",EDGE,"E8"),sQuery(id+"F0.wireOp",EDGE,"E9"),sQuery(id+"F0.wireOp",EDGE,"E10"),sQuery(id+"F0.wireOp",EDGE,"E11"),subQ1,sQuery(id+"F0.wireOp",EDGE,"E13"),sQuery(id+"F0.wireOp",EDGE,"E14"),sQuery(id+"F0.wireOp",EDGE,"E15"),sQuery(id+"F0.wireOp",EDGE,"E17.rect.bottom"),sQuery(id+"F0.wireOp",EDGE,"E17.rect.top"),sQuery(id+"F0.wireOp",EDGE,"E17.rect.left"),sQuery(id+"F0.wireOp",EDGE,"E17.rect.right"),sQuery(id+"F0.wireOp",EDGE,"E18.rect.bottom"),sQuery(id+"F0.wireOp",EDGE,"E18.rect.top"),sQuery(id+"F0.wireOp",EDGE,"E18.rect.left"),sQuery(id+"F0.wireOp",EDGE,"E18.rect.right"),sQuery(id+"F0.wireOp",EDGE,"E19.rect.left"),sQuery(id+"F0.wireOp",EDGE,"E19.rect.right"),subQ0,sQuery(id+"F0.wireOp",EDGE,"E20.rect.top"),sQuery(id+"F0.wireOp",EDGE,"E23.top"),sQuery(id+"F0.wireOp",EDGE,"E23.left"),sQuery(id+"F0.wireOp",EDGE,"E23.right"),sQuery(id+"F0.wireOp",EDGE,"E24.top"),sQuery(id+"F0.wireOp",EDGE,"E24.left"),sQuery(id+"F0.wireOp",EDGE,"E24.right"),sQuery(id+"F0.wireOp",EDGE,"E25.top"),sQuery(id+"F0.wireOp",EDGE,"E25.left"),sQuery(id+"F0.wireOp",EDGE,"E25.right"),sQuery(id+"F0.wireOp",EDGE,"E26.top"),sQuery(id+"F0.wireOp",EDGE,"E26.left"),sQuery(id+"F0.wireOp",EDGE,"E26.right")])],"isStart":true})]});}
            var Q20;
            {var subQ0=sQuery(id+"F0.wireOp",EDGE,"E20.rect.bottom");Q20=makeQuery(id+"F1.opExtrude","CAP_EDGE",EDGE,{"disambiguationData":[OSD([subQ0]),TDD([makeQuery(id+"F0.imprint","IMPRINT",EDGE,{"disambiguationData":[TD([[makeQuery(id+"F0.imprint","INTERSECT",VERTEX,{"derivedFrom":[sQuery(id+"F0.wireOp",EDGE,"E12"),subQ0]}),-1.0]])],"derivedFrom":subQ0})])],"isStart":true});}
            var Q21;
            {var subQ0=sQuery(id+"F0.wireOp",EDGE,"E20.rect.bottom");var subQ1=sQuery(id+"F0.wireOp",EDGE,"E17.rect.left");Q21=makeQuery(id+"F3.opFillet","BLEND_EDGE",EDGE,{"blendedFrom":[makeQuery(id+"F1.opExtrude","SWEPT_EDGE",EDGE,{"disambiguationData":[OSD([subQ1,subQ0])]}),makeQuery(id+"F1.opExtrude","CAP_FACE",FACE,{"disambiguationData":[OSD([sQuery(id+"F0.wireOp",EDGE,"E0"),sQuery(id+"F0.wireOp",EDGE,"E1"),sQuery(id+"F0.wireOp",EDGE,"E2"),sQuery(id+"F0.wireOp",EDGE,"E3"),sQuery(id+"F0.wireOp",EDGE,"E4"),sQuery(id+"F0.wireOp",EDGE,"E5"),sQuery(id+"F0.wireOp",EDGE,"E6"),sQuery(id+"F0.wireOp",EDGE,"E7"),sQuery(id+"F0.wireOp",EDGE,"E8"),sQuery(id+"F0.wireOp",EDGE,"E9"),sQuery(id+"F0.wireOp",EDGE,"E10"),sQuery(id+"F0.wireOp",EDGE,"E11"),sQuery(id+"F0.wireOp",EDGE,"E12"),sQuery(id+"F0.wireOp",EDGE,"E13"),sQuery(id+"F0.wireOp",EDGE,"E14"),sQuery(id+"F0.wireOp",EDGE,"E15"),sQuery(id+"F0.wireOp",EDGE,"E17.rect.bottom"),sQuery(id+"F0.wireOp",EDGE,"E17.rect.top"),subQ1,sQuery(id+"F0.wireOp",EDGE,"E17.rect.right"),sQuery(id+"F0.wireOp",EDGE,"E18.rect.bottom"),sQuery(id+"F0.wireOp",EDGE,"E18.rect.top"),sQuery(id+"F0.wireOp",EDGE,"E18.rect.left"),sQuery(id+"F0.wireOp",EDGE,"E18.rect.right"),sQuery(id+"F0.wireOp",EDGE,"E19.rect.left"),sQuery(id+"F0.wireOp",EDGE,"E19.rect.right"),subQ0,sQuery(id+"F0.wireOp",EDGE,"E20.rect.top"),sQuery(id+"F0.wireOp",EDGE,"E23.top"),sQuery(id+"F0.wireOp",EDGE,"E23.left"),sQuery(id+"F0.wireOp",EDGE,"E23.right"),sQuery(id+"F0.wireOp",EDGE,"E24.top"),sQuery(id+"F0.wireOp",EDGE,"E24.left"),sQuery(id+"F0.wireOp",EDGE,"E24.right"),sQuery(id+"F0.wireOp",EDGE,"E25.top"),sQuery(id+"F0.wireOp",EDGE,"E25.left"),sQuery(id+"F0.wireOp",EDGE,"E25.right"),sQuery(id+"F0.wireOp",EDGE,"E26.top"),sQuery(id+"F0.wireOp",EDGE,"E26.left"),sQuery(id+"F0.wireOp",EDGE,"E26.right")])],"isStart":true})],"blendedInto":[makeQuery(id+"F1.opExtrude","CAP_FACE",FACE,{"disambiguationData":[OSD([sQuery(id+"F0.wireOp",EDGE,"E0"),sQuery(id+"F0.wireOp",EDGE,"E1"),sQuery(id+"F0.wireOp",EDGE,"E2"),sQuery(id+"F0.wireOp",EDGE,"E3"),sQuery(id+"F0.wireOp",EDGE,"E4"),sQuery(id+"F0.wireOp",EDGE,"E5"),sQuery(id+"F0.wireOp",EDGE,"E6"),sQuery(id+"F0.wireOp",EDGE,"E7"),sQuery(id+"F0.wireOp",EDGE,"E8"),sQuery(id+"F0.wireOp",EDGE,"E9"),sQuery(id+"F0.wireOp",EDGE,"E10"),sQuery(id+"F0.wireOp",EDGE,"E11"),sQuery(id+"F0.wireOp",EDGE,"E12"),sQuery(id+"F0.wireOp",EDGE,"E13"),sQuery(id+"F0.wireOp",EDGE,"E14"),sQuery(id+"F0.wireOp",EDGE,"E15"),sQuery(id+"F0.wireOp",EDGE,"E17.rect.bottom"),sQuery(id+"F0.wireOp",EDGE,"E17.rect.top"),subQ1,sQuery(id+"F0.wireOp",EDGE,"E17.rect.right"),sQuery(id+"F0.wireOp",EDGE,"E18.rect.bottom"),sQuery(id+"F0.wireOp",EDGE,"E18.rect.top"),sQuery(id+"F0.wireOp",EDGE,"E18.rect.left"),sQuery(id+"F0.wireOp",EDGE,"E18.rect.right"),sQuery(id+"F0.wireOp",EDGE,"E19.rect.left"),sQuery(id+"F0.wireOp",EDGE,"E19.rect.right"),subQ0,sQuery(id+"F0.wireOp",EDGE,"E20.rect.top"),sQuery(id+"F0.wireOp",EDGE,"E23.top"),sQuery(id+"F0.wireOp",EDGE,"E23.left"),sQuery(id+"F0.wireOp",EDGE,"E23.right"),sQuery(id+"F0.wireOp",EDGE,"E24.top"),sQuery(id+"F0.wireOp",EDGE,"E24.left"),sQuery(id+"F0.wireOp",EDGE,"E24.right"),sQuery(id+"F0.wireOp",EDGE,"E25.top"),sQuery(id+"F0.wireOp",EDGE,"E25.left"),sQuery(id+"F0.wireOp",EDGE,"E25.right"),sQuery(id+"F0.wireOp",EDGE,"E26.top"),sQuery(id+"F0.wireOp",EDGE,"E26.left"),sQuery(id+"F0.wireOp",EDGE,"E26.right")])],"isStart":true})]});}
            var Q22;
            {var subQ0=sQuery(id+"F0.wireOp",EDGE,"E20.rect.top");var subQ1=sQuery(id+"F0.wireOp",EDGE,"E17.rect.left");Q22=makeQuery(id+"F3.opFillet","BLEND_EDGE",EDGE,{"blendedFrom":[makeQuery(id+"F1.opExtrude","SWEPT_EDGE",EDGE,{"disambiguationData":[OSD([subQ1,subQ0])]}),makeQuery(id+"F1.opExtrude","CAP_FACE",FACE,{"disambiguationData":[OSD([sQuery(id+"F0.wireOp",EDGE,"E0"),sQuery(id+"F0.wireOp",EDGE,"E1"),sQuery(id+"F0.wireOp",EDGE,"E2"),sQuery(id+"F0.wireOp",EDGE,"E3"),sQuery(id+"F0.wireOp",EDGE,"E4"),sQuery(id+"F0.wireOp",EDGE,"E5"),sQuery(id+"F0.wireOp",EDGE,"E6"),sQuery(id+"F0.wireOp",EDGE,"E7"),sQuery(id+"F0.wireOp",EDGE,"E8"),sQuery(id+"F0.wireOp",EDGE,"E9"),sQuery(id+"F0.wireOp",EDGE,"E10"),sQuery(id+"F0.wireOp",EDGE,"E11"),sQuery(id+"F0.wireOp",EDGE,"E12"),sQuery(id+"F0.wireOp",EDGE,"E13"),sQuery(id+"F0.wireOp",EDGE,"E14"),sQuery(id+"F0.wireOp",EDGE,"E15"),sQuery(id+"F0.wireOp",EDGE,"E17.rect.bottom"),sQuery(id+"F0.wireOp",EDGE,"E17.rect.top"),subQ1,sQuery(id+"F0.wireOp",EDGE,"E17.rect.right"),sQuery(id+"F0.wireOp",EDGE,"E18.rect.bottom"),sQuery(id+"F0.wireOp",EDGE,"E18.rect.top"),sQuery(id+"F0.wireOp",EDGE,"E18.rect.left"),sQuery(id+"F0.wireOp",EDGE,"E18.rect.right"),sQuery(id+"F0.wireOp",EDGE,"E19.rect.left"),sQuery(id+"F0.wireOp",EDGE,"E19.rect.right"),sQuery(id+"F0.wireOp",EDGE,"E20.rect.bottom"),subQ0,sQuery(id+"F0.wireOp",EDGE,"E23.top"),sQuery(id+"F0.wireOp",EDGE,"E23.left"),sQuery(id+"F0.wireOp",EDGE,"E23.right"),sQuery(id+"F0.wireOp",EDGE,"E24.top"),sQuery(id+"F0.wireOp",EDGE,"E24.left"),sQuery(id+"F0.wireOp",EDGE,"E24.right"),sQuery(id+"F0.wireOp",EDGE,"E25.top"),sQuery(id+"F0.wireOp",EDGE,"E25.left"),sQuery(id+"F0.wireOp",EDGE,"E25.right"),sQuery(id+"F0.wireOp",EDGE,"E26.top"),sQuery(id+"F0.wireOp",EDGE,"E26.left"),sQuery(id+"F0.wireOp",EDGE,"E26.right")])],"isStart":true})],"blendedInto":[makeQuery(id+"F1.opExtrude","CAP_FACE",FACE,{"disambiguationData":[OSD([sQuery(id+"F0.wireOp",EDGE,"E0"),sQuery(id+"F0.wireOp",EDGE,"E1"),sQuery(id+"F0.wireOp",EDGE,"E2"),sQuery(id+"F0.wireOp",EDGE,"E3"),sQuery(id+"F0.wireOp",EDGE,"E4"),sQuery(id+"F0.wireOp",EDGE,"E5"),sQuery(id+"F0.wireOp",EDGE,"E6"),sQuery(id+"F0.wireOp",EDGE,"E7"),sQuery(id+"F0.wireOp",EDGE,"E8"),sQuery(id+"F0.wireOp",EDGE,"E9"),sQuery(id+"F0.wireOp",EDGE,"E10"),sQuery(id+"F0.wireOp",EDGE,"E11"),sQuery(id+"F0.wireOp",EDGE,"E12"),sQuery(id+"F0.wireOp",EDGE,"E13"),sQuery(id+"F0.wireOp",EDGE,"E14"),sQuery(id+"F0.wireOp",EDGE,"E15"),sQuery(id+"F0.wireOp",EDGE,"E17.rect.bottom"),sQuery(id+"F0.wireOp",EDGE,"E17.rect.top"),subQ1,sQuery(id+"F0.wireOp",EDGE,"E17.rect.right"),sQuery(id+"F0.wireOp",EDGE,"E18.rect.bottom"),sQuery(id+"F0.wireOp",EDGE,"E18.rect.top"),sQuery(id+"F0.wireOp",EDGE,"E18.rect.left"),sQuery(id+"F0.wireOp",EDGE,"E18.rect.right"),sQuery(id+"F0.wireOp",EDGE,"E19.rect.left"),sQuery(id+"F0.wireOp",EDGE,"E19.rect.right"),sQuery(id+"F0.wireOp",EDGE,"E20.rect.bottom"),subQ0,sQuery(id+"F0.wireOp",EDGE,"E23.top"),sQuery(id+"F0.wireOp",EDGE,"E23.left"),sQuery(id+"F0.wireOp",EDGE,"E23.right"),sQuery(id+"F0.wireOp",EDGE,"E24.top"),sQuery(id+"F0.wireOp",EDGE,"E24.left"),sQuery(id+"F0.wireOp",EDGE,"E24.right"),sQuery(id+"F0.wireOp",EDGE,"E25.top"),sQuery(id+"F0.wireOp",EDGE,"E25.left"),sQuery(id+"F0.wireOp",EDGE,"E25.right"),sQuery(id+"F0.wireOp",EDGE,"E26.top"),sQuery(id+"F0.wireOp",EDGE,"E26.left"),sQuery(id+"F0.wireOp",EDGE,"E26.right")])],"isStart":true})]});}
            var Q23;
            {var subQ0=sQuery(id+"F0.wireOp",EDGE,"E20.rect.top");Q23=makeQuery(id+"F1.opExtrude","CAP_EDGE",EDGE,{"disambiguationData":[OSD([subQ0]),TDD([makeQuery(id+"F0.imprint","IMPRINT",EDGE,{"disambiguationData":[TD([[makeQuery(id+"F0.imprint","INTERSECT",VERTEX,{"derivedFrom":[sQuery(id+"F0.wireOp",EDGE,"E12"),subQ0]}),-1.0]])],"derivedFrom":subQ0})])],"isStart":true});}
            var Q24;
            {var subQ0=sQuery(id+"F0.wireOp",EDGE,"E20.rect.top");var subQ1=sQuery(id+"F0.wireOp",EDGE,"E12");Q24=makeQuery(id+"F3.opFillet","BLEND_EDGE",EDGE,{"blendedFrom":[makeQuery(id+"F1.opExtrude","SWEPT_EDGE",EDGE,{"disambiguationData":[OSD([subQ1,subQ0])]}),makeQuery(id+"F1.opExtrude","CAP_FACE",FACE,{"disambiguationData":[OSD([sQuery(id+"F0.wireOp",EDGE,"E0"),sQuery(id+"F0.wireOp",EDGE,"E1"),sQuery(id+"F0.wireOp",EDGE,"E2"),sQuery(id+"F0.wireOp",EDGE,"E3"),sQuery(id+"F0.wireOp",EDGE,"E4"),sQuery(id+"F0.wireOp",EDGE,"E5"),sQuery(id+"F0.wireOp",EDGE,"E6"),sQuery(id+"F0.wireOp",EDGE,"E7"),sQuery(id+"F0.wireOp",EDGE,"E8"),sQuery(id+"F0.wireOp",EDGE,"E9"),sQuery(id+"F0.wireOp",EDGE,"E10"),sQuery(id+"F0.wireOp",EDGE,"E11"),subQ1,sQuery(id+"F0.wireOp",EDGE,"E13"),sQuery(id+"F0.wireOp",EDGE,"E14"),sQuery(id+"F0.wireOp",EDGE,"E15"),sQuery(id+"F0.wireOp",EDGE,"E17.rect.bottom"),sQuery(id+"F0.wireOp",EDGE,"E17.rect.top"),sQuery(id+"F0.wireOp",EDGE,"E17.rect.left"),sQuery(id+"F0.wireOp",EDGE,"E17.rect.right"),sQuery(id+"F0.wireOp",EDGE,"E18.rect.bottom"),sQuery(id+"F0.wireOp",EDGE,"E18.rect.top"),sQuery(id+"F0.wireOp",EDGE,"E18.rect.left"),sQuery(id+"F0.wireOp",EDGE,"E18.rect.right"),sQuery(id+"F0.wireOp",EDGE,"E19.rect.left"),sQuery(id+"F0.wireOp",EDGE,"E19.rect.right"),sQuery(id+"F0.wireOp",EDGE,"E20.rect.bottom"),subQ0,sQuery(id+"F0.wireOp",EDGE,"E23.top"),sQuery(id+"F0.wireOp",EDGE,"E23.left"),sQuery(id+"F0.wireOp",EDGE,"E23.right"),sQuery(id+"F0.wireOp",EDGE,"E24.top"),sQuery(id+"F0.wireOp",EDGE,"E24.left"),sQuery(id+"F0.wireOp",EDGE,"E24.right"),sQuery(id+"F0.wireOp",EDGE,"E25.top"),sQuery(id+"F0.wireOp",EDGE,"E25.left"),sQuery(id+"F0.wireOp",EDGE,"E25.right"),sQuery(id+"F0.wireOp",EDGE,"E26.top"),sQuery(id+"F0.wireOp",EDGE,"E26.left"),sQuery(id+"F0.wireOp",EDGE,"E26.right")])],"isStart":true})],"blendedInto":[makeQuery(id+"F1.opExtrude","CAP_FACE",FACE,{"disambiguationData":[OSD([sQuery(id+"F0.wireOp",EDGE,"E0"),sQuery(id+"F0.wireOp",EDGE,"E1"),sQuery(id+"F0.wireOp",EDGE,"E2"),sQuery(id+"F0.wireOp",EDGE,"E3"),sQuery(id+"F0.wireOp",EDGE,"E4"),sQuery(id+"F0.wireOp",EDGE,"E5"),sQuery(id+"F0.wireOp",EDGE,"E6"),sQuery(id+"F0.wireOp",EDGE,"E7"),sQuery(id+"F0.wireOp",EDGE,"E8"),sQuery(id+"F0.wireOp",EDGE,"E9"),sQuery(id+"F0.wireOp",EDGE,"E10"),sQuery(id+"F0.wireOp",EDGE,"E11"),subQ1,sQuery(id+"F0.wireOp",EDGE,"E13"),sQuery(id+"F0.wireOp",EDGE,"E14"),sQuery(id+"F0.wireOp",EDGE,"E15"),sQuery(id+"F0.wireOp",EDGE,"E17.rect.bottom"),sQuery(id+"F0.wireOp",EDGE,"E17.rect.top"),sQuery(id+"F0.wireOp",EDGE,"E17.rect.left"),sQuery(id+"F0.wireOp",EDGE,"E17.rect.right"),sQuery(id+"F0.wireOp",EDGE,"E18.rect.bottom"),sQuery(id+"F0.wireOp",EDGE,"E18.rect.top"),sQuery(id+"F0.wireOp",EDGE,"E18.rect.left"),sQuery(id+"F0.wireOp",EDGE,"E18.rect.right"),sQuery(id+"F0.wireOp",EDGE,"E19.rect.left"),sQuery(id+"F0.wireOp",EDGE,"E19.rect.right"),sQuery(id+"F0.wireOp",EDGE,"E20.rect.bottom"),subQ0,sQuery(id+"F0.wireOp",EDGE,"E23.top"),sQuery(id+"F0.wireOp",EDGE,"E23.left"),sQuery(id+"F0.wireOp",EDGE,"E23.right"),sQuery(id+"F0.wireOp",EDGE,"E24.top"),sQuery(id+"F0.wireOp",EDGE,"E24.left"),sQuery(id+"F0.wireOp",EDGE,"E24.right"),sQuery(id+"F0.wireOp",EDGE,"E25.top"),sQuery(id+"F0.wireOp",EDGE,"E25.left"),sQuery(id+"F0.wireOp",EDGE,"E25.right"),sQuery(id+"F0.wireOp",EDGE,"E26.top"),sQuery(id+"F0.wireOp",EDGE,"E26.left"),sQuery(id+"F0.wireOp",EDGE,"E26.right")])],"isStart":true})]});}
            var Q25;
            {var subQ0=sQuery(id+"F0.wireOp",EDGE,"E12");var subQ1=makeQuery(id+"F0.imprint","INTERSECT",VERTEX,{"disambiguationData":[OD(0.0)],"derivedFrom":[sQuery(id+"F0.wireOp",EDGE,"E6"),subQ0]});Q25=makeQuery(id+"F1.opExtrude","CAP_EDGE",EDGE,{"disambiguationData":[OSD([subQ0]),TDD([makeQuery(id+"F0.imprint","IMPRINT",EDGE,{"disambiguationData":[TD([[subQ1,1.0]])],"derivedFrom":subQ0}),makeQuery(id+"F0.imprint","IMPRINT",EDGE,{"disambiguationData":[TD([[makeQuery(id+"F0.imprint","INTERSECT",VERTEX,{"disambiguationData":[OD(0.0)],"derivedFrom":[sQuery(id+"F0.wireOp",EDGE,"E2"),subQ0]}),1.0]])],"derivedFrom":subQ0})])],"isStart":true});}
            var Q26;
            {var subQ0=sQuery(id+"F0.wireOp",EDGE,"E14");var subQ1=makeQuery(id+"F0.imprint","INTERSECT",VERTEX,{"disambiguationData":[OD(0.0)],"derivedFrom":[sQuery(id+"F0.wireOp",EDGE,"E6"),subQ0]});Q26=makeQuery(id+"F1.opExtrude","CAP_EDGE",EDGE,{"disambiguationData":[OSD([subQ0]),TDD([makeQuery(id+"F0.imprint","IMPRINT",EDGE,{"disambiguationData":[TD([[makeQuery(id+"F0.imprint","INTERSECT",VERTEX,{"disambiguationData":[OD(0.0)],"derivedFrom":[sQuery(id+"F0.wireOp",EDGE,"E2"),subQ0]}),-1.0]])],"derivedFrom":subQ0}),makeQuery(id+"F0.imprint","IMPRINT",EDGE,{"disambiguationData":[TD([[subQ1,-1.0]])],"derivedFrom":subQ0})])],"isStart":true});}
            var Q27;
            {var subQ0=sQuery(id+"F0.wireOp",EDGE,"E19.rect.left");var subQ1=sQuery(id+"F0.wireOp",EDGE,"E14");Q27=makeQuery(id+"F3.opFillet","BLEND_EDGE",EDGE,{"blendedFrom":[makeQuery(id+"F1.opExtrude","SWEPT_EDGE",EDGE,{"disambiguationData":[OSD([subQ1,subQ0])]}),makeQuery(id+"F1.opExtrude","CAP_FACE",FACE,{"disambiguationData":[OSD([sQuery(id+"F0.wireOp",EDGE,"E0"),sQuery(id+"F0.wireOp",EDGE,"E1"),sQuery(id+"F0.wireOp",EDGE,"E2"),sQuery(id+"F0.wireOp",EDGE,"E3"),sQuery(id+"F0.wireOp",EDGE,"E4"),sQuery(id+"F0.wireOp",EDGE,"E5"),sQuery(id+"F0.wireOp",EDGE,"E6"),sQuery(id+"F0.wireOp",EDGE,"E7"),sQuery(id+"F0.wireOp",EDGE,"E8"),sQuery(id+"F0.wireOp",EDGE,"E9"),sQuery(id+"F0.wireOp",EDGE,"E10"),sQuery(id+"F0.wireOp",EDGE,"E11"),sQuery(id+"F0.wireOp",EDGE,"E12"),sQuery(id+"F0.wireOp",EDGE,"E13"),subQ1,sQuery(id+"F0.wireOp",EDGE,"E15"),sQuery(id+"F0.wireOp",EDGE,"E17.rect.bottom"),sQuery(id+"F0.wireOp",EDGE,"E17.rect.top"),sQuery(id+"F0.wireOp",EDGE,"E17.rect.left"),sQuery(id+"F0.wireOp",EDGE,"E17.rect.right"),sQuery(id+"F0.wireOp",EDGE,"E18.rect.bottom"),sQuery(id+"F0.wireOp",EDGE,"E18.rect.top"),sQuery(id+"F0.wireOp",EDGE,"E18.rect.left"),sQuery(id+"F0.wireOp",EDGE,"E18.rect.right"),subQ0,sQuery(id+"F0.wireOp",EDGE,"E19.rect.right"),sQuery(id+"F0.wireOp",EDGE,"E20.rect.bottom"),sQuery(id+"F0.wireOp",EDGE,"E20.rect.top"),sQuery(id+"F0.wireOp",EDGE,"E23.top"),sQuery(id+"F0.wireOp",EDGE,"E23.left"),sQuery(id+"F0.wireOp",EDGE,"E23.right"),sQuery(id+"F0.wireOp",EDGE,"E24.top"),sQuery(id+"F0.wireOp",EDGE,"E24.left"),sQuery(id+"F0.wireOp",EDGE,"E24.right"),sQuery(id+"F0.wireOp",EDGE,"E25.top"),sQuery(id+"F0.wireOp",EDGE,"E25.left"),sQuery(id+"F0.wireOp",EDGE,"E25.right"),sQuery(id+"F0.wireOp",EDGE,"E26.top"),sQuery(id+"F0.wireOp",EDGE,"E26.left"),sQuery(id+"F0.wireOp",EDGE,"E26.right")])],"isStart":true})],"blendedInto":[makeQuery(id+"F1.opExtrude","CAP_FACE",FACE,{"disambiguationData":[OSD([sQuery(id+"F0.wireOp",EDGE,"E0"),sQuery(id+"F0.wireOp",EDGE,"E1"),sQuery(id+"F0.wireOp",EDGE,"E2"),sQuery(id+"F0.wireOp",EDGE,"E3"),sQuery(id+"F0.wireOp",EDGE,"E4"),sQuery(id+"F0.wireOp",EDGE,"E5"),sQuery(id+"F0.wireOp",EDGE,"E6"),sQuery(id+"F0.wireOp",EDGE,"E7"),sQuery(id+"F0.wireOp",EDGE,"E8"),sQuery(id+"F0.wireOp",EDGE,"E9"),sQuery(id+"F0.wireOp",EDGE,"E10"),sQuery(id+"F0.wireOp",EDGE,"E11"),sQuery(id+"F0.wireOp",EDGE,"E12"),sQuery(id+"F0.wireOp",EDGE,"E13"),subQ1,sQuery(id+"F0.wireOp",EDGE,"E15"),sQuery(id+"F0.wireOp",EDGE,"E17.rect.bottom"),sQuery(id+"F0.wireOp",EDGE,"E17.rect.top"),sQuery(id+"F0.wireOp",EDGE,"E17.rect.left"),sQuery(id+"F0.wireOp",EDGE,"E17.rect.right"),sQuery(id+"F0.wireOp",EDGE,"E18.rect.bottom"),sQuery(id+"F0.wireOp",EDGE,"E18.rect.top"),sQuery(id+"F0.wireOp",EDGE,"E18.rect.left"),sQuery(id+"F0.wireOp",EDGE,"E18.rect.right"),subQ0,sQuery(id+"F0.wireOp",EDGE,"E19.rect.right"),sQuery(id+"F0.wireOp",EDGE,"E20.rect.bottom"),sQuery(id+"F0.wireOp",EDGE,"E20.rect.top"),sQuery(id+"F0.wireOp",EDGE,"E23.top"),sQuery(id+"F0.wireOp",EDGE,"E23.left"),sQuery(id+"F0.wireOp",EDGE,"E23.right"),sQuery(id+"F0.wireOp",EDGE,"E24.top"),sQuery(id+"F0.wireOp",EDGE,"E24.left"),sQuery(id+"F0.wireOp",EDGE,"E24.right"),sQuery(id+"F0.wireOp",EDGE,"E25.top"),sQuery(id+"F0.wireOp",EDGE,"E25.left"),sQuery(id+"F0.wireOp",EDGE,"E25.right"),sQuery(id+"F0.wireOp",EDGE,"E26.top"),sQuery(id+"F0.wireOp",EDGE,"E26.left"),sQuery(id+"F0.wireOp",EDGE,"E26.right")])],"isStart":true})]});}
            var Q28;
            {var subQ0=sQuery(id+"F0.wireOp",EDGE,"E19.rect.left");Q28=makeQuery(id+"F1.opExtrude","CAP_EDGE",EDGE,{"disambiguationData":[OSD([subQ0]),TDD([makeQuery(id+"F0.imprint","IMPRINT",EDGE,{"disambiguationData":[TD([[makeQuery(id+"F0.imprint","INTERSECT",VERTEX,{"derivedFrom":[sQuery(id+"F0.wireOp",EDGE,"E14"),subQ0]}),1.0]])],"derivedFrom":subQ0})])],"isStart":true});}
            var Q29;
            {var subQ0=sQuery(id+"F0.wireOp",EDGE,"E19.rect.left");var subQ1=sQuery(id+"F0.wireOp",EDGE,"E17.rect.top");Q29=makeQuery(id+"F3.opFillet","BLEND_EDGE",EDGE,{"blendedFrom":[makeQuery(id+"F1.opExtrude","SWEPT_EDGE",EDGE,{"disambiguationData":[OSD([subQ1,subQ0])]}),makeQuery(id+"F1.opExtrude","CAP_FACE",FACE,{"disambiguationData":[OSD([sQuery(id+"F0.wireOp",EDGE,"E0"),sQuery(id+"F0.wireOp",EDGE,"E1"),sQuery(id+"F0.wireOp",EDGE,"E2"),sQuery(id+"F0.wireOp",EDGE,"E3"),sQuery(id+"F0.wireOp",EDGE,"E4"),sQuery(id+"F0.wireOp",EDGE,"E5"),sQuery(id+"F0.wireOp",EDGE,"E6"),sQuery(id+"F0.wireOp",EDGE,"E7"),sQuery(id+"F0.wireOp",EDGE,"E8"),sQuery(id+"F0.wireOp",EDGE,"E9"),sQuery(id+"F0.wireOp",EDGE,"E10"),sQuery(id+"F0.wireOp",EDGE,"E11"),sQuery(id+"F0.wireOp",EDGE,"E12"),sQuery(id+"F0.wireOp",EDGE,"E13"),sQuery(id+"F0.wireOp",EDGE,"E14"),sQuery(id+"F0.wireOp",EDGE,"E15"),sQuery(id+"F0.wireOp",EDGE,"E17.rect.bottom"),subQ1,sQuery(id+"F0.wireOp",EDGE,"E17.rect.left"),sQuery(id+"F0.wireOp",EDGE,"E17.rect.right"),sQuery(id+"F0.wireOp",EDGE,"E18.rect.bottom"),sQuery(id+"F0.wireOp",EDGE,"E18.rect.top"),sQuery(id+"F0.wireOp",EDGE,"E18.rect.left"),sQuery(id+"F0.wireOp",EDGE,"E18.rect.right"),subQ0,sQuery(id+"F0.wireOp",EDGE,"E19.rect.right"),sQuery(id+"F0.wireOp",EDGE,"E20.rect.bottom"),sQuery(id+"F0.wireOp",EDGE,"E20.rect.top"),sQuery(id+"F0.wireOp",EDGE,"E23.top"),sQuery(id+"F0.wireOp",EDGE,"E23.left"),sQuery(id+"F0.wireOp",EDGE,"E23.right"),sQuery(id+"F0.wireOp",EDGE,"E24.top"),sQuery(id+"F0.wireOp",EDGE,"E24.left"),sQuery(id+"F0.wireOp",EDGE,"E24.right"),sQuery(id+"F0.wireOp",EDGE,"E25.top"),sQuery(id+"F0.wireOp",EDGE,"E25.left"),sQuery(id+"F0.wireOp",EDGE,"E25.right"),sQuery(id+"F0.wireOp",EDGE,"E26.top"),sQuery(id+"F0.wireOp",EDGE,"E26.left"),sQuery(id+"F0.wireOp",EDGE,"E26.right")])],"isStart":true})],"blendedInto":[makeQuery(id+"F1.opExtrude","CAP_FACE",FACE,{"disambiguationData":[OSD([sQuery(id+"F0.wireOp",EDGE,"E0"),sQuery(id+"F0.wireOp",EDGE,"E1"),sQuery(id+"F0.wireOp",EDGE,"E2"),sQuery(id+"F0.wireOp",EDGE,"E3"),sQuery(id+"F0.wireOp",EDGE,"E4"),sQuery(id+"F0.wireOp",EDGE,"E5"),sQuery(id+"F0.wireOp",EDGE,"E6"),sQuery(id+"F0.wireOp",EDGE,"E7"),sQuery(id+"F0.wireOp",EDGE,"E8"),sQuery(id+"F0.wireOp",EDGE,"E9"),sQuery(id+"F0.wireOp",EDGE,"E10"),sQuery(id+"F0.wireOp",EDGE,"E11"),sQuery(id+"F0.wireOp",EDGE,"E12"),sQuery(id+"F0.wireOp",EDGE,"E13"),sQuery(id+"F0.wireOp",EDGE,"E14"),sQuery(id+"F0.wireOp",EDGE,"E15"),sQuery(id+"F0.wireOp",EDGE,"E17.rect.bottom"),subQ1,sQuery(id+"F0.wireOp",EDGE,"E17.rect.left"),sQuery(id+"F0.wireOp",EDGE,"E17.rect.right"),sQuery(id+"F0.wireOp",EDGE,"E18.rect.bottom"),sQuery(id+"F0.wireOp",EDGE,"E18.rect.top"),sQuery(id+"F0.wireOp",EDGE,"E18.rect.left"),sQuery(id+"F0.wireOp",EDGE,"E18.rect.right"),subQ0,sQuery(id+"F0.wireOp",EDGE,"E19.rect.right"),sQuery(id+"F0.wireOp",EDGE,"E20.rect.bottom"),sQuery(id+"F0.wireOp",EDGE,"E20.rect.top"),sQuery(id+"F0.wireOp",EDGE,"E23.top"),sQuery(id+"F0.wireOp",EDGE,"E23.left"),sQuery(id+"F0.wireOp",EDGE,"E23.right"),sQuery(id+"F0.wireOp",EDGE,"E24.top"),sQuery(id+"F0.wireOp",EDGE,"E24.left"),sQuery(id+"F0.wireOp",EDGE,"E24.right"),sQuery(id+"F0.wireOp",EDGE,"E25.top"),sQuery(id+"F0.wireOp",EDGE,"E25.left"),sQuery(id+"F0.wireOp",EDGE,"E25.right"),sQuery(id+"F0.wireOp",EDGE,"E26.top"),sQuery(id+"F0.wireOp",EDGE,"E26.left"),sQuery(id+"F0.wireOp",EDGE,"E26.right")])],"isStart":true})]});}
            var Q30;
            {var subQ0=sQuery(id+"F0.wireOp",EDGE,"E17.rect.top");Q30=makeQuery(id+"F1.opExtrude","CAP_EDGE",EDGE,{"disambiguationData":[OSD([subQ0]),TDD([makeQuery(id+"F0.imprint","IMPRINT",EDGE,{"disambiguationData":[TD([[makeQuery(id+"F0.imprint","INTERSECT",VERTEX,{"derivedFrom":[subQ0,sQuery(id+"F0.wireOp",EDGE,"E19.rect.left")]}),1.0]])],"derivedFrom":subQ0})])],"isStart":true});}
            var Q31;
            {var subQ0=sQuery(id+"F0.wireOp",EDGE,"E17.rect.top");Q31=makeQuery(id+"F1.opExtrude","CAP_EDGE",EDGE,{"disambiguationData":[OSD([subQ0]),TDD([makeQuery(id+"F0.imprint","IMPRINT",EDGE,{"disambiguationData":[TD([[makeQuery(id+"F0.imprint","INTERSECT",VERTEX,{"derivedFrom":[subQ0,sQuery(id+"F0.wireOp",EDGE,"E19.rect.right")]}),-1.0]])],"derivedFrom":subQ0})])],"isStart":true});}
            var Q32;
            {var subQ0=sQuery(id+"F0.wireOp",EDGE,"E19.rect.right");var subQ1=sQuery(id+"F0.wireOp",EDGE,"E17.rect.top");Q32=makeQuery(id+"F3.opFillet","BLEND_EDGE",EDGE,{"blendedFrom":[makeQuery(id+"F1.opExtrude","SWEPT_EDGE",EDGE,{"disambiguationData":[OSD([subQ1,subQ0])]}),makeQuery(id+"F1.opExtrude","CAP_FACE",FACE,{"disambiguationData":[OSD([sQuery(id+"F0.wireOp",EDGE,"E0"),sQuery(id+"F0.wireOp",EDGE,"E1"),sQuery(id+"F0.wireOp",EDGE,"E2"),sQuery(id+"F0.wireOp",EDGE,"E3"),sQuery(id+"F0.wireOp",EDGE,"E4"),sQuery(id+"F0.wireOp",EDGE,"E5"),sQuery(id+"F0.wireOp",EDGE,"E6"),sQuery(id+"F0.wireOp",EDGE,"E7"),sQuery(id+"F0.wireOp",EDGE,"E8"),sQuery(id+"F0.wireOp",EDGE,"E9"),sQuery(id+"F0.wireOp",EDGE,"E10"),sQuery(id+"F0.wireOp",EDGE,"E11"),sQuery(id+"F0.wireOp",EDGE,"E12"),sQuery(id+"F0.wireOp",EDGE,"E13"),sQuery(id+"F0.wireOp",EDGE,"E14"),sQuery(id+"F0.wireOp",EDGE,"E15"),sQuery(id+"F0.wireOp",EDGE,"E17.rect.bottom"),subQ1,sQuery(id+"F0.wireOp",EDGE,"E17.rect.left"),sQuery(id+"F0.wireOp",EDGE,"E17.rect.right"),sQuery(id+"F0.wireOp",EDGE,"E18.rect.bottom"),sQuery(id+"F0.wireOp",EDGE,"E18.rect.top"),sQuery(id+"F0.wireOp",EDGE,"E18.rect.left"),sQuery(id+"F0.wireOp",EDGE,"E18.rect.right"),sQuery(id+"F0.wireOp",EDGE,"E19.rect.left"),subQ0,sQuery(id+"F0.wireOp",EDGE,"E20.rect.bottom"),sQuery(id+"F0.wireOp",EDGE,"E20.rect.top"),sQuery(id+"F0.wireOp",EDGE,"E23.top"),sQuery(id+"F0.wireOp",EDGE,"E23.left"),sQuery(id+"F0.wireOp",EDGE,"E23.right"),sQuery(id+"F0.wireOp",EDGE,"E24.top"),sQuery(id+"F0.wireOp",EDGE,"E24.left"),sQuery(id+"F0.wireOp",EDGE,"E24.right"),sQuery(id+"F0.wireOp",EDGE,"E25.top"),sQuery(id+"F0.wireOp",EDGE,"E25.left"),sQuery(id+"F0.wireOp",EDGE,"E25.right"),sQuery(id+"F0.wireOp",EDGE,"E26.top"),sQuery(id+"F0.wireOp",EDGE,"E26.left"),sQuery(id+"F0.wireOp",EDGE,"E26.right")])],"isStart":true})],"blendedInto":[makeQuery(id+"F1.opExtrude","CAP_FACE",FACE,{"disambiguationData":[OSD([sQuery(id+"F0.wireOp",EDGE,"E0"),sQuery(id+"F0.wireOp",EDGE,"E1"),sQuery(id+"F0.wireOp",EDGE,"E2"),sQuery(id+"F0.wireOp",EDGE,"E3"),sQuery(id+"F0.wireOp",EDGE,"E4"),sQuery(id+"F0.wireOp",EDGE,"E5"),sQuery(id+"F0.wireOp",EDGE,"E6"),sQuery(id+"F0.wireOp",EDGE,"E7"),sQuery(id+"F0.wireOp",EDGE,"E8"),sQuery(id+"F0.wireOp",EDGE,"E9"),sQuery(id+"F0.wireOp",EDGE,"E10"),sQuery(id+"F0.wireOp",EDGE,"E11"),sQuery(id+"F0.wireOp",EDGE,"E12"),sQuery(id+"F0.wireOp",EDGE,"E13"),sQuery(id+"F0.wireOp",EDGE,"E14"),sQuery(id+"F0.wireOp",EDGE,"E15"),sQuery(id+"F0.wireOp",EDGE,"E17.rect.bottom"),subQ1,sQuery(id+"F0.wireOp",EDGE,"E17.rect.left"),sQuery(id+"F0.wireOp",EDGE,"E17.rect.right"),sQuery(id+"F0.wireOp",EDGE,"E18.rect.bottom"),sQuery(id+"F0.wireOp",EDGE,"E18.rect.top"),sQuery(id+"F0.wireOp",EDGE,"E18.rect.left"),sQuery(id+"F0.wireOp",EDGE,"E18.rect.right"),sQuery(id+"F0.wireOp",EDGE,"E19.rect.left"),subQ0,sQuery(id+"F0.wireOp",EDGE,"E20.rect.bottom"),sQuery(id+"F0.wireOp",EDGE,"E20.rect.top"),sQuery(id+"F0.wireOp",EDGE,"E23.top"),sQuery(id+"F0.wireOp",EDGE,"E23.left"),sQuery(id+"F0.wireOp",EDGE,"E23.right"),sQuery(id+"F0.wireOp",EDGE,"E24.top"),sQuery(id+"F0.wireOp",EDGE,"E24.left"),sQuery(id+"F0.wireOp",EDGE,"E24.right"),sQuery(id+"F0.wireOp",EDGE,"E25.top"),sQuery(id+"F0.wireOp",EDGE,"E25.left"),sQuery(id+"F0.wireOp",EDGE,"E25.right"),sQuery(id+"F0.wireOp",EDGE,"E26.top"),sQuery(id+"F0.wireOp",EDGE,"E26.left"),sQuery(id+"F0.wireOp",EDGE,"E26.right")])],"isStart":true})]});}
            var Q33;
            {var subQ0=sQuery(id+"F0.wireOp",EDGE,"E19.rect.right");Q33=makeQuery(id+"F1.opExtrude","CAP_EDGE",EDGE,{"disambiguationData":[OSD([subQ0]),TDD([makeQuery(id+"F0.imprint","IMPRINT",EDGE,{"disambiguationData":[TD([[makeQuery(id+"F0.imprint","INTERSECT",VERTEX,{"derivedFrom":[sQuery(id+"F0.wireOp",EDGE,"E14"),subQ0]}),1.0]])],"derivedFrom":subQ0})])],"isStart":true});}
            var Q34;
            {var subQ0=sQuery(id+"F0.wireOp",EDGE,"E19.rect.right");var subQ1=sQuery(id+"F0.wireOp",EDGE,"E14");Q34=makeQuery(id+"F3.opFillet","BLEND_EDGE",EDGE,{"blendedFrom":[makeQuery(id+"F1.opExtrude","SWEPT_EDGE",EDGE,{"disambiguationData":[OSD([subQ1,subQ0])]}),makeQuery(id+"F1.opExtrude","CAP_FACE",FACE,{"disambiguationData":[OSD([sQuery(id+"F0.wireOp",EDGE,"E0"),sQuery(id+"F0.wireOp",EDGE,"E1"),sQuery(id+"F0.wireOp",EDGE,"E2"),sQuery(id+"F0.wireOp",EDGE,"E3"),sQuery(id+"F0.wireOp",EDGE,"E4"),sQuery(id+"F0.wireOp",EDGE,"E5"),sQuery(id+"F0.wireOp",EDGE,"E6"),sQuery(id+"F0.wireOp",EDGE,"E7"),sQuery(id+"F0.wireOp",EDGE,"E8"),sQuery(id+"F0.wireOp",EDGE,"E9"),sQuery(id+"F0.wireOp",EDGE,"E10"),sQuery(id+"F0.wireOp",EDGE,"E11"),sQuery(id+"F0.wireOp",EDGE,"E12"),sQuery(id+"F0.wireOp",EDGE,"E13"),subQ1,sQuery(id+"F0.wireOp",EDGE,"E15"),sQuery(id+"F0.wireOp",EDGE,"E17.rect.bottom"),sQuery(id+"F0.wireOp",EDGE,"E17.rect.top"),sQuery(id+"F0.wireOp",EDGE,"E17.rect.left"),sQuery(id+"F0.wireOp",EDGE,"E17.rect.right"),sQuery(id+"F0.wireOp",EDGE,"E18.rect.bottom"),sQuery(id+"F0.wireOp",EDGE,"E18.rect.top"),sQuery(id+"F0.wireOp",EDGE,"E18.rect.left"),sQuery(id+"F0.wireOp",EDGE,"E18.rect.right"),sQuery(id+"F0.wireOp",EDGE,"E19.rect.left"),subQ0,sQuery(id+"F0.wireOp",EDGE,"E20.rect.bottom"),sQuery(id+"F0.wireOp",EDGE,"E20.rect.top"),sQuery(id+"F0.wireOp",EDGE,"E23.top"),sQuery(id+"F0.wireOp",EDGE,"E23.left"),sQuery(id+"F0.wireOp",EDGE,"E23.right"),sQuery(id+"F0.wireOp",EDGE,"E24.top"),sQuery(id+"F0.wireOp",EDGE,"E24.left"),sQuery(id+"F0.wireOp",EDGE,"E24.right"),sQuery(id+"F0.wireOp",EDGE,"E25.top"),sQuery(id+"F0.wireOp",EDGE,"E25.left"),sQuery(id+"F0.wireOp",EDGE,"E25.right"),sQuery(id+"F0.wireOp",EDGE,"E26.top"),sQuery(id+"F0.wireOp",EDGE,"E26.left"),sQuery(id+"F0.wireOp",EDGE,"E26.right")])],"isStart":true})],"blendedInto":[makeQuery(id+"F1.opExtrude","CAP_FACE",FACE,{"disambiguationData":[OSD([sQuery(id+"F0.wireOp",EDGE,"E0"),sQuery(id+"F0.wireOp",EDGE,"E1"),sQuery(id+"F0.wireOp",EDGE,"E2"),sQuery(id+"F0.wireOp",EDGE,"E3"),sQuery(id+"F0.wireOp",EDGE,"E4"),sQuery(id+"F0.wireOp",EDGE,"E5"),sQuery(id+"F0.wireOp",EDGE,"E6"),sQuery(id+"F0.wireOp",EDGE,"E7"),sQuery(id+"F0.wireOp",EDGE,"E8"),sQuery(id+"F0.wireOp",EDGE,"E9"),sQuery(id+"F0.wireOp",EDGE,"E10"),sQuery(id+"F0.wireOp",EDGE,"E11"),sQuery(id+"F0.wireOp",EDGE,"E12"),sQuery(id+"F0.wireOp",EDGE,"E13"),subQ1,sQuery(id+"F0.wireOp",EDGE,"E15"),sQuery(id+"F0.wireOp",EDGE,"E17.rect.bottom"),sQuery(id+"F0.wireOp",EDGE,"E17.rect.top"),sQuery(id+"F0.wireOp",EDGE,"E17.rect.left"),sQuery(id+"F0.wireOp",EDGE,"E17.rect.right"),sQuery(id+"F0.wireOp",EDGE,"E18.rect.bottom"),sQuery(id+"F0.wireOp",EDGE,"E18.rect.top"),sQuery(id+"F0.wireOp",EDGE,"E18.rect.left"),sQuery(id+"F0.wireOp",EDGE,"E18.rect.right"),sQuery(id+"F0.wireOp",EDGE,"E19.rect.left"),subQ0,sQuery(id+"F0.wireOp",EDGE,"E20.rect.bottom"),sQuery(id+"F0.wireOp",EDGE,"E20.rect.top"),sQuery(id+"F0.wireOp",EDGE,"E23.top"),sQuery(id+"F0.wireOp",EDGE,"E23.left"),sQuery(id+"F0.wireOp",EDGE,"E23.right"),sQuery(id+"F0.wireOp",EDGE,"E24.top"),sQuery(id+"F0.wireOp",EDGE,"E24.left"),sQuery(id+"F0.wireOp",EDGE,"E24.right"),sQuery(id+"F0.wireOp",EDGE,"E25.top"),sQuery(id+"F0.wireOp",EDGE,"E25.left"),sQuery(id+"F0.wireOp",EDGE,"E25.right"),sQuery(id+"F0.wireOp",EDGE,"E26.top"),sQuery(id+"F0.wireOp",EDGE,"E26.left"),sQuery(id+"F0.wireOp",EDGE,"E26.right")])],"isStart":true})]});}
            var Q35;
            Q35=makeQuery(id+"F1.opExtrude","CAP_EDGE",EDGE,{"disambiguationData":[OSD([sQuery(id+"F0.wireOp",EDGE,"E18.rect.top")])],"isStart":true});
            var Q36;
            {var subQ0=sQuery(id+"F0.wireOp",EDGE,"E18.rect.left");var subQ1=sQuery(id+"F0.wireOp",EDGE,"E18.rect.top");Q36=makeQuery(id+"F3.opFillet","BLEND_EDGE",EDGE,{"blendedFrom":[makeQuery(id+"F1.opExtrude","SWEPT_EDGE",EDGE,{"disambiguationData":[OSD([subQ1,subQ0])]}),makeQuery(id+"F1.opExtrude","CAP_FACE",FACE,{"disambiguationData":[OSD([sQuery(id+"F0.wireOp",EDGE,"E0"),sQuery(id+"F0.wireOp",EDGE,"E1"),sQuery(id+"F0.wireOp",EDGE,"E2"),sQuery(id+"F0.wireOp",EDGE,"E3"),sQuery(id+"F0.wireOp",EDGE,"E4"),sQuery(id+"F0.wireOp",EDGE,"E5"),sQuery(id+"F0.wireOp",EDGE,"E6"),sQuery(id+"F0.wireOp",EDGE,"E7"),sQuery(id+"F0.wireOp",EDGE,"E8"),sQuery(id+"F0.wireOp",EDGE,"E9"),sQuery(id+"F0.wireOp",EDGE,"E10"),sQuery(id+"F0.wireOp",EDGE,"E11"),sQuery(id+"F0.wireOp",EDGE,"E12"),sQuery(id+"F0.wireOp",EDGE,"E13"),sQuery(id+"F0.wireOp",EDGE,"E14"),sQuery(id+"F0.wireOp",EDGE,"E15"),sQuery(id+"F0.wireOp",EDGE,"E17.rect.bottom"),sQuery(id+"F0.wireOp",EDGE,"E17.rect.top"),sQuery(id+"F0.wireOp",EDGE,"E17.rect.left"),sQuery(id+"F0.wireOp",EDGE,"E17.rect.right"),sQuery(id+"F0.wireOp",EDGE,"E18.rect.bottom"),subQ1,subQ0,sQuery(id+"F0.wireOp",EDGE,"E18.rect.right"),sQuery(id+"F0.wireOp",EDGE,"E19.rect.left"),sQuery(id+"F0.wireOp",EDGE,"E19.rect.right"),sQuery(id+"F0.wireOp",EDGE,"E20.rect.bottom"),sQuery(id+"F0.wireOp",EDGE,"E20.rect.top"),sQuery(id+"F0.wireOp",EDGE,"E23.top"),sQuery(id+"F0.wireOp",EDGE,"E23.left"),sQuery(id+"F0.wireOp",EDGE,"E23.right"),sQuery(id+"F0.wireOp",EDGE,"E24.top"),sQuery(id+"F0.wireOp",EDGE,"E24.left"),sQuery(id+"F0.wireOp",EDGE,"E24.right"),sQuery(id+"F0.wireOp",EDGE,"E25.top"),sQuery(id+"F0.wireOp",EDGE,"E25.left"),sQuery(id+"F0.wireOp",EDGE,"E25.right"),sQuery(id+"F0.wireOp",EDGE,"E26.top"),sQuery(id+"F0.wireOp",EDGE,"E26.left"),sQuery(id+"F0.wireOp",EDGE,"E26.right")])],"isStart":true})],"blendedInto":[makeQuery(id+"F1.opExtrude","CAP_FACE",FACE,{"disambiguationData":[OSD([sQuery(id+"F0.wireOp",EDGE,"E0"),sQuery(id+"F0.wireOp",EDGE,"E1"),sQuery(id+"F0.wireOp",EDGE,"E2"),sQuery(id+"F0.wireOp",EDGE,"E3"),sQuery(id+"F0.wireOp",EDGE,"E4"),sQuery(id+"F0.wireOp",EDGE,"E5"),sQuery(id+"F0.wireOp",EDGE,"E6"),sQuery(id+"F0.wireOp",EDGE,"E7"),sQuery(id+"F0.wireOp",EDGE,"E8"),sQuery(id+"F0.wireOp",EDGE,"E9"),sQuery(id+"F0.wireOp",EDGE,"E10"),sQuery(id+"F0.wireOp",EDGE,"E11"),sQuery(id+"F0.wireOp",EDGE,"E12"),sQuery(id+"F0.wireOp",EDGE,"E13"),sQuery(id+"F0.wireOp",EDGE,"E14"),sQuery(id+"F0.wireOp",EDGE,"E15"),sQuery(id+"F0.wireOp",EDGE,"E17.rect.bottom"),sQuery(id+"F0.wireOp",EDGE,"E17.rect.top"),sQuery(id+"F0.wireOp",EDGE,"E17.rect.left"),sQuery(id+"F0.wireOp",EDGE,"E17.rect.right"),sQuery(id+"F0.wireOp",EDGE,"E18.rect.bottom"),subQ1,subQ0,sQuery(id+"F0.wireOp",EDGE,"E18.rect.right"),sQuery(id+"F0.wireOp",EDGE,"E19.rect.left"),sQuery(id+"F0.wireOp",EDGE,"E19.rect.right"),sQuery(id+"F0.wireOp",EDGE,"E20.rect.bottom"),sQuery(id+"F0.wireOp",EDGE,"E20.rect.top"),sQuery(id+"F0.wireOp",EDGE,"E23.top"),sQuery(id+"F0.wireOp",EDGE,"E23.left"),sQuery(id+"F0.wireOp",EDGE,"E23.right"),sQuery(id+"F0.wireOp",EDGE,"E24.top"),sQuery(id+"F0.wireOp",EDGE,"E24.left"),sQuery(id+"F0.wireOp",EDGE,"E24.right"),sQuery(id+"F0.wireOp",EDGE,"E25.top"),sQuery(id+"F0.wireOp",EDGE,"E25.left"),sQuery(id+"F0.wireOp",EDGE,"E25.right"),sQuery(id+"F0.wireOp",EDGE,"E26.top"),sQuery(id+"F0.wireOp",EDGE,"E26.left"),sQuery(id+"F0.wireOp",EDGE,"E26.right")])],"isStart":true})]});}
            var Q37;
            Q37=makeQuery(id+"F1.opExtrude","CAP_EDGE",EDGE,{"disambiguationData":[OSD([sQuery(id+"F0.wireOp",EDGE,"E18.rect.left")])],"isStart":true});
            var Q38;
            {var subQ0=sQuery(id+"F0.wireOp",EDGE,"E18.rect.left");var subQ1=sQuery(id+"F0.wireOp",EDGE,"E18.rect.bottom");Q38=makeQuery(id+"F3.opFillet","BLEND_EDGE",EDGE,{"blendedFrom":[makeQuery(id+"F1.opExtrude","SWEPT_EDGE",EDGE,{"disambiguationData":[OSD([subQ1,subQ0])]}),makeQuery(id+"F1.opExtrude","CAP_FACE",FACE,{"disambiguationData":[OSD([sQuery(id+"F0.wireOp",EDGE,"E0"),sQuery(id+"F0.wireOp",EDGE,"E1"),sQuery(id+"F0.wireOp",EDGE,"E2"),sQuery(id+"F0.wireOp",EDGE,"E3"),sQuery(id+"F0.wireOp",EDGE,"E4"),sQuery(id+"F0.wireOp",EDGE,"E5"),sQuery(id+"F0.wireOp",EDGE,"E6"),sQuery(id+"F0.wireOp",EDGE,"E7"),sQuery(id+"F0.wireOp",EDGE,"E8"),sQuery(id+"F0.wireOp",EDGE,"E9"),sQuery(id+"F0.wireOp",EDGE,"E10"),sQuery(id+"F0.wireOp",EDGE,"E11"),sQuery(id+"F0.wireOp",EDGE,"E12"),sQuery(id+"F0.wireOp",EDGE,"E13"),sQuery(id+"F0.wireOp",EDGE,"E14"),sQuery(id+"F0.wireOp",EDGE,"E15"),sQuery(id+"F0.wireOp",EDGE,"E17.rect.bottom"),sQuery(id+"F0.wireOp",EDGE,"E17.rect.top"),sQuery(id+"F0.wireOp",EDGE,"E17.rect.left"),sQuery(id+"F0.wireOp",EDGE,"E17.rect.right"),subQ1,sQuery(id+"F0.wireOp",EDGE,"E18.rect.top"),subQ0,sQuery(id+"F0.wireOp",EDGE,"E18.rect.right"),sQuery(id+"F0.wireOp",EDGE,"E19.rect.left"),sQuery(id+"F0.wireOp",EDGE,"E19.rect.right"),sQuery(id+"F0.wireOp",EDGE,"E20.rect.bottom"),sQuery(id+"F0.wireOp",EDGE,"E20.rect.top"),sQuery(id+"F0.wireOp",EDGE,"E23.top"),sQuery(id+"F0.wireOp",EDGE,"E23.left"),sQuery(id+"F0.wireOp",EDGE,"E23.right"),sQuery(id+"F0.wireOp",EDGE,"E24.top"),sQuery(id+"F0.wireOp",EDGE,"E24.left"),sQuery(id+"F0.wireOp",EDGE,"E24.right"),sQuery(id+"F0.wireOp",EDGE,"E25.top"),sQuery(id+"F0.wireOp",EDGE,"E25.left"),sQuery(id+"F0.wireOp",EDGE,"E25.right"),sQuery(id+"F0.wireOp",EDGE,"E26.top"),sQuery(id+"F0.wireOp",EDGE,"E26.left"),sQuery(id+"F0.wireOp",EDGE,"E26.right")])],"isStart":true})],"blendedInto":[makeQuery(id+"F1.opExtrude","CAP_FACE",FACE,{"disambiguationData":[OSD([sQuery(id+"F0.wireOp",EDGE,"E0"),sQuery(id+"F0.wireOp",EDGE,"E1"),sQuery(id+"F0.wireOp",EDGE,"E2"),sQuery(id+"F0.wireOp",EDGE,"E3"),sQuery(id+"F0.wireOp",EDGE,"E4"),sQuery(id+"F0.wireOp",EDGE,"E5"),sQuery(id+"F0.wireOp",EDGE,"E6"),sQuery(id+"F0.wireOp",EDGE,"E7"),sQuery(id+"F0.wireOp",EDGE,"E8"),sQuery(id+"F0.wireOp",EDGE,"E9"),sQuery(id+"F0.wireOp",EDGE,"E10"),sQuery(id+"F0.wireOp",EDGE,"E11"),sQuery(id+"F0.wireOp",EDGE,"E12"),sQuery(id+"F0.wireOp",EDGE,"E13"),sQuery(id+"F0.wireOp",EDGE,"E14"),sQuery(id+"F0.wireOp",EDGE,"E15"),sQuery(id+"F0.wireOp",EDGE,"E17.rect.bottom"),sQuery(id+"F0.wireOp",EDGE,"E17.rect.top"),sQuery(id+"F0.wireOp",EDGE,"E17.rect.left"),sQuery(id+"F0.wireOp",EDGE,"E17.rect.right"),subQ1,sQuery(id+"F0.wireOp",EDGE,"E18.rect.top"),subQ0,sQuery(id+"F0.wireOp",EDGE,"E18.rect.right"),sQuery(id+"F0.wireOp",EDGE,"E19.rect.left"),sQuery(id+"F0.wireOp",EDGE,"E19.rect.right"),sQuery(id+"F0.wireOp",EDGE,"E20.rect.bottom"),sQuery(id+"F0.wireOp",EDGE,"E20.rect.top"),sQuery(id+"F0.wireOp",EDGE,"E23.top"),sQuery(id+"F0.wireOp",EDGE,"E23.left"),sQuery(id+"F0.wireOp",EDGE,"E23.right"),sQuery(id+"F0.wireOp",EDGE,"E24.top"),sQuery(id+"F0.wireOp",EDGE,"E24.left"),sQuery(id+"F0.wireOp",EDGE,"E24.right"),sQuery(id+"F0.wireOp",EDGE,"E25.top"),sQuery(id+"F0.wireOp",EDGE,"E25.left"),sQuery(id+"F0.wireOp",EDGE,"E25.right"),sQuery(id+"F0.wireOp",EDGE,"E26.top"),sQuery(id+"F0.wireOp",EDGE,"E26.left"),sQuery(id+"F0.wireOp",EDGE,"E26.right")])],"isStart":true})]});}
            var Q39;
            Q39=makeQuery(id+"F1.opExtrude","CAP_EDGE",EDGE,{"disambiguationData":[OSD([sQuery(id+"F0.wireOp",EDGE,"E18.rect.bottom")])],"isStart":true});
            var Q40;
            {var subQ0=sQuery(id+"F0.wireOp",EDGE,"E18.rect.right");var subQ1=sQuery(id+"F0.wireOp",EDGE,"E18.rect.bottom");Q40=makeQuery(id+"F3.opFillet","BLEND_EDGE",EDGE,{"blendedFrom":[makeQuery(id+"F1.opExtrude","SWEPT_EDGE",EDGE,{"disambiguationData":[OSD([subQ1,subQ0])]}),makeQuery(id+"F1.opExtrude","CAP_FACE",FACE,{"disambiguationData":[OSD([sQuery(id+"F0.wireOp",EDGE,"E0"),sQuery(id+"F0.wireOp",EDGE,"E1"),sQuery(id+"F0.wireOp",EDGE,"E2"),sQuery(id+"F0.wireOp",EDGE,"E3"),sQuery(id+"F0.wireOp",EDGE,"E4"),sQuery(id+"F0.wireOp",EDGE,"E5"),sQuery(id+"F0.wireOp",EDGE,"E6"),sQuery(id+"F0.wireOp",EDGE,"E7"),sQuery(id+"F0.wireOp",EDGE,"E8"),sQuery(id+"F0.wireOp",EDGE,"E9"),sQuery(id+"F0.wireOp",EDGE,"E10"),sQuery(id+"F0.wireOp",EDGE,"E11"),sQuery(id+"F0.wireOp",EDGE,"E12"),sQuery(id+"F0.wireOp",EDGE,"E13"),sQuery(id+"F0.wireOp",EDGE,"E14"),sQuery(id+"F0.wireOp",EDGE,"E15"),sQuery(id+"F0.wireOp",EDGE,"E17.rect.bottom"),sQuery(id+"F0.wireOp",EDGE,"E17.rect.top"),sQuery(id+"F0.wireOp",EDGE,"E17.rect.left"),sQuery(id+"F0.wireOp",EDGE,"E17.rect.right"),subQ1,sQuery(id+"F0.wireOp",EDGE,"E18.rect.top"),sQuery(id+"F0.wireOp",EDGE,"E18.rect.left"),subQ0,sQuery(id+"F0.wireOp",EDGE,"E19.rect.left"),sQuery(id+"F0.wireOp",EDGE,"E19.rect.right"),sQuery(id+"F0.wireOp",EDGE,"E20.rect.bottom"),sQuery(id+"F0.wireOp",EDGE,"E20.rect.top"),sQuery(id+"F0.wireOp",EDGE,"E23.top"),sQuery(id+"F0.wireOp",EDGE,"E23.left"),sQuery(id+"F0.wireOp",EDGE,"E23.right"),sQuery(id+"F0.wireOp",EDGE,"E24.top"),sQuery(id+"F0.wireOp",EDGE,"E24.left"),sQuery(id+"F0.wireOp",EDGE,"E24.right"),sQuery(id+"F0.wireOp",EDGE,"E25.top"),sQuery(id+"F0.wireOp",EDGE,"E25.left"),sQuery(id+"F0.wireOp",EDGE,"E25.right"),sQuery(id+"F0.wireOp",EDGE,"E26.top"),sQuery(id+"F0.wireOp",EDGE,"E26.left"),sQuery(id+"F0.wireOp",EDGE,"E26.right")])],"isStart":true})],"blendedInto":[makeQuery(id+"F1.opExtrude","CAP_FACE",FACE,{"disambiguationData":[OSD([sQuery(id+"F0.wireOp",EDGE,"E0"),sQuery(id+"F0.wireOp",EDGE,"E1"),sQuery(id+"F0.wireOp",EDGE,"E2"),sQuery(id+"F0.wireOp",EDGE,"E3"),sQuery(id+"F0.wireOp",EDGE,"E4"),sQuery(id+"F0.wireOp",EDGE,"E5"),sQuery(id+"F0.wireOp",EDGE,"E6"),sQuery(id+"F0.wireOp",EDGE,"E7"),sQuery(id+"F0.wireOp",EDGE,"E8"),sQuery(id+"F0.wireOp",EDGE,"E9"),sQuery(id+"F0.wireOp",EDGE,"E10"),sQuery(id+"F0.wireOp",EDGE,"E11"),sQuery(id+"F0.wireOp",EDGE,"E12"),sQuery(id+"F0.wireOp",EDGE,"E13"),sQuery(id+"F0.wireOp",EDGE,"E14"),sQuery(id+"F0.wireOp",EDGE,"E15"),sQuery(id+"F0.wireOp",EDGE,"E17.rect.bottom"),sQuery(id+"F0.wireOp",EDGE,"E17.rect.top"),sQuery(id+"F0.wireOp",EDGE,"E17.rect.left"),sQuery(id+"F0.wireOp",EDGE,"E17.rect.right"),subQ1,sQuery(id+"F0.wireOp",EDGE,"E18.rect.top"),sQuery(id+"F0.wireOp",EDGE,"E18.rect.left"),subQ0,sQuery(id+"F0.wireOp",EDGE,"E19.rect.left"),sQuery(id+"F0.wireOp",EDGE,"E19.rect.right"),sQuery(id+"F0.wireOp",EDGE,"E20.rect.bottom"),sQuery(id+"F0.wireOp",EDGE,"E20.rect.top"),sQuery(id+"F0.wireOp",EDGE,"E23.top"),sQuery(id+"F0.wireOp",EDGE,"E23.left"),sQuery(id+"F0.wireOp",EDGE,"E23.right"),sQuery(id+"F0.wireOp",EDGE,"E24.top"),sQuery(id+"F0.wireOp",EDGE,"E24.left"),sQuery(id+"F0.wireOp",EDGE,"E24.right"),sQuery(id+"F0.wireOp",EDGE,"E25.top"),sQuery(id+"F0.wireOp",EDGE,"E25.left"),sQuery(id+"F0.wireOp",EDGE,"E25.right"),sQuery(id+"F0.wireOp",EDGE,"E26.top"),sQuery(id+"F0.wireOp",EDGE,"E26.left"),sQuery(id+"F0.wireOp",EDGE,"E26.right")])],"isStart":true})]});}
            var Q41;
            Q41=makeQuery(id+"F1.opExtrude","CAP_EDGE",EDGE,{"disambiguationData":[OSD([sQuery(id+"F0.wireOp",EDGE,"E18.rect.right")])],"isStart":true});
            var Q42;
            {var subQ0=sQuery(id+"F0.wireOp",EDGE,"E18.rect.right");var subQ1=sQuery(id+"F0.wireOp",EDGE,"E18.rect.top");Q42=makeQuery(id+"F3.opFillet","BLEND_EDGE",EDGE,{"blendedFrom":[makeQuery(id+"F1.opExtrude","SWEPT_EDGE",EDGE,{"disambiguationData":[OSD([subQ1,subQ0])]}),makeQuery(id+"F1.opExtrude","CAP_FACE",FACE,{"disambiguationData":[OSD([sQuery(id+"F0.wireOp",EDGE,"E0"),sQuery(id+"F0.wireOp",EDGE,"E1"),sQuery(id+"F0.wireOp",EDGE,"E2"),sQuery(id+"F0.wireOp",EDGE,"E3"),sQuery(id+"F0.wireOp",EDGE,"E4"),sQuery(id+"F0.wireOp",EDGE,"E5"),sQuery(id+"F0.wireOp",EDGE,"E6"),sQuery(id+"F0.wireOp",EDGE,"E7"),sQuery(id+"F0.wireOp",EDGE,"E8"),sQuery(id+"F0.wireOp",EDGE,"E9"),sQuery(id+"F0.wireOp",EDGE,"E10"),sQuery(id+"F0.wireOp",EDGE,"E11"),sQuery(id+"F0.wireOp",EDGE,"E12"),sQuery(id+"F0.wireOp",EDGE,"E13"),sQuery(id+"F0.wireOp",EDGE,"E14"),sQuery(id+"F0.wireOp",EDGE,"E15"),sQuery(id+"F0.wireOp",EDGE,"E17.rect.bottom"),sQuery(id+"F0.wireOp",EDGE,"E17.rect.top"),sQuery(id+"F0.wireOp",EDGE,"E17.rect.left"),sQuery(id+"F0.wireOp",EDGE,"E17.rect.right"),sQuery(id+"F0.wireOp",EDGE,"E18.rect.bottom"),subQ1,sQuery(id+"F0.wireOp",EDGE,"E18.rect.left"),subQ0,sQuery(id+"F0.wireOp",EDGE,"E19.rect.left"),sQuery(id+"F0.wireOp",EDGE,"E19.rect.right"),sQuery(id+"F0.wireOp",EDGE,"E20.rect.bottom"),sQuery(id+"F0.wireOp",EDGE,"E20.rect.top"),sQuery(id+"F0.wireOp",EDGE,"E23.top"),sQuery(id+"F0.wireOp",EDGE,"E23.left"),sQuery(id+"F0.wireOp",EDGE,"E23.right"),sQuery(id+"F0.wireOp",EDGE,"E24.top"),sQuery(id+"F0.wireOp",EDGE,"E24.left"),sQuery(id+"F0.wireOp",EDGE,"E24.right"),sQuery(id+"F0.wireOp",EDGE,"E25.top"),sQuery(id+"F0.wireOp",EDGE,"E25.left"),sQuery(id+"F0.wireOp",EDGE,"E25.right"),sQuery(id+"F0.wireOp",EDGE,"E26.top"),sQuery(id+"F0.wireOp",EDGE,"E26.left"),sQuery(id+"F0.wireOp",EDGE,"E26.right")])],"isStart":true})],"blendedInto":[makeQuery(id+"F1.opExtrude","CAP_FACE",FACE,{"disambiguationData":[OSD([sQuery(id+"F0.wireOp",EDGE,"E0"),sQuery(id+"F0.wireOp",EDGE,"E1"),sQuery(id+"F0.wireOp",EDGE,"E2"),sQuery(id+"F0.wireOp",EDGE,"E3"),sQuery(id+"F0.wireOp",EDGE,"E4"),sQuery(id+"F0.wireOp",EDGE,"E5"),sQuery(id+"F0.wireOp",EDGE,"E6"),sQuery(id+"F0.wireOp",EDGE,"E7"),sQuery(id+"F0.wireOp",EDGE,"E8"),sQuery(id+"F0.wireOp",EDGE,"E9"),sQuery(id+"F0.wireOp",EDGE,"E10"),sQuery(id+"F0.wireOp",EDGE,"E11"),sQuery(id+"F0.wireOp",EDGE,"E12"),sQuery(id+"F0.wireOp",EDGE,"E13"),sQuery(id+"F0.wireOp",EDGE,"E14"),sQuery(id+"F0.wireOp",EDGE,"E15"),sQuery(id+"F0.wireOp",EDGE,"E17.rect.bottom"),sQuery(id+"F0.wireOp",EDGE,"E17.rect.top"),sQuery(id+"F0.wireOp",EDGE,"E17.rect.left"),sQuery(id+"F0.wireOp",EDGE,"E17.rect.right"),sQuery(id+"F0.wireOp",EDGE,"E18.rect.bottom"),subQ1,sQuery(id+"F0.wireOp",EDGE,"E18.rect.left"),subQ0,sQuery(id+"F0.wireOp",EDGE,"E19.rect.left"),sQuery(id+"F0.wireOp",EDGE,"E19.rect.right"),sQuery(id+"F0.wireOp",EDGE,"E20.rect.bottom"),sQuery(id+"F0.wireOp",EDGE,"E20.rect.top"),sQuery(id+"F0.wireOp",EDGE,"E23.top"),sQuery(id+"F0.wireOp",EDGE,"E23.left"),sQuery(id+"F0.wireOp",EDGE,"E23.right"),sQuery(id+"F0.wireOp",EDGE,"E24.top"),sQuery(id+"F0.wireOp",EDGE,"E24.left"),sQuery(id+"F0.wireOp",EDGE,"E24.right"),sQuery(id+"F0.wireOp",EDGE,"E25.top"),sQuery(id+"F0.wireOp",EDGE,"E25.left"),sQuery(id+"F0.wireOp",EDGE,"E25.right"),sQuery(id+"F0.wireOp",EDGE,"E26.top"),sQuery(id+"F0.wireOp",EDGE,"E26.left"),sQuery(id+"F0.wireOp",EDGE,"E26.right")])],"isStart":true})]});}
            var Q43;
            Q43=makeQuery(id+"F1.opExtrude","CAP_EDGE",EDGE,{"disambiguationData":[OSD([sQuery(id+"F0.wireOp",EDGE,"E17.rect.right"),sQuery(id+"F0.wireOp",EDGE,"E23.left")])],"isStart":true});
            var Q44;
            Q44=makeQuery(id+"F1.opExtrude","CAP_EDGE",EDGE,{"disambiguationData":[OSD([sQuery(id+"F0.wireOp",EDGE,"E17.rect.right"),sQuery(id+"F0.wireOp",EDGE,"E24.left")])],"isStart":true});
            var Q45;
            Q45=makeQuery(id+"F1.opExtrude","CAP_EDGE",EDGE,{"disambiguationData":[OSD([sQuery(id+"F0.wireOp",EDGE,"E24.right")])],"isStart":true});
            var Q46;
            Q46=makeQuery(id+"F1.opExtrude","CAP_EDGE",EDGE,{"disambiguationData":[OSD([sQuery(id+"F0.wireOp",EDGE,"E23.right")])],"isStart":true});
            var Q47;
            Q47=makeQuery(id+"F1.opExtrude","CAP_EDGE",EDGE,{"disambiguationData":[OSD([sQuery(id+"F0.wireOp",EDGE,"E26.right")])],"isStart":true});
            var Q48;
            Q48=makeQuery(id+"F1.opExtrude","CAP_EDGE",EDGE,{"disambiguationData":[OSD([sQuery(id+"F0.wireOp",EDGE,"E25.right")])],"isStart":true});
            var Q49;
            Q49=makeQuery(id+"F1.opExtrude","CAP_EDGE",EDGE,{"disambiguationData":[OSD([sQuery(id+"F0.wireOp",EDGE,"E17.rect.left"),sQuery(id+"F0.wireOp",EDGE,"E26.left")])],"isStart":true});
            var Q50;
            Q50=makeQuery(id+"F1.opExtrude","CAP_EDGE",EDGE,{"disambiguationData":[OSD([sQuery(id+"F0.wireOp",EDGE,"E17.rect.left"),sQuery(id+"F0.wireOp",EDGE,"E25.left")])],"isStart":true});
            var Q51;
            {var subQ0=sQuery(id+"F0.wireOp",EDGE,"E14");var subQ1=makeQuery(id+"F0.imprint","INTERSECT",VERTEX,{"disambiguationData":[OD(0.0)],"derivedFrom":[sQuery(id+"F0.wireOp",EDGE,"E5"),subQ0]});Q51=makeQuery(id+"F1.opExtrude","CAP_EDGE",EDGE,{"disambiguationData":[OSD([subQ0]),TDD([makeQuery(id+"F0.imprint","IMPRINT",EDGE,{"disambiguationData":[TD([[subQ1,1.0]])],"derivedFrom":subQ0}),makeQuery(id+"F0.imprint","IMPRINT",EDGE,{"disambiguationData":[TD([[makeQuery(id+"F0.imprint","INTERSECT",VERTEX,{"disambiguationData":[OD(1.0)],"derivedFrom":[sQuery(id+"F0.wireOp",EDGE,"E3"),subQ0]}),1.0]])],"derivedFrom":subQ0})])],"isStart":true});}
            var Q52;
            {var subQ0=sQuery(id+"F0.wireOp",EDGE,"E14");var subQ1=makeQuery(id+"F0.imprint","INTERSECT",VERTEX,{"disambiguationData":[OD(0.0)],"derivedFrom":[sQuery(id+"F0.wireOp",EDGE,"E6"),subQ0]});Q52=makeQuery(id+"F1.opExtrude","CAP_EDGE",EDGE,{"disambiguationData":[OSD([subQ0]),TDD([makeQuery(id+"F0.imprint","IMPRINT",EDGE,{"disambiguationData":[TD([[makeQuery(id+"F0.imprint","INTERSECT",VERTEX,{"disambiguationData":[OD(0.0)],"derivedFrom":[sQuery(id+"F0.wireOp",EDGE,"E2"),subQ0]}),-1.0]])],"derivedFrom":subQ0}),makeQuery(id+"F0.imprint","IMPRINT",EDGE,{"disambiguationData":[TD([[subQ1,-1.0]])],"derivedFrom":subQ0})])],"isStart":false});}
            var Q53;
            {var subQ0=sQuery(id+"F0.wireOp",EDGE,"E19.rect.left");var subQ1=sQuery(id+"F0.wireOp",EDGE,"E14");Q53=makeQuery(id+"F3.opFillet","BLEND_EDGE",EDGE,{"blendedFrom":[makeQuery(id+"F1.opExtrude","SWEPT_EDGE",EDGE,{"disambiguationData":[OSD([subQ1,subQ0])]}),makeQuery(id+"F1.opExtrude","CAP_FACE",FACE,{"disambiguationData":[OSD([sQuery(id+"F0.wireOp",EDGE,"E0"),sQuery(id+"F0.wireOp",EDGE,"E1"),sQuery(id+"F0.wireOp",EDGE,"E2"),sQuery(id+"F0.wireOp",EDGE,"E3"),sQuery(id+"F0.wireOp",EDGE,"E4"),sQuery(id+"F0.wireOp",EDGE,"E5"),sQuery(id+"F0.wireOp",EDGE,"E6"),sQuery(id+"F0.wireOp",EDGE,"E7"),sQuery(id+"F0.wireOp",EDGE,"E8"),sQuery(id+"F0.wireOp",EDGE,"E9"),sQuery(id+"F0.wireOp",EDGE,"E10"),sQuery(id+"F0.wireOp",EDGE,"E11"),sQuery(id+"F0.wireOp",EDGE,"E12"),sQuery(id+"F0.wireOp",EDGE,"E13"),subQ1,sQuery(id+"F0.wireOp",EDGE,"E15"),sQuery(id+"F0.wireOp",EDGE,"E17.rect.bottom"),sQuery(id+"F0.wireOp",EDGE,"E17.rect.top"),sQuery(id+"F0.wireOp",EDGE,"E17.rect.left"),sQuery(id+"F0.wireOp",EDGE,"E17.rect.right"),sQuery(id+"F0.wireOp",EDGE,"E18.rect.bottom"),sQuery(id+"F0.wireOp",EDGE,"E18.rect.top"),sQuery(id+"F0.wireOp",EDGE,"E18.rect.left"),sQuery(id+"F0.wireOp",EDGE,"E18.rect.right"),subQ0,sQuery(id+"F0.wireOp",EDGE,"E19.rect.right"),sQuery(id+"F0.wireOp",EDGE,"E20.rect.bottom"),sQuery(id+"F0.wireOp",EDGE,"E20.rect.top"),sQuery(id+"F0.wireOp",EDGE,"E23.top"),sQuery(id+"F0.wireOp",EDGE,"E23.left"),sQuery(id+"F0.wireOp",EDGE,"E23.right"),sQuery(id+"F0.wireOp",EDGE,"E24.top"),sQuery(id+"F0.wireOp",EDGE,"E24.left"),sQuery(id+"F0.wireOp",EDGE,"E24.right"),sQuery(id+"F0.wireOp",EDGE,"E25.top"),sQuery(id+"F0.wireOp",EDGE,"E25.left"),sQuery(id+"F0.wireOp",EDGE,"E25.right"),sQuery(id+"F0.wireOp",EDGE,"E26.top"),sQuery(id+"F0.wireOp",EDGE,"E26.left"),sQuery(id+"F0.wireOp",EDGE,"E26.right")])],"isStart":false})],"blendedInto":[makeQuery(id+"F1.opExtrude","CAP_FACE",FACE,{"disambiguationData":[OSD([sQuery(id+"F0.wireOp",EDGE,"E0"),sQuery(id+"F0.wireOp",EDGE,"E1"),sQuery(id+"F0.wireOp",EDGE,"E2"),sQuery(id+"F0.wireOp",EDGE,"E3"),sQuery(id+"F0.wireOp",EDGE,"E4"),sQuery(id+"F0.wireOp",EDGE,"E5"),sQuery(id+"F0.wireOp",EDGE,"E6"),sQuery(id+"F0.wireOp",EDGE,"E7"),sQuery(id+"F0.wireOp",EDGE,"E8"),sQuery(id+"F0.wireOp",EDGE,"E9"),sQuery(id+"F0.wireOp",EDGE,"E10"),sQuery(id+"F0.wireOp",EDGE,"E11"),sQuery(id+"F0.wireOp",EDGE,"E12"),sQuery(id+"F0.wireOp",EDGE,"E13"),subQ1,sQuery(id+"F0.wireOp",EDGE,"E15"),sQuery(id+"F0.wireOp",EDGE,"E17.rect.bottom"),sQuery(id+"F0.wireOp",EDGE,"E17.rect.top"),sQuery(id+"F0.wireOp",EDGE,"E17.rect.left"),sQuery(id+"F0.wireOp",EDGE,"E17.rect.right"),sQuery(id+"F0.wireOp",EDGE,"E18.rect.bottom"),sQuery(id+"F0.wireOp",EDGE,"E18.rect.top"),sQuery(id+"F0.wireOp",EDGE,"E18.rect.left"),sQuery(id+"F0.wireOp",EDGE,"E18.rect.right"),subQ0,sQuery(id+"F0.wireOp",EDGE,"E19.rect.right"),sQuery(id+"F0.wireOp",EDGE,"E20.rect.bottom"),sQuery(id+"F0.wireOp",EDGE,"E20.rect.top"),sQuery(id+"F0.wireOp",EDGE,"E23.top"),sQuery(id+"F0.wireOp",EDGE,"E23.left"),sQuery(id+"F0.wireOp",EDGE,"E23.right"),sQuery(id+"F0.wireOp",EDGE,"E24.top"),sQuery(id+"F0.wireOp",EDGE,"E24.left"),sQuery(id+"F0.wireOp",EDGE,"E24.right"),sQuery(id+"F0.wireOp",EDGE,"E25.top"),sQuery(id+"F0.wireOp",EDGE,"E25.left"),sQuery(id+"F0.wireOp",EDGE,"E25.right"),sQuery(id+"F0.wireOp",EDGE,"E26.top"),sQuery(id+"F0.wireOp",EDGE,"E26.left"),sQuery(id+"F0.wireOp",EDGE,"E26.right")])],"isStart":false})]});}
            var Q54;
            {var subQ0=sQuery(id+"F0.wireOp",EDGE,"E19.rect.left");Q54=makeQuery(id+"F1.opExtrude","CAP_EDGE",EDGE,{"disambiguationData":[OSD([subQ0]),TDD([makeQuery(id+"F0.imprint","IMPRINT",EDGE,{"disambiguationData":[TD([[makeQuery(id+"F0.imprint","INTERSECT",VERTEX,{"derivedFrom":[sQuery(id+"F0.wireOp",EDGE,"E14"),subQ0]}),1.0]])],"derivedFrom":subQ0})])],"isStart":false});}
            var Q55;
            {var subQ0=sQuery(id+"F0.wireOp",EDGE,"E19.rect.left");var subQ1=sQuery(id+"F0.wireOp",EDGE,"E17.rect.top");Q55=makeQuery(id+"F3.opFillet","BLEND_EDGE",EDGE,{"blendedFrom":[makeQuery(id+"F1.opExtrude","SWEPT_EDGE",EDGE,{"disambiguationData":[OSD([subQ1,subQ0])]}),makeQuery(id+"F1.opExtrude","CAP_FACE",FACE,{"disambiguationData":[OSD([sQuery(id+"F0.wireOp",EDGE,"E0"),sQuery(id+"F0.wireOp",EDGE,"E1"),sQuery(id+"F0.wireOp",EDGE,"E2"),sQuery(id+"F0.wireOp",EDGE,"E3"),sQuery(id+"F0.wireOp",EDGE,"E4"),sQuery(id+"F0.wireOp",EDGE,"E5"),sQuery(id+"F0.wireOp",EDGE,"E6"),sQuery(id+"F0.wireOp",EDGE,"E7"),sQuery(id+"F0.wireOp",EDGE,"E8"),sQuery(id+"F0.wireOp",EDGE,"E9"),sQuery(id+"F0.wireOp",EDGE,"E10"),sQuery(id+"F0.wireOp",EDGE,"E11"),sQuery(id+"F0.wireOp",EDGE,"E12"),sQuery(id+"F0.wireOp",EDGE,"E13"),sQuery(id+"F0.wireOp",EDGE,"E14"),sQuery(id+"F0.wireOp",EDGE,"E15"),sQuery(id+"F0.wireOp",EDGE,"E17.rect.bottom"),subQ1,sQuery(id+"F0.wireOp",EDGE,"E17.rect.left"),sQuery(id+"F0.wireOp",EDGE,"E17.rect.right"),sQuery(id+"F0.wireOp",EDGE,"E18.rect.bottom"),sQuery(id+"F0.wireOp",EDGE,"E18.rect.top"),sQuery(id+"F0.wireOp",EDGE,"E18.rect.left"),sQuery(id+"F0.wireOp",EDGE,"E18.rect.right"),subQ0,sQuery(id+"F0.wireOp",EDGE,"E19.rect.right"),sQuery(id+"F0.wireOp",EDGE,"E20.rect.bottom"),sQuery(id+"F0.wireOp",EDGE,"E20.rect.top"),sQuery(id+"F0.wireOp",EDGE,"E23.top"),sQuery(id+"F0.wireOp",EDGE,"E23.left"),sQuery(id+"F0.wireOp",EDGE,"E23.right"),sQuery(id+"F0.wireOp",EDGE,"E24.top"),sQuery(id+"F0.wireOp",EDGE,"E24.left"),sQuery(id+"F0.wireOp",EDGE,"E24.right"),sQuery(id+"F0.wireOp",EDGE,"E25.top"),sQuery(id+"F0.wireOp",EDGE,"E25.left"),sQuery(id+"F0.wireOp",EDGE,"E25.right"),sQuery(id+"F0.wireOp",EDGE,"E26.top"),sQuery(id+"F0.wireOp",EDGE,"E26.left"),sQuery(id+"F0.wireOp",EDGE,"E26.right")])],"isStart":false})],"blendedInto":[makeQuery(id+"F1.opExtrude","CAP_FACE",FACE,{"disambiguationData":[OSD([sQuery(id+"F0.wireOp",EDGE,"E0"),sQuery(id+"F0.wireOp",EDGE,"E1"),sQuery(id+"F0.wireOp",EDGE,"E2"),sQuery(id+"F0.wireOp",EDGE,"E3"),sQuery(id+"F0.wireOp",EDGE,"E4"),sQuery(id+"F0.wireOp",EDGE,"E5"),sQuery(id+"F0.wireOp",EDGE,"E6"),sQuery(id+"F0.wireOp",EDGE,"E7"),sQuery(id+"F0.wireOp",EDGE,"E8"),sQuery(id+"F0.wireOp",EDGE,"E9"),sQuery(id+"F0.wireOp",EDGE,"E10"),sQuery(id+"F0.wireOp",EDGE,"E11"),sQuery(id+"F0.wireOp",EDGE,"E12"),sQuery(id+"F0.wireOp",EDGE,"E13"),sQuery(id+"F0.wireOp",EDGE,"E14"),sQuery(id+"F0.wireOp",EDGE,"E15"),sQuery(id+"F0.wireOp",EDGE,"E17.rect.bottom"),subQ1,sQuery(id+"F0.wireOp",EDGE,"E17.rect.left"),sQuery(id+"F0.wireOp",EDGE,"E17.rect.right"),sQuery(id+"F0.wireOp",EDGE,"E18.rect.bottom"),sQuery(id+"F0.wireOp",EDGE,"E18.rect.top"),sQuery(id+"F0.wireOp",EDGE,"E18.rect.left"),sQuery(id+"F0.wireOp",EDGE,"E18.rect.right"),subQ0,sQuery(id+"F0.wireOp",EDGE,"E19.rect.right"),sQuery(id+"F0.wireOp",EDGE,"E20.rect.bottom"),sQuery(id+"F0.wireOp",EDGE,"E20.rect.top"),sQuery(id+"F0.wireOp",EDGE,"E23.top"),sQuery(id+"F0.wireOp",EDGE,"E23.left"),sQuery(id+"F0.wireOp",EDGE,"E23.right"),sQuery(id+"F0.wireOp",EDGE,"E24.top"),sQuery(id+"F0.wireOp",EDGE,"E24.left"),sQuery(id+"F0.wireOp",EDGE,"E24.right"),sQuery(id+"F0.wireOp",EDGE,"E25.top"),sQuery(id+"F0.wireOp",EDGE,"E25.left"),sQuery(id+"F0.wireOp",EDGE,"E25.right"),sQuery(id+"F0.wireOp",EDGE,"E26.top"),sQuery(id+"F0.wireOp",EDGE,"E26.left"),sQuery(id+"F0.wireOp",EDGE,"E26.right")])],"isStart":false})]});}
            var Q56;
            {var subQ0=sQuery(id+"F0.wireOp",EDGE,"E17.rect.top");Q56=makeQuery(id+"F1.opExtrude","CAP_EDGE",EDGE,{"disambiguationData":[OSD([subQ0]),TDD([makeQuery(id+"F0.imprint","IMPRINT",EDGE,{"disambiguationData":[TD([[makeQuery(id+"F0.imprint","INTERSECT",VERTEX,{"derivedFrom":[subQ0,sQuery(id+"F0.wireOp",EDGE,"E19.rect.left")]}),1.0]])],"derivedFrom":subQ0})])],"isStart":false});}
            var Q57;
            Q57=makeQuery(id+"F1.opExtrude","CAP_EDGE",EDGE,{"disambiguationData":[OSD([sQuery(id+"F0.wireOp",EDGE,"E25.right")])],"isStart":false});
            var Q58;
            Q58=makeQuery(id+"F1.opExtrude","CAP_EDGE",EDGE,{"disambiguationData":[OSD([sQuery(id+"F0.wireOp",EDGE,"E17.rect.left"),sQuery(id+"F0.wireOp",EDGE,"E25.left")])],"isStart":false});
            var Q59;
            {var subQ0=sQuery(id+"F0.wireOp",EDGE,"E20.rect.top");var subQ1=sQuery(id+"F0.wireOp",EDGE,"E17.rect.left");Q59=makeQuery(id+"F3.opFillet","BLEND_EDGE",EDGE,{"blendedFrom":[makeQuery(id+"F1.opExtrude","SWEPT_EDGE",EDGE,{"disambiguationData":[OSD([subQ1,subQ0])]}),makeQuery(id+"F1.opExtrude","CAP_FACE",FACE,{"disambiguationData":[OSD([sQuery(id+"F0.wireOp",EDGE,"E0"),sQuery(id+"F0.wireOp",EDGE,"E1"),sQuery(id+"F0.wireOp",EDGE,"E2"),sQuery(id+"F0.wireOp",EDGE,"E3"),sQuery(id+"F0.wireOp",EDGE,"E4"),sQuery(id+"F0.wireOp",EDGE,"E5"),sQuery(id+"F0.wireOp",EDGE,"E6"),sQuery(id+"F0.wireOp",EDGE,"E7"),sQuery(id+"F0.wireOp",EDGE,"E8"),sQuery(id+"F0.wireOp",EDGE,"E9"),sQuery(id+"F0.wireOp",EDGE,"E10"),sQuery(id+"F0.wireOp",EDGE,"E11"),sQuery(id+"F0.wireOp",EDGE,"E12"),sQuery(id+"F0.wireOp",EDGE,"E13"),sQuery(id+"F0.wireOp",EDGE,"E14"),sQuery(id+"F0.wireOp",EDGE,"E15"),sQuery(id+"F0.wireOp",EDGE,"E17.rect.bottom"),sQuery(id+"F0.wireOp",EDGE,"E17.rect.top"),subQ1,sQuery(id+"F0.wireOp",EDGE,"E17.rect.right"),sQuery(id+"F0.wireOp",EDGE,"E18.rect.bottom"),sQuery(id+"F0.wireOp",EDGE,"E18.rect.top"),sQuery(id+"F0.wireOp",EDGE,"E18.rect.left"),sQuery(id+"F0.wireOp",EDGE,"E18.rect.right"),sQuery(id+"F0.wireOp",EDGE,"E19.rect.left"),sQuery(id+"F0.wireOp",EDGE,"E19.rect.right"),sQuery(id+"F0.wireOp",EDGE,"E20.rect.bottom"),subQ0,sQuery(id+"F0.wireOp",EDGE,"E23.top"),sQuery(id+"F0.wireOp",EDGE,"E23.left"),sQuery(id+"F0.wireOp",EDGE,"E23.right"),sQuery(id+"F0.wireOp",EDGE,"E24.top"),sQuery(id+"F0.wireOp",EDGE,"E24.left"),sQuery(id+"F0.wireOp",EDGE,"E24.right"),sQuery(id+"F0.wireOp",EDGE,"E25.top"),sQuery(id+"F0.wireOp",EDGE,"E25.left"),sQuery(id+"F0.wireOp",EDGE,"E25.right"),sQuery(id+"F0.wireOp",EDGE,"E26.top"),sQuery(id+"F0.wireOp",EDGE,"E26.left"),sQuery(id+"F0.wireOp",EDGE,"E26.right")])],"isStart":false})],"blendedInto":[makeQuery(id+"F1.opExtrude","CAP_FACE",FACE,{"disambiguationData":[OSD([sQuery(id+"F0.wireOp",EDGE,"E0"),sQuery(id+"F0.wireOp",EDGE,"E1"),sQuery(id+"F0.wireOp",EDGE,"E2"),sQuery(id+"F0.wireOp",EDGE,"E3"),sQuery(id+"F0.wireOp",EDGE,"E4"),sQuery(id+"F0.wireOp",EDGE,"E5"),sQuery(id+"F0.wireOp",EDGE,"E6"),sQuery(id+"F0.wireOp",EDGE,"E7"),sQuery(id+"F0.wireOp",EDGE,"E8"),sQuery(id+"F0.wireOp",EDGE,"E9"),sQuery(id+"F0.wireOp",EDGE,"E10"),sQuery(id+"F0.wireOp",EDGE,"E11"),sQuery(id+"F0.wireOp",EDGE,"E12"),sQuery(id+"F0.wireOp",EDGE,"E13"),sQuery(id+"F0.wireOp",EDGE,"E14"),sQuery(id+"F0.wireOp",EDGE,"E15"),sQuery(id+"F0.wireOp",EDGE,"E17.rect.bottom"),sQuery(id+"F0.wireOp",EDGE,"E17.rect.top"),subQ1,sQuery(id+"F0.wireOp",EDGE,"E17.rect.right"),sQuery(id+"F0.wireOp",EDGE,"E18.rect.bottom"),sQuery(id+"F0.wireOp",EDGE,"E18.rect.top"),sQuery(id+"F0.wireOp",EDGE,"E18.rect.left"),sQuery(id+"F0.wireOp",EDGE,"E18.rect.right"),sQuery(id+"F0.wireOp",EDGE,"E19.rect.left"),sQuery(id+"F0.wireOp",EDGE,"E19.rect.right"),sQuery(id+"F0.wireOp",EDGE,"E20.rect.bottom"),subQ0,sQuery(id+"F0.wireOp",EDGE,"E23.top"),sQuery(id+"F0.wireOp",EDGE,"E23.left"),sQuery(id+"F0.wireOp",EDGE,"E23.right"),sQuery(id+"F0.wireOp",EDGE,"E24.top"),sQuery(id+"F0.wireOp",EDGE,"E24.left"),sQuery(id+"F0.wireOp",EDGE,"E24.right"),sQuery(id+"F0.wireOp",EDGE,"E25.top"),sQuery(id+"F0.wireOp",EDGE,"E25.left"),sQuery(id+"F0.wireOp",EDGE,"E25.right"),sQuery(id+"F0.wireOp",EDGE,"E26.top"),sQuery(id+"F0.wireOp",EDGE,"E26.left"),sQuery(id+"F0.wireOp",EDGE,"E26.right")])],"isStart":false})]});}
            var Q60;
            {var subQ0=sQuery(id+"F0.wireOp",EDGE,"E20.rect.top");Q60=makeQuery(id+"F1.opExtrude","CAP_EDGE",EDGE,{"disambiguationData":[OSD([subQ0]),TDD([makeQuery(id+"F0.imprint","IMPRINT",EDGE,{"disambiguationData":[TD([[makeQuery(id+"F0.imprint","INTERSECT",VERTEX,{"derivedFrom":[sQuery(id+"F0.wireOp",EDGE,"E12"),subQ0]}),-1.0]])],"derivedFrom":subQ0})])],"isStart":false});}
            var Q61;
            {var subQ0=sQuery(id+"F0.wireOp",EDGE,"E20.rect.top");var subQ1=sQuery(id+"F0.wireOp",EDGE,"E12");Q61=makeQuery(id+"F3.opFillet","BLEND_EDGE",EDGE,{"blendedFrom":[makeQuery(id+"F1.opExtrude","SWEPT_EDGE",EDGE,{"disambiguationData":[OSD([subQ1,subQ0])]}),makeQuery(id+"F1.opExtrude","CAP_FACE",FACE,{"disambiguationData":[OSD([sQuery(id+"F0.wireOp",EDGE,"E0"),sQuery(id+"F0.wireOp",EDGE,"E1"),sQuery(id+"F0.wireOp",EDGE,"E2"),sQuery(id+"F0.wireOp",EDGE,"E3"),sQuery(id+"F0.wireOp",EDGE,"E4"),sQuery(id+"F0.wireOp",EDGE,"E5"),sQuery(id+"F0.wireOp",EDGE,"E6"),sQuery(id+"F0.wireOp",EDGE,"E7"),sQuery(id+"F0.wireOp",EDGE,"E8"),sQuery(id+"F0.wireOp",EDGE,"E9"),sQuery(id+"F0.wireOp",EDGE,"E10"),sQuery(id+"F0.wireOp",EDGE,"E11"),subQ1,sQuery(id+"F0.wireOp",EDGE,"E13"),sQuery(id+"F0.wireOp",EDGE,"E14"),sQuery(id+"F0.wireOp",EDGE,"E15"),sQuery(id+"F0.wireOp",EDGE,"E17.rect.bottom"),sQuery(id+"F0.wireOp",EDGE,"E17.rect.top"),sQuery(id+"F0.wireOp",EDGE,"E17.rect.left"),sQuery(id+"F0.wireOp",EDGE,"E17.rect.right"),sQuery(id+"F0.wireOp",EDGE,"E18.rect.bottom"),sQuery(id+"F0.wireOp",EDGE,"E18.rect.top"),sQuery(id+"F0.wireOp",EDGE,"E18.rect.left"),sQuery(id+"F0.wireOp",EDGE,"E18.rect.right"),sQuery(id+"F0.wireOp",EDGE,"E19.rect.left"),sQuery(id+"F0.wireOp",EDGE,"E19.rect.right"),sQuery(id+"F0.wireOp",EDGE,"E20.rect.bottom"),subQ0,sQuery(id+"F0.wireOp",EDGE,"E23.top"),sQuery(id+"F0.wireOp",EDGE,"E23.left"),sQuery(id+"F0.wireOp",EDGE,"E23.right"),sQuery(id+"F0.wireOp",EDGE,"E24.top"),sQuery(id+"F0.wireOp",EDGE,"E24.left"),sQuery(id+"F0.wireOp",EDGE,"E24.right"),sQuery(id+"F0.wireOp",EDGE,"E25.top"),sQuery(id+"F0.wireOp",EDGE,"E25.left"),sQuery(id+"F0.wireOp",EDGE,"E25.right"),sQuery(id+"F0.wireOp",EDGE,"E26.top"),sQuery(id+"F0.wireOp",EDGE,"E26.left"),sQuery(id+"F0.wireOp",EDGE,"E26.right")])],"isStart":false})],"blendedInto":[makeQuery(id+"F1.opExtrude","CAP_FACE",FACE,{"disambiguationData":[OSD([sQuery(id+"F0.wireOp",EDGE,"E0"),sQuery(id+"F0.wireOp",EDGE,"E1"),sQuery(id+"F0.wireOp",EDGE,"E2"),sQuery(id+"F0.wireOp",EDGE,"E3"),sQuery(id+"F0.wireOp",EDGE,"E4"),sQuery(id+"F0.wireOp",EDGE,"E5"),sQuery(id+"F0.wireOp",EDGE,"E6"),sQuery(id+"F0.wireOp",EDGE,"E7"),sQuery(id+"F0.wireOp",EDGE,"E8"),sQuery(id+"F0.wireOp",EDGE,"E9"),sQuery(id+"F0.wireOp",EDGE,"E10"),sQuery(id+"F0.wireOp",EDGE,"E11"),subQ1,sQuery(id+"F0.wireOp",EDGE,"E13"),sQuery(id+"F0.wireOp",EDGE,"E14"),sQuery(id+"F0.wireOp",EDGE,"E15"),sQuery(id+"F0.wireOp",EDGE,"E17.rect.bottom"),sQuery(id+"F0.wireOp",EDGE,"E17.rect.top"),sQuery(id+"F0.wireOp",EDGE,"E17.rect.left"),sQuery(id+"F0.wireOp",EDGE,"E17.rect.right"),sQuery(id+"F0.wireOp",EDGE,"E18.rect.bottom"),sQuery(id+"F0.wireOp",EDGE,"E18.rect.top"),sQuery(id+"F0.wireOp",EDGE,"E18.rect.left"),sQuery(id+"F0.wireOp",EDGE,"E18.rect.right"),sQuery(id+"F0.wireOp",EDGE,"E19.rect.left"),sQuery(id+"F0.wireOp",EDGE,"E19.rect.right"),sQuery(id+"F0.wireOp",EDGE,"E20.rect.bottom"),subQ0,sQuery(id+"F0.wireOp",EDGE,"E23.top"),sQuery(id+"F0.wireOp",EDGE,"E23.left"),sQuery(id+"F0.wireOp",EDGE,"E23.right"),sQuery(id+"F0.wireOp",EDGE,"E24.top"),sQuery(id+"F0.wireOp",EDGE,"E24.left"),sQuery(id+"F0.wireOp",EDGE,"E24.right"),sQuery(id+"F0.wireOp",EDGE,"E25.top"),sQuery(id+"F0.wireOp",EDGE,"E25.left"),sQuery(id+"F0.wireOp",EDGE,"E25.right"),sQuery(id+"F0.wireOp",EDGE,"E26.top"),sQuery(id+"F0.wireOp",EDGE,"E26.left"),sQuery(id+"F0.wireOp",EDGE,"E26.right")])],"isStart":false})]});}
            var Q62;
            {var subQ0=sQuery(id+"F0.wireOp",EDGE,"E12");var subQ1=makeQuery(id+"F0.imprint","INTERSECT",VERTEX,{"disambiguationData":[OD(0.0)],"derivedFrom":[sQuery(id+"F0.wireOp",EDGE,"E6"),subQ0]});Q62=makeQuery(id+"F1.opExtrude","CAP_EDGE",EDGE,{"disambiguationData":[OSD([subQ0]),TDD([makeQuery(id+"F0.imprint","IMPRINT",EDGE,{"disambiguationData":[TD([[subQ1,1.0]])],"derivedFrom":subQ0}),makeQuery(id+"F0.imprint","IMPRINT",EDGE,{"disambiguationData":[TD([[makeQuery(id+"F0.imprint","INTERSECT",VERTEX,{"disambiguationData":[OD(0.0)],"derivedFrom":[sQuery(id+"F0.wireOp",EDGE,"E2"),subQ0]}),1.0]])],"derivedFrom":subQ0})])],"isStart":false});}
            var Q63;
            {var subQ0=sQuery(id+"F0.wireOp",EDGE,"E18.rect.left");var subQ1=sQuery(id+"F0.wireOp",EDGE,"E18.rect.top");Q63=makeQuery(id+"F3.opFillet","BLEND_EDGE",EDGE,{"blendedFrom":[makeQuery(id+"F1.opExtrude","SWEPT_EDGE",EDGE,{"disambiguationData":[OSD([subQ1,subQ0])]}),makeQuery(id+"F1.opExtrude","CAP_FACE",FACE,{"disambiguationData":[OSD([sQuery(id+"F0.wireOp",EDGE,"E0"),sQuery(id+"F0.wireOp",EDGE,"E1"),sQuery(id+"F0.wireOp",EDGE,"E2"),sQuery(id+"F0.wireOp",EDGE,"E3"),sQuery(id+"F0.wireOp",EDGE,"E4"),sQuery(id+"F0.wireOp",EDGE,"E5"),sQuery(id+"F0.wireOp",EDGE,"E6"),sQuery(id+"F0.wireOp",EDGE,"E7"),sQuery(id+"F0.wireOp",EDGE,"E8"),sQuery(id+"F0.wireOp",EDGE,"E9"),sQuery(id+"F0.wireOp",EDGE,"E10"),sQuery(id+"F0.wireOp",EDGE,"E11"),sQuery(id+"F0.wireOp",EDGE,"E12"),sQuery(id+"F0.wireOp",EDGE,"E13"),sQuery(id+"F0.wireOp",EDGE,"E14"),sQuery(id+"F0.wireOp",EDGE,"E15"),sQuery(id+"F0.wireOp",EDGE,"E17.rect.bottom"),sQuery(id+"F0.wireOp",EDGE,"E17.rect.top"),sQuery(id+"F0.wireOp",EDGE,"E17.rect.left"),sQuery(id+"F0.wireOp",EDGE,"E17.rect.right"),sQuery(id+"F0.wireOp",EDGE,"E18.rect.bottom"),subQ1,subQ0,sQuery(id+"F0.wireOp",EDGE,"E18.rect.right"),sQuery(id+"F0.wireOp",EDGE,"E19.rect.left"),sQuery(id+"F0.wireOp",EDGE,"E19.rect.right"),sQuery(id+"F0.wireOp",EDGE,"E20.rect.bottom"),sQuery(id+"F0.wireOp",EDGE,"E20.rect.top"),sQuery(id+"F0.wireOp",EDGE,"E23.top"),sQuery(id+"F0.wireOp",EDGE,"E23.left"),sQuery(id+"F0.wireOp",EDGE,"E23.right"),sQuery(id+"F0.wireOp",EDGE,"E24.top"),sQuery(id+"F0.wireOp",EDGE,"E24.left"),sQuery(id+"F0.wireOp",EDGE,"E24.right"),sQuery(id+"F0.wireOp",EDGE,"E25.top"),sQuery(id+"F0.wireOp",EDGE,"E25.left"),sQuery(id+"F0.wireOp",EDGE,"E25.right"),sQuery(id+"F0.wireOp",EDGE,"E26.top"),sQuery(id+"F0.wireOp",EDGE,"E26.left"),sQuery(id+"F0.wireOp",EDGE,"E26.right")])],"isStart":false})],"blendedInto":[makeQuery(id+"F1.opExtrude","CAP_FACE",FACE,{"disambiguationData":[OSD([sQuery(id+"F0.wireOp",EDGE,"E0"),sQuery(id+"F0.wireOp",EDGE,"E1"),sQuery(id+"F0.wireOp",EDGE,"E2"),sQuery(id+"F0.wireOp",EDGE,"E3"),sQuery(id+"F0.wireOp",EDGE,"E4"),sQuery(id+"F0.wireOp",EDGE,"E5"),sQuery(id+"F0.wireOp",EDGE,"E6"),sQuery(id+"F0.wireOp",EDGE,"E7"),sQuery(id+"F0.wireOp",EDGE,"E8"),sQuery(id+"F0.wireOp",EDGE,"E9"),sQuery(id+"F0.wireOp",EDGE,"E10"),sQuery(id+"F0.wireOp",EDGE,"E11"),sQuery(id+"F0.wireOp",EDGE,"E12"),sQuery(id+"F0.wireOp",EDGE,"E13"),sQuery(id+"F0.wireOp",EDGE,"E14"),sQuery(id+"F0.wireOp",EDGE,"E15"),sQuery(id+"F0.wireOp",EDGE,"E17.rect.bottom"),sQuery(id+"F0.wireOp",EDGE,"E17.rect.top"),sQuery(id+"F0.wireOp",EDGE,"E17.rect.left"),sQuery(id+"F0.wireOp",EDGE,"E17.rect.right"),sQuery(id+"F0.wireOp",EDGE,"E18.rect.bottom"),subQ1,subQ0,sQuery(id+"F0.wireOp",EDGE,"E18.rect.right"),sQuery(id+"F0.wireOp",EDGE,"E19.rect.left"),sQuery(id+"F0.wireOp",EDGE,"E19.rect.right"),sQuery(id+"F0.wireOp",EDGE,"E20.rect.bottom"),sQuery(id+"F0.wireOp",EDGE,"E20.rect.top"),sQuery(id+"F0.wireOp",EDGE,"E23.top"),sQuery(id+"F0.wireOp",EDGE,"E23.left"),sQuery(id+"F0.wireOp",EDGE,"E23.right"),sQuery(id+"F0.wireOp",EDGE,"E24.top"),sQuery(id+"F0.wireOp",EDGE,"E24.left"),sQuery(id+"F0.wireOp",EDGE,"E24.right"),sQuery(id+"F0.wireOp",EDGE,"E25.top"),sQuery(id+"F0.wireOp",EDGE,"E25.left"),sQuery(id+"F0.wireOp",EDGE,"E25.right"),sQuery(id+"F0.wireOp",EDGE,"E26.top"),sQuery(id+"F0.wireOp",EDGE,"E26.left"),sQuery(id+"F0.wireOp",EDGE,"E26.right")])],"isStart":false})]});}
            var Q64;
            Q64=makeQuery(id+"F1.opExtrude","CAP_EDGE",EDGE,{"disambiguationData":[OSD([sQuery(id+"F0.wireOp",EDGE,"E18.rect.top")])],"isStart":false});
            var Q65;
            Q65=makeQuery(id+"F1.opExtrude","CAP_EDGE",EDGE,{"disambiguationData":[OSD([sQuery(id+"F0.wireOp",EDGE,"E18.rect.left")])],"isStart":false});
            var Q66;
            {var subQ0=sQuery(id+"F0.wireOp",EDGE,"E18.rect.left");var subQ1=sQuery(id+"F0.wireOp",EDGE,"E18.rect.bottom");Q66=makeQuery(id+"F3.opFillet","BLEND_EDGE",EDGE,{"blendedFrom":[makeQuery(id+"F1.opExtrude","SWEPT_EDGE",EDGE,{"disambiguationData":[OSD([subQ1,subQ0])]}),makeQuery(id+"F1.opExtrude","CAP_FACE",FACE,{"disambiguationData":[OSD([sQuery(id+"F0.wireOp",EDGE,"E0"),sQuery(id+"F0.wireOp",EDGE,"E1"),sQuery(id+"F0.wireOp",EDGE,"E2"),sQuery(id+"F0.wireOp",EDGE,"E3"),sQuery(id+"F0.wireOp",EDGE,"E4"),sQuery(id+"F0.wireOp",EDGE,"E5"),sQuery(id+"F0.wireOp",EDGE,"E6"),sQuery(id+"F0.wireOp",EDGE,"E7"),sQuery(id+"F0.wireOp",EDGE,"E8"),sQuery(id+"F0.wireOp",EDGE,"E9"),sQuery(id+"F0.wireOp",EDGE,"E10"),sQuery(id+"F0.wireOp",EDGE,"E11"),sQuery(id+"F0.wireOp",EDGE,"E12"),sQuery(id+"F0.wireOp",EDGE,"E13"),sQuery(id+"F0.wireOp",EDGE,"E14"),sQuery(id+"F0.wireOp",EDGE,"E15"),sQuery(id+"F0.wireOp",EDGE,"E17.rect.bottom"),sQuery(id+"F0.wireOp",EDGE,"E17.rect.top"),sQuery(id+"F0.wireOp",EDGE,"E17.rect.left"),sQuery(id+"F0.wireOp",EDGE,"E17.rect.right"),subQ1,sQuery(id+"F0.wireOp",EDGE,"E18.rect.top"),subQ0,sQuery(id+"F0.wireOp",EDGE,"E18.rect.right"),sQuery(id+"F0.wireOp",EDGE,"E19.rect.left"),sQuery(id+"F0.wireOp",EDGE,"E19.rect.right"),sQuery(id+"F0.wireOp",EDGE,"E20.rect.bottom"),sQuery(id+"F0.wireOp",EDGE,"E20.rect.top"),sQuery(id+"F0.wireOp",EDGE,"E23.top"),sQuery(id+"F0.wireOp",EDGE,"E23.left"),sQuery(id+"F0.wireOp",EDGE,"E23.right"),sQuery(id+"F0.wireOp",EDGE,"E24.top"),sQuery(id+"F0.wireOp",EDGE,"E24.left"),sQuery(id+"F0.wireOp",EDGE,"E24.right"),sQuery(id+"F0.wireOp",EDGE,"E25.top"),sQuery(id+"F0.wireOp",EDGE,"E25.left"),sQuery(id+"F0.wireOp",EDGE,"E25.right"),sQuery(id+"F0.wireOp",EDGE,"E26.top"),sQuery(id+"F0.wireOp",EDGE,"E26.left"),sQuery(id+"F0.wireOp",EDGE,"E26.right")])],"isStart":false})],"blendedInto":[makeQuery(id+"F1.opExtrude","CAP_FACE",FACE,{"disambiguationData":[OSD([sQuery(id+"F0.wireOp",EDGE,"E0"),sQuery(id+"F0.wireOp",EDGE,"E1"),sQuery(id+"F0.wireOp",EDGE,"E2"),sQuery(id+"F0.wireOp",EDGE,"E3"),sQuery(id+"F0.wireOp",EDGE,"E4"),sQuery(id+"F0.wireOp",EDGE,"E5"),sQuery(id+"F0.wireOp",EDGE,"E6"),sQuery(id+"F0.wireOp",EDGE,"E7"),sQuery(id+"F0.wireOp",EDGE,"E8"),sQuery(id+"F0.wireOp",EDGE,"E9"),sQuery(id+"F0.wireOp",EDGE,"E10"),sQuery(id+"F0.wireOp",EDGE,"E11"),sQuery(id+"F0.wireOp",EDGE,"E12"),sQuery(id+"F0.wireOp",EDGE,"E13"),sQuery(id+"F0.wireOp",EDGE,"E14"),sQuery(id+"F0.wireOp",EDGE,"E15"),sQuery(id+"F0.wireOp",EDGE,"E17.rect.bottom"),sQuery(id+"F0.wireOp",EDGE,"E17.rect.top"),sQuery(id+"F0.wireOp",EDGE,"E17.rect.left"),sQuery(id+"F0.wireOp",EDGE,"E17.rect.right"),subQ1,sQuery(id+"F0.wireOp",EDGE,"E18.rect.top"),subQ0,sQuery(id+"F0.wireOp",EDGE,"E18.rect.right"),sQuery(id+"F0.wireOp",EDGE,"E19.rect.left"),sQuery(id+"F0.wireOp",EDGE,"E19.rect.right"),sQuery(id+"F0.wireOp",EDGE,"E20.rect.bottom"),sQuery(id+"F0.wireOp",EDGE,"E20.rect.top"),sQuery(id+"F0.wireOp",EDGE,"E23.top"),sQuery(id+"F0.wireOp",EDGE,"E23.left"),sQuery(id+"F0.wireOp",EDGE,"E23.right"),sQuery(id+"F0.wireOp",EDGE,"E24.top"),sQuery(id+"F0.wireOp",EDGE,"E24.left"),sQuery(id+"F0.wireOp",EDGE,"E24.right"),sQuery(id+"F0.wireOp",EDGE,"E25.top"),sQuery(id+"F0.wireOp",EDGE,"E25.left"),sQuery(id+"F0.wireOp",EDGE,"E25.right"),sQuery(id+"F0.wireOp",EDGE,"E26.top"),sQuery(id+"F0.wireOp",EDGE,"E26.left"),sQuery(id+"F0.wireOp",EDGE,"E26.right")])],"isStart":false})]});}
            var Q67;
            Q67=makeQuery(id+"F1.opExtrude","CAP_EDGE",EDGE,{"disambiguationData":[OSD([sQuery(id+"F0.wireOp",EDGE,"E18.rect.bottom")])],"isStart":false});
            var Q68;
            {var subQ0=sQuery(id+"F0.wireOp",EDGE,"E18.rect.right");var subQ1=sQuery(id+"F0.wireOp",EDGE,"E18.rect.bottom");Q68=makeQuery(id+"F3.opFillet","BLEND_EDGE",EDGE,{"blendedFrom":[makeQuery(id+"F1.opExtrude","SWEPT_EDGE",EDGE,{"disambiguationData":[OSD([subQ1,subQ0])]}),makeQuery(id+"F1.opExtrude","CAP_FACE",FACE,{"disambiguationData":[OSD([sQuery(id+"F0.wireOp",EDGE,"E0"),sQuery(id+"F0.wireOp",EDGE,"E1"),sQuery(id+"F0.wireOp",EDGE,"E2"),sQuery(id+"F0.wireOp",EDGE,"E3"),sQuery(id+"F0.wireOp",EDGE,"E4"),sQuery(id+"F0.wireOp",EDGE,"E5"),sQuery(id+"F0.wireOp",EDGE,"E6"),sQuery(id+"F0.wireOp",EDGE,"E7"),sQuery(id+"F0.wireOp",EDGE,"E8"),sQuery(id+"F0.wireOp",EDGE,"E9"),sQuery(id+"F0.wireOp",EDGE,"E10"),sQuery(id+"F0.wireOp",EDGE,"E11"),sQuery(id+"F0.wireOp",EDGE,"E12"),sQuery(id+"F0.wireOp",EDGE,"E13"),sQuery(id+"F0.wireOp",EDGE,"E14"),sQuery(id+"F0.wireOp",EDGE,"E15"),sQuery(id+"F0.wireOp",EDGE,"E17.rect.bottom"),sQuery(id+"F0.wireOp",EDGE,"E17.rect.top"),sQuery(id+"F0.wireOp",EDGE,"E17.rect.left"),sQuery(id+"F0.wireOp",EDGE,"E17.rect.right"),subQ1,sQuery(id+"F0.wireOp",EDGE,"E18.rect.top"),sQuery(id+"F0.wireOp",EDGE,"E18.rect.left"),subQ0,sQuery(id+"F0.wireOp",EDGE,"E19.rect.left"),sQuery(id+"F0.wireOp",EDGE,"E19.rect.right"),sQuery(id+"F0.wireOp",EDGE,"E20.rect.bottom"),sQuery(id+"F0.wireOp",EDGE,"E20.rect.top"),sQuery(id+"F0.wireOp",EDGE,"E23.top"),sQuery(id+"F0.wireOp",EDGE,"E23.left"),sQuery(id+"F0.wireOp",EDGE,"E23.right"),sQuery(id+"F0.wireOp",EDGE,"E24.top"),sQuery(id+"F0.wireOp",EDGE,"E24.left"),sQuery(id+"F0.wireOp",EDGE,"E24.right"),sQuery(id+"F0.wireOp",EDGE,"E25.top"),sQuery(id+"F0.wireOp",EDGE,"E25.left"),sQuery(id+"F0.wireOp",EDGE,"E25.right"),sQuery(id+"F0.wireOp",EDGE,"E26.top"),sQuery(id+"F0.wireOp",EDGE,"E26.left"),sQuery(id+"F0.wireOp",EDGE,"E26.right")])],"isStart":false})],"blendedInto":[makeQuery(id+"F1.opExtrude","CAP_FACE",FACE,{"disambiguationData":[OSD([sQuery(id+"F0.wireOp",EDGE,"E0"),sQuery(id+"F0.wireOp",EDGE,"E1"),sQuery(id+"F0.wireOp",EDGE,"E2"),sQuery(id+"F0.wireOp",EDGE,"E3"),sQuery(id+"F0.wireOp",EDGE,"E4"),sQuery(id+"F0.wireOp",EDGE,"E5"),sQuery(id+"F0.wireOp",EDGE,"E6"),sQuery(id+"F0.wireOp",EDGE,"E7"),sQuery(id+"F0.wireOp",EDGE,"E8"),sQuery(id+"F0.wireOp",EDGE,"E9"),sQuery(id+"F0.wireOp",EDGE,"E10"),sQuery(id+"F0.wireOp",EDGE,"E11"),sQuery(id+"F0.wireOp",EDGE,"E12"),sQuery(id+"F0.wireOp",EDGE,"E13"),sQuery(id+"F0.wireOp",EDGE,"E14"),sQuery(id+"F0.wireOp",EDGE,"E15"),sQuery(id+"F0.wireOp",EDGE,"E17.rect.bottom"),sQuery(id+"F0.wireOp",EDGE,"E17.rect.top"),sQuery(id+"F0.wireOp",EDGE,"E17.rect.left"),sQuery(id+"F0.wireOp",EDGE,"E17.rect.right"),subQ1,sQuery(id+"F0.wireOp",EDGE,"E18.rect.top"),sQuery(id+"F0.wireOp",EDGE,"E18.rect.left"),subQ0,sQuery(id+"F0.wireOp",EDGE,"E19.rect.left"),sQuery(id+"F0.wireOp",EDGE,"E19.rect.right"),sQuery(id+"F0.wireOp",EDGE,"E20.rect.bottom"),sQuery(id+"F0.wireOp",EDGE,"E20.rect.top"),sQuery(id+"F0.wireOp",EDGE,"E23.top"),sQuery(id+"F0.wireOp",EDGE,"E23.left"),sQuery(id+"F0.wireOp",EDGE,"E23.right"),sQuery(id+"F0.wireOp",EDGE,"E24.top"),sQuery(id+"F0.wireOp",EDGE,"E24.left"),sQuery(id+"F0.wireOp",EDGE,"E24.right"),sQuery(id+"F0.wireOp",EDGE,"E25.top"),sQuery(id+"F0.wireOp",EDGE,"E25.left"),sQuery(id+"F0.wireOp",EDGE,"E25.right"),sQuery(id+"F0.wireOp",EDGE,"E26.top"),sQuery(id+"F0.wireOp",EDGE,"E26.left"),sQuery(id+"F0.wireOp",EDGE,"E26.right")])],"isStart":false})]});}
            var Q69;
            Q69=makeQuery(id+"F1.opExtrude","CAP_EDGE",EDGE,{"disambiguationData":[OSD([sQuery(id+"F0.wireOp",EDGE,"E18.rect.right")])],"isStart":false});
            var Q70;
            {var subQ0=sQuery(id+"F0.wireOp",EDGE,"E18.rect.right");var subQ1=sQuery(id+"F0.wireOp",EDGE,"E18.rect.top");Q70=makeQuery(id+"F3.opFillet","BLEND_EDGE",EDGE,{"blendedFrom":[makeQuery(id+"F1.opExtrude","SWEPT_EDGE",EDGE,{"disambiguationData":[OSD([subQ1,subQ0])]}),makeQuery(id+"F1.opExtrude","CAP_FACE",FACE,{"disambiguationData":[OSD([sQuery(id+"F0.wireOp",EDGE,"E0"),sQuery(id+"F0.wireOp",EDGE,"E1"),sQuery(id+"F0.wireOp",EDGE,"E2"),sQuery(id+"F0.wireOp",EDGE,"E3"),sQuery(id+"F0.wireOp",EDGE,"E4"),sQuery(id+"F0.wireOp",EDGE,"E5"),sQuery(id+"F0.wireOp",EDGE,"E6"),sQuery(id+"F0.wireOp",EDGE,"E7"),sQuery(id+"F0.wireOp",EDGE,"E8"),sQuery(id+"F0.wireOp",EDGE,"E9"),sQuery(id+"F0.wireOp",EDGE,"E10"),sQuery(id+"F0.wireOp",EDGE,"E11"),sQuery(id+"F0.wireOp",EDGE,"E12"),sQuery(id+"F0.wireOp",EDGE,"E13"),sQuery(id+"F0.wireOp",EDGE,"E14"),sQuery(id+"F0.wireOp",EDGE,"E15"),sQuery(id+"F0.wireOp",EDGE,"E17.rect.bottom"),sQuery(id+"F0.wireOp",EDGE,"E17.rect.top"),sQuery(id+"F0.wireOp",EDGE,"E17.rect.left"),sQuery(id+"F0.wireOp",EDGE,"E17.rect.right"),sQuery(id+"F0.wireOp",EDGE,"E18.rect.bottom"),subQ1,sQuery(id+"F0.wireOp",EDGE,"E18.rect.left"),subQ0,sQuery(id+"F0.wireOp",EDGE,"E19.rect.left"),sQuery(id+"F0.wireOp",EDGE,"E19.rect.right"),sQuery(id+"F0.wireOp",EDGE,"E20.rect.bottom"),sQuery(id+"F0.wireOp",EDGE,"E20.rect.top"),sQuery(id+"F0.wireOp",EDGE,"E23.top"),sQuery(id+"F0.wireOp",EDGE,"E23.left"),sQuery(id+"F0.wireOp",EDGE,"E23.right"),sQuery(id+"F0.wireOp",EDGE,"E24.top"),sQuery(id+"F0.wireOp",EDGE,"E24.left"),sQuery(id+"F0.wireOp",EDGE,"E24.right"),sQuery(id+"F0.wireOp",EDGE,"E25.top"),sQuery(id+"F0.wireOp",EDGE,"E25.left"),sQuery(id+"F0.wireOp",EDGE,"E25.right"),sQuery(id+"F0.wireOp",EDGE,"E26.top"),sQuery(id+"F0.wireOp",EDGE,"E26.left"),sQuery(id+"F0.wireOp",EDGE,"E26.right")])],"isStart":false})],"blendedInto":[makeQuery(id+"F1.opExtrude","CAP_FACE",FACE,{"disambiguationData":[OSD([sQuery(id+"F0.wireOp",EDGE,"E0"),sQuery(id+"F0.wireOp",EDGE,"E1"),sQuery(id+"F0.wireOp",EDGE,"E2"),sQuery(id+"F0.wireOp",EDGE,"E3"),sQuery(id+"F0.wireOp",EDGE,"E4"),sQuery(id+"F0.wireOp",EDGE,"E5"),sQuery(id+"F0.wireOp",EDGE,"E6"),sQuery(id+"F0.wireOp",EDGE,"E7"),sQuery(id+"F0.wireOp",EDGE,"E8"),sQuery(id+"F0.wireOp",EDGE,"E9"),sQuery(id+"F0.wireOp",EDGE,"E10"),sQuery(id+"F0.wireOp",EDGE,"E11"),sQuery(id+"F0.wireOp",EDGE,"E12"),sQuery(id+"F0.wireOp",EDGE,"E13"),sQuery(id+"F0.wireOp",EDGE,"E14"),sQuery(id+"F0.wireOp",EDGE,"E15"),sQuery(id+"F0.wireOp",EDGE,"E17.rect.bottom"),sQuery(id+"F0.wireOp",EDGE,"E17.rect.top"),sQuery(id+"F0.wireOp",EDGE,"E17.rect.left"),sQuery(id+"F0.wireOp",EDGE,"E17.rect.right"),sQuery(id+"F0.wireOp",EDGE,"E18.rect.bottom"),subQ1,sQuery(id+"F0.wireOp",EDGE,"E18.rect.left"),subQ0,sQuery(id+"F0.wireOp",EDGE,"E19.rect.left"),sQuery(id+"F0.wireOp",EDGE,"E19.rect.right"),sQuery(id+"F0.wireOp",EDGE,"E20.rect.bottom"),sQuery(id+"F0.wireOp",EDGE,"E20.rect.top"),sQuery(id+"F0.wireOp",EDGE,"E23.top"),sQuery(id+"F0.wireOp",EDGE,"E23.left"),sQuery(id+"F0.wireOp",EDGE,"E23.right"),sQuery(id+"F0.wireOp",EDGE,"E24.top"),sQuery(id+"F0.wireOp",EDGE,"E24.left"),sQuery(id+"F0.wireOp",EDGE,"E24.right"),sQuery(id+"F0.wireOp",EDGE,"E25.top"),sQuery(id+"F0.wireOp",EDGE,"E25.left"),sQuery(id+"F0.wireOp",EDGE,"E25.right"),sQuery(id+"F0.wireOp",EDGE,"E26.top"),sQuery(id+"F0.wireOp",EDGE,"E26.left"),sQuery(id+"F0.wireOp",EDGE,"E26.right")])],"isStart":false})]});}
            var Q71;
            {var subQ0=sQuery(id+"F0.wireOp",EDGE,"E17.rect.top");Q71=makeQuery(id+"F1.opExtrude","CAP_EDGE",EDGE,{"disambiguationData":[OSD([subQ0]),TDD([makeQuery(id+"F0.imprint","IMPRINT",EDGE,{"disambiguationData":[TD([[makeQuery(id+"F0.imprint","INTERSECT",VERTEX,{"derivedFrom":[subQ0,sQuery(id+"F0.wireOp",EDGE,"E19.rect.right")]}),-1.0]])],"derivedFrom":subQ0})])],"isStart":false});}
            var Q72;
            Q72=makeQuery(id+"F1.opExtrude","CAP_EDGE",EDGE,{"disambiguationData":[OSD([sQuery(id+"F0.wireOp",EDGE,"E24.right")])],"isStart":false});
            var Q73;
            {var subQ0=sQuery(id+"F0.wireOp",EDGE,"E19.rect.right");var subQ1=sQuery(id+"F0.wireOp",EDGE,"E17.rect.top");Q73=makeQuery(id+"F3.opFillet","BLEND_EDGE",EDGE,{"blendedFrom":[makeQuery(id+"F1.opExtrude","SWEPT_EDGE",EDGE,{"disambiguationData":[OSD([subQ1,subQ0])]}),makeQuery(id+"F1.opExtrude","CAP_FACE",FACE,{"disambiguationData":[OSD([sQuery(id+"F0.wireOp",EDGE,"E0"),sQuery(id+"F0.wireOp",EDGE,"E1"),sQuery(id+"F0.wireOp",EDGE,"E2"),sQuery(id+"F0.wireOp",EDGE,"E3"),sQuery(id+"F0.wireOp",EDGE,"E4"),sQuery(id+"F0.wireOp",EDGE,"E5"),sQuery(id+"F0.wireOp",EDGE,"E6"),sQuery(id+"F0.wireOp",EDGE,"E7"),sQuery(id+"F0.wireOp",EDGE,"E8"),sQuery(id+"F0.wireOp",EDGE,"E9"),sQuery(id+"F0.wireOp",EDGE,"E10"),sQuery(id+"F0.wireOp",EDGE,"E11"),sQuery(id+"F0.wireOp",EDGE,"E12"),sQuery(id+"F0.wireOp",EDGE,"E13"),sQuery(id+"F0.wireOp",EDGE,"E14"),sQuery(id+"F0.wireOp",EDGE,"E15"),sQuery(id+"F0.wireOp",EDGE,"E17.rect.bottom"),subQ1,sQuery(id+"F0.wireOp",EDGE,"E17.rect.left"),sQuery(id+"F0.wireOp",EDGE,"E17.rect.right"),sQuery(id+"F0.wireOp",EDGE,"E18.rect.bottom"),sQuery(id+"F0.wireOp",EDGE,"E18.rect.top"),sQuery(id+"F0.wireOp",EDGE,"E18.rect.left"),sQuery(id+"F0.wireOp",EDGE,"E18.rect.right"),sQuery(id+"F0.wireOp",EDGE,"E19.rect.left"),subQ0,sQuery(id+"F0.wireOp",EDGE,"E20.rect.bottom"),sQuery(id+"F0.wireOp",EDGE,"E20.rect.top"),sQuery(id+"F0.wireOp",EDGE,"E23.top"),sQuery(id+"F0.wireOp",EDGE,"E23.left"),sQuery(id+"F0.wireOp",EDGE,"E23.right"),sQuery(id+"F0.wireOp",EDGE,"E24.top"),sQuery(id+"F0.wireOp",EDGE,"E24.left"),sQuery(id+"F0.wireOp",EDGE,"E24.right"),sQuery(id+"F0.wireOp",EDGE,"E25.top"),sQuery(id+"F0.wireOp",EDGE,"E25.left"),sQuery(id+"F0.wireOp",EDGE,"E25.right"),sQuery(id+"F0.wireOp",EDGE,"E26.top"),sQuery(id+"F0.wireOp",EDGE,"E26.left"),sQuery(id+"F0.wireOp",EDGE,"E26.right")])],"isStart":false})],"blendedInto":[makeQuery(id+"F1.opExtrude","CAP_FACE",FACE,{"disambiguationData":[OSD([sQuery(id+"F0.wireOp",EDGE,"E0"),sQuery(id+"F0.wireOp",EDGE,"E1"),sQuery(id+"F0.wireOp",EDGE,"E2"),sQuery(id+"F0.wireOp",EDGE,"E3"),sQuery(id+"F0.wireOp",EDGE,"E4"),sQuery(id+"F0.wireOp",EDGE,"E5"),sQuery(id+"F0.wireOp",EDGE,"E6"),sQuery(id+"F0.wireOp",EDGE,"E7"),sQuery(id+"F0.wireOp",EDGE,"E8"),sQuery(id+"F0.wireOp",EDGE,"E9"),sQuery(id+"F0.wireOp",EDGE,"E10"),sQuery(id+"F0.wireOp",EDGE,"E11"),sQuery(id+"F0.wireOp",EDGE,"E12"),sQuery(id+"F0.wireOp",EDGE,"E13"),sQuery(id+"F0.wireOp",EDGE,"E14"),sQuery(id+"F0.wireOp",EDGE,"E15"),sQuery(id+"F0.wireOp",EDGE,"E17.rect.bottom"),subQ1,sQuery(id+"F0.wireOp",EDGE,"E17.rect.left"),sQuery(id+"F0.wireOp",EDGE,"E17.rect.right"),sQuery(id+"F0.wireOp",EDGE,"E18.rect.bottom"),sQuery(id+"F0.wireOp",EDGE,"E18.rect.top"),sQuery(id+"F0.wireOp",EDGE,"E18.rect.left"),sQuery(id+"F0.wireOp",EDGE,"E18.rect.right"),sQuery(id+"F0.wireOp",EDGE,"E19.rect.left"),subQ0,sQuery(id+"F0.wireOp",EDGE,"E20.rect.bottom"),sQuery(id+"F0.wireOp",EDGE,"E20.rect.top"),sQuery(id+"F0.wireOp",EDGE,"E23.top"),sQuery(id+"F0.wireOp",EDGE,"E23.left"),sQuery(id+"F0.wireOp",EDGE,"E23.right"),sQuery(id+"F0.wireOp",EDGE,"E24.top"),sQuery(id+"F0.wireOp",EDGE,"E24.left"),sQuery(id+"F0.wireOp",EDGE,"E24.right"),sQuery(id+"F0.wireOp",EDGE,"E25.top"),sQuery(id+"F0.wireOp",EDGE,"E25.left"),sQuery(id+"F0.wireOp",EDGE,"E25.right"),sQuery(id+"F0.wireOp",EDGE,"E26.top"),sQuery(id+"F0.wireOp",EDGE,"E26.left"),sQuery(id+"F0.wireOp",EDGE,"E26.right")])],"isStart":false})]});}
            var Q74;
            {var subQ0=sQuery(id+"F0.wireOp",EDGE,"E19.rect.right");Q74=makeQuery(id+"F1.opExtrude","CAP_EDGE",EDGE,{"disambiguationData":[OSD([subQ0]),TDD([makeQuery(id+"F0.imprint","IMPRINT",EDGE,{"disambiguationData":[TD([[makeQuery(id+"F0.imprint","INTERSECT",VERTEX,{"derivedFrom":[sQuery(id+"F0.wireOp",EDGE,"E14"),subQ0]}),1.0]])],"derivedFrom":subQ0})])],"isStart":false});}
            var Q75;
            {var subQ0=sQuery(id+"F0.wireOp",EDGE,"E19.rect.right");var subQ1=sQuery(id+"F0.wireOp",EDGE,"E14");Q75=makeQuery(id+"F3.opFillet","BLEND_EDGE",EDGE,{"blendedFrom":[makeQuery(id+"F1.opExtrude","SWEPT_EDGE",EDGE,{"disambiguationData":[OSD([subQ1,subQ0])]}),makeQuery(id+"F1.opExtrude","CAP_FACE",FACE,{"disambiguationData":[OSD([sQuery(id+"F0.wireOp",EDGE,"E0"),sQuery(id+"F0.wireOp",EDGE,"E1"),sQuery(id+"F0.wireOp",EDGE,"E2"),sQuery(id+"F0.wireOp",EDGE,"E3"),sQuery(id+"F0.wireOp",EDGE,"E4"),sQuery(id+"F0.wireOp",EDGE,"E5"),sQuery(id+"F0.wireOp",EDGE,"E6"),sQuery(id+"F0.wireOp",EDGE,"E7"),sQuery(id+"F0.wireOp",EDGE,"E8"),sQuery(id+"F0.wireOp",EDGE,"E9"),sQuery(id+"F0.wireOp",EDGE,"E10"),sQuery(id+"F0.wireOp",EDGE,"E11"),sQuery(id+"F0.wireOp",EDGE,"E12"),sQuery(id+"F0.wireOp",EDGE,"E13"),subQ1,sQuery(id+"F0.wireOp",EDGE,"E15"),sQuery(id+"F0.wireOp",EDGE,"E17.rect.bottom"),sQuery(id+"F0.wireOp",EDGE,"E17.rect.top"),sQuery(id+"F0.wireOp",EDGE,"E17.rect.left"),sQuery(id+"F0.wireOp",EDGE,"E17.rect.right"),sQuery(id+"F0.wireOp",EDGE,"E18.rect.bottom"),sQuery(id+"F0.wireOp",EDGE,"E18.rect.top"),sQuery(id+"F0.wireOp",EDGE,"E18.rect.left"),sQuery(id+"F0.wireOp",EDGE,"E18.rect.right"),sQuery(id+"F0.wireOp",EDGE,"E19.rect.left"),subQ0,sQuery(id+"F0.wireOp",EDGE,"E20.rect.bottom"),sQuery(id+"F0.wireOp",EDGE,"E20.rect.top"),sQuery(id+"F0.wireOp",EDGE,"E23.top"),sQuery(id+"F0.wireOp",EDGE,"E23.left"),sQuery(id+"F0.wireOp",EDGE,"E23.right"),sQuery(id+"F0.wireOp",EDGE,"E24.top"),sQuery(id+"F0.wireOp",EDGE,"E24.left"),sQuery(id+"F0.wireOp",EDGE,"E24.right"),sQuery(id+"F0.wireOp",EDGE,"E25.top"),sQuery(id+"F0.wireOp",EDGE,"E25.left"),sQuery(id+"F0.wireOp",EDGE,"E25.right"),sQuery(id+"F0.wireOp",EDGE,"E26.top"),sQuery(id+"F0.wireOp",EDGE,"E26.left"),sQuery(id+"F0.wireOp",EDGE,"E26.right")])],"isStart":false})],"blendedInto":[makeQuery(id+"F1.opExtrude","CAP_FACE",FACE,{"disambiguationData":[OSD([sQuery(id+"F0.wireOp",EDGE,"E0"),sQuery(id+"F0.wireOp",EDGE,"E1"),sQuery(id+"F0.wireOp",EDGE,"E2"),sQuery(id+"F0.wireOp",EDGE,"E3"),sQuery(id+"F0.wireOp",EDGE,"E4"),sQuery(id+"F0.wireOp",EDGE,"E5"),sQuery(id+"F0.wireOp",EDGE,"E6"),sQuery(id+"F0.wireOp",EDGE,"E7"),sQuery(id+"F0.wireOp",EDGE,"E8"),sQuery(id+"F0.wireOp",EDGE,"E9"),sQuery(id+"F0.wireOp",EDGE,"E10"),sQuery(id+"F0.wireOp",EDGE,"E11"),sQuery(id+"F0.wireOp",EDGE,"E12"),sQuery(id+"F0.wireOp",EDGE,"E13"),subQ1,sQuery(id+"F0.wireOp",EDGE,"E15"),sQuery(id+"F0.wireOp",EDGE,"E17.rect.bottom"),sQuery(id+"F0.wireOp",EDGE,"E17.rect.top"),sQuery(id+"F0.wireOp",EDGE,"E17.rect.left"),sQuery(id+"F0.wireOp",EDGE,"E17.rect.right"),sQuery(id+"F0.wireOp",EDGE,"E18.rect.bottom"),sQuery(id+"F0.wireOp",EDGE,"E18.rect.top"),sQuery(id+"F0.wireOp",EDGE,"E18.rect.left"),sQuery(id+"F0.wireOp",EDGE,"E18.rect.right"),sQuery(id+"F0.wireOp",EDGE,"E19.rect.left"),subQ0,sQuery(id+"F0.wireOp",EDGE,"E20.rect.bottom"),sQuery(id+"F0.wireOp",EDGE,"E20.rect.top"),sQuery(id+"F0.wireOp",EDGE,"E23.top"),sQuery(id+"F0.wireOp",EDGE,"E23.left"),sQuery(id+"F0.wireOp",EDGE,"E23.right"),sQuery(id+"F0.wireOp",EDGE,"E24.top"),sQuery(id+"F0.wireOp",EDGE,"E24.left"),sQuery(id+"F0.wireOp",EDGE,"E24.right"),sQuery(id+"F0.wireOp",EDGE,"E25.top"),sQuery(id+"F0.wireOp",EDGE,"E25.left"),sQuery(id+"F0.wireOp",EDGE,"E25.right"),sQuery(id+"F0.wireOp",EDGE,"E26.top"),sQuery(id+"F0.wireOp",EDGE,"E26.left"),sQuery(id+"F0.wireOp",EDGE,"E26.right")])],"isStart":false})]});}
            var Q76;
            {var subQ0=sQuery(id+"F0.wireOp",EDGE,"E14");var subQ1=makeQuery(id+"F0.imprint","INTERSECT",VERTEX,{"disambiguationData":[OD(0.0)],"derivedFrom":[sQuery(id+"F0.wireOp",EDGE,"E5"),subQ0]});Q76=makeQuery(id+"F1.opExtrude","CAP_EDGE",EDGE,{"disambiguationData":[OSD([subQ0]),TDD([makeQuery(id+"F0.imprint","IMPRINT",EDGE,{"disambiguationData":[TD([[subQ1,1.0]])],"derivedFrom":subQ0}),makeQuery(id+"F0.imprint","IMPRINT",EDGE,{"disambiguationData":[TD([[makeQuery(id+"F0.imprint","INTERSECT",VERTEX,{"disambiguationData":[OD(1.0)],"derivedFrom":[sQuery(id+"F0.wireOp",EDGE,"E3"),subQ0]}),1.0]])],"derivedFrom":subQ0})])],"isStart":false});}
            var Q77;
            {var subQ0=sQuery(id+"F0.wireOp",EDGE,"E8");var subQ1=makeQuery(id+"F0.imprint","INTERSECT",VERTEX,{"disambiguationData":[OD(0.0)],"derivedFrom":[sQuery(id+"F0.wireOp",EDGE,"E5"),subQ0]});Q77=makeQuery(id+"F1.opExtrude","CAP_EDGE",EDGE,{"disambiguationData":[OSD([subQ0]),TDD([makeQuery(id+"F0.imprint","IMPRINT",EDGE,{"disambiguationData":[TD([[makeQuery(id+"F0.imprint","INTERSECT",VERTEX,{"disambiguationData":[OD(1.0)],"derivedFrom":[sQuery(id+"F0.wireOp",EDGE,"E3"),subQ0]}),-1.0]])],"derivedFrom":subQ0}),makeQuery(id+"F0.imprint","IMPRINT",EDGE,{"disambiguationData":[TD([[subQ1,-1.0]])],"derivedFrom":subQ0})])],"isStart":false});}
            var Q78;
            {var subQ0=sQuery(id+"F0.wireOp",EDGE,"E20.rect.top");var subQ1=sQuery(id+"F0.wireOp",EDGE,"E8");Q78=makeQuery(id+"F3.opFillet","BLEND_EDGE",EDGE,{"blendedFrom":[makeQuery(id+"F1.opExtrude","SWEPT_EDGE",EDGE,{"disambiguationData":[OSD([subQ1,subQ0])]}),makeQuery(id+"F1.opExtrude","CAP_FACE",FACE,{"disambiguationData":[OSD([sQuery(id+"F0.wireOp",EDGE,"E0"),sQuery(id+"F0.wireOp",EDGE,"E1"),sQuery(id+"F0.wireOp",EDGE,"E2"),sQuery(id+"F0.wireOp",EDGE,"E3"),sQuery(id+"F0.wireOp",EDGE,"E4"),sQuery(id+"F0.wireOp",EDGE,"E5"),sQuery(id+"F0.wireOp",EDGE,"E6"),sQuery(id+"F0.wireOp",EDGE,"E7"),subQ1,sQuery(id+"F0.wireOp",EDGE,"E9"),sQuery(id+"F0.wireOp",EDGE,"E10"),sQuery(id+"F0.wireOp",EDGE,"E11"),sQuery(id+"F0.wireOp",EDGE,"E12"),sQuery(id+"F0.wireOp",EDGE,"E13"),sQuery(id+"F0.wireOp",EDGE,"E14"),sQuery(id+"F0.wireOp",EDGE,"E15"),sQuery(id+"F0.wireOp",EDGE,"E17.rect.bottom"),sQuery(id+"F0.wireOp",EDGE,"E17.rect.top"),sQuery(id+"F0.wireOp",EDGE,"E17.rect.left"),sQuery(id+"F0.wireOp",EDGE,"E17.rect.right"),sQuery(id+"F0.wireOp",EDGE,"E18.rect.bottom"),sQuery(id+"F0.wireOp",EDGE,"E18.rect.top"),sQuery(id+"F0.wireOp",EDGE,"E18.rect.left"),sQuery(id+"F0.wireOp",EDGE,"E18.rect.right"),sQuery(id+"F0.wireOp",EDGE,"E19.rect.left"),sQuery(id+"F0.wireOp",EDGE,"E19.rect.right"),sQuery(id+"F0.wireOp",EDGE,"E20.rect.bottom"),subQ0,sQuery(id+"F0.wireOp",EDGE,"E23.top"),sQuery(id+"F0.wireOp",EDGE,"E23.left"),sQuery(id+"F0.wireOp",EDGE,"E23.right"),sQuery(id+"F0.wireOp",EDGE,"E24.top"),sQuery(id+"F0.wireOp",EDGE,"E24.left"),sQuery(id+"F0.wireOp",EDGE,"E24.right"),sQuery(id+"F0.wireOp",EDGE,"E25.top"),sQuery(id+"F0.wireOp",EDGE,"E25.left"),sQuery(id+"F0.wireOp",EDGE,"E25.right"),sQuery(id+"F0.wireOp",EDGE,"E26.top"),sQuery(id+"F0.wireOp",EDGE,"E26.left"),sQuery(id+"F0.wireOp",EDGE,"E26.right")])],"isStart":false})],"blendedInto":[makeQuery(id+"F1.opExtrude","CAP_FACE",FACE,{"disambiguationData":[OSD([sQuery(id+"F0.wireOp",EDGE,"E0"),sQuery(id+"F0.wireOp",EDGE,"E1"),sQuery(id+"F0.wireOp",EDGE,"E2"),sQuery(id+"F0.wireOp",EDGE,"E3"),sQuery(id+"F0.wireOp",EDGE,"E4"),sQuery(id+"F0.wireOp",EDGE,"E5"),sQuery(id+"F0.wireOp",EDGE,"E6"),sQuery(id+"F0.wireOp",EDGE,"E7"),subQ1,sQuery(id+"F0.wireOp",EDGE,"E9"),sQuery(id+"F0.wireOp",EDGE,"E10"),sQuery(id+"F0.wireOp",EDGE,"E11"),sQuery(id+"F0.wireOp",EDGE,"E12"),sQuery(id+"F0.wireOp",EDGE,"E13"),sQuery(id+"F0.wireOp",EDGE,"E14"),sQuery(id+"F0.wireOp",EDGE,"E15"),sQuery(id+"F0.wireOp",EDGE,"E17.rect.bottom"),sQuery(id+"F0.wireOp",EDGE,"E17.rect.top"),sQuery(id+"F0.wireOp",EDGE,"E17.rect.left"),sQuery(id+"F0.wireOp",EDGE,"E17.rect.right"),sQuery(id+"F0.wireOp",EDGE,"E18.rect.bottom"),sQuery(id+"F0.wireOp",EDGE,"E18.rect.top"),sQuery(id+"F0.wireOp",EDGE,"E18.rect.left"),sQuery(id+"F0.wireOp",EDGE,"E18.rect.right"),sQuery(id+"F0.wireOp",EDGE,"E19.rect.left"),sQuery(id+"F0.wireOp",EDGE,"E19.rect.right"),sQuery(id+"F0.wireOp",EDGE,"E20.rect.bottom"),subQ0,sQuery(id+"F0.wireOp",EDGE,"E23.top"),sQuery(id+"F0.wireOp",EDGE,"E23.left"),sQuery(id+"F0.wireOp",EDGE,"E23.right"),sQuery(id+"F0.wireOp",EDGE,"E24.top"),sQuery(id+"F0.wireOp",EDGE,"E24.left"),sQuery(id+"F0.wireOp",EDGE,"E24.right"),sQuery(id+"F0.wireOp",EDGE,"E25.top"),sQuery(id+"F0.wireOp",EDGE,"E25.left"),sQuery(id+"F0.wireOp",EDGE,"E25.right"),sQuery(id+"F0.wireOp",EDGE,"E26.top"),sQuery(id+"F0.wireOp",EDGE,"E26.left"),sQuery(id+"F0.wireOp",EDGE,"E26.right")])],"isStart":false})]});}
            var Q79;
            {var subQ0=sQuery(id+"F0.wireOp",EDGE,"E20.rect.top");Q79=makeQuery(id+"F1.opExtrude","CAP_EDGE",EDGE,{"disambiguationData":[OSD([subQ0]),TDD([makeQuery(id+"F0.imprint","IMPRINT",EDGE,{"disambiguationData":[TD([[makeQuery(id+"F0.imprint","INTERSECT",VERTEX,{"derivedFrom":[sQuery(id+"F0.wireOp",EDGE,"E8"),subQ0]}),1.0]])],"derivedFrom":subQ0})])],"isStart":false});}
            var Q80;
            {var subQ0=sQuery(id+"F0.wireOp",EDGE,"E20.rect.top");var subQ1=sQuery(id+"F0.wireOp",EDGE,"E17.rect.right");Q80=makeQuery(id+"F3.opFillet","BLEND_EDGE",EDGE,{"blendedFrom":[makeQuery(id+"F1.opExtrude","SWEPT_EDGE",EDGE,{"disambiguationData":[OSD([subQ1,subQ0])]}),makeQuery(id+"F1.opExtrude","CAP_FACE",FACE,{"disambiguationData":[OSD([sQuery(id+"F0.wireOp",EDGE,"E0"),sQuery(id+"F0.wireOp",EDGE,"E1"),sQuery(id+"F0.wireOp",EDGE,"E2"),sQuery(id+"F0.wireOp",EDGE,"E3"),sQuery(id+"F0.wireOp",EDGE,"E4"),sQuery(id+"F0.wireOp",EDGE,"E5"),sQuery(id+"F0.wireOp",EDGE,"E6"),sQuery(id+"F0.wireOp",EDGE,"E7"),sQuery(id+"F0.wireOp",EDGE,"E8"),sQuery(id+"F0.wireOp",EDGE,"E9"),sQuery(id+"F0.wireOp",EDGE,"E10"),sQuery(id+"F0.wireOp",EDGE,"E11"),sQuery(id+"F0.wireOp",EDGE,"E12"),sQuery(id+"F0.wireOp",EDGE,"E13"),sQuery(id+"F0.wireOp",EDGE,"E14"),sQuery(id+"F0.wireOp",EDGE,"E15"),sQuery(id+"F0.wireOp",EDGE,"E17.rect.bottom"),sQuery(id+"F0.wireOp",EDGE,"E17.rect.top"),sQuery(id+"F0.wireOp",EDGE,"E17.rect.left"),subQ1,sQuery(id+"F0.wireOp",EDGE,"E18.rect.bottom"),sQuery(id+"F0.wireOp",EDGE,"E18.rect.top"),sQuery(id+"F0.wireOp",EDGE,"E18.rect.left"),sQuery(id+"F0.wireOp",EDGE,"E18.rect.right"),sQuery(id+"F0.wireOp",EDGE,"E19.rect.left"),sQuery(id+"F0.wireOp",EDGE,"E19.rect.right"),sQuery(id+"F0.wireOp",EDGE,"E20.rect.bottom"),subQ0,sQuery(id+"F0.wireOp",EDGE,"E23.top"),sQuery(id+"F0.wireOp",EDGE,"E23.left"),sQuery(id+"F0.wireOp",EDGE,"E23.right"),sQuery(id+"F0.wireOp",EDGE,"E24.top"),sQuery(id+"F0.wireOp",EDGE,"E24.left"),sQuery(id+"F0.wireOp",EDGE,"E24.right"),sQuery(id+"F0.wireOp",EDGE,"E25.top"),sQuery(id+"F0.wireOp",EDGE,"E25.left"),sQuery(id+"F0.wireOp",EDGE,"E25.right"),sQuery(id+"F0.wireOp",EDGE,"E26.top"),sQuery(id+"F0.wireOp",EDGE,"E26.left"),sQuery(id+"F0.wireOp",EDGE,"E26.right")])],"isStart":false})],"blendedInto":[makeQuery(id+"F1.opExtrude","CAP_FACE",FACE,{"disambiguationData":[OSD([sQuery(id+"F0.wireOp",EDGE,"E0"),sQuery(id+"F0.wireOp",EDGE,"E1"),sQuery(id+"F0.wireOp",EDGE,"E2"),sQuery(id+"F0.wireOp",EDGE,"E3"),sQuery(id+"F0.wireOp",EDGE,"E4"),sQuery(id+"F0.wireOp",EDGE,"E5"),sQuery(id+"F0.wireOp",EDGE,"E6"),sQuery(id+"F0.wireOp",EDGE,"E7"),sQuery(id+"F0.wireOp",EDGE,"E8"),sQuery(id+"F0.wireOp",EDGE,"E9"),sQuery(id+"F0.wireOp",EDGE,"E10"),sQuery(id+"F0.wireOp",EDGE,"E11"),sQuery(id+"F0.wireOp",EDGE,"E12"),sQuery(id+"F0.wireOp",EDGE,"E13"),sQuery(id+"F0.wireOp",EDGE,"E14"),sQuery(id+"F0.wireOp",EDGE,"E15"),sQuery(id+"F0.wireOp",EDGE,"E17.rect.bottom"),sQuery(id+"F0.wireOp",EDGE,"E17.rect.top"),sQuery(id+"F0.wireOp",EDGE,"E17.rect.left"),subQ1,sQuery(id+"F0.wireOp",EDGE,"E18.rect.bottom"),sQuery(id+"F0.wireOp",EDGE,"E18.rect.top"),sQuery(id+"F0.wireOp",EDGE,"E18.rect.left"),sQuery(id+"F0.wireOp",EDGE,"E18.rect.right"),sQuery(id+"F0.wireOp",EDGE,"E19.rect.left"),sQuery(id+"F0.wireOp",EDGE,"E19.rect.right"),sQuery(id+"F0.wireOp",EDGE,"E20.rect.bottom"),subQ0,sQuery(id+"F0.wireOp",EDGE,"E23.top"),sQuery(id+"F0.wireOp",EDGE,"E23.left"),sQuery(id+"F0.wireOp",EDGE,"E23.right"),sQuery(id+"F0.wireOp",EDGE,"E24.top"),sQuery(id+"F0.wireOp",EDGE,"E24.left"),sQuery(id+"F0.wireOp",EDGE,"E24.right"),sQuery(id+"F0.wireOp",EDGE,"E25.top"),sQuery(id+"F0.wireOp",EDGE,"E25.left"),sQuery(id+"F0.wireOp",EDGE,"E25.right"),sQuery(id+"F0.wireOp",EDGE,"E26.top"),sQuery(id+"F0.wireOp",EDGE,"E26.left"),sQuery(id+"F0.wireOp",EDGE,"E26.right")])],"isStart":false})]});}
            var Q81;
            Q81=makeQuery(id+"F1.opExtrude","CAP_EDGE",EDGE,{"disambiguationData":[OSD([sQuery(id+"F0.wireOp",EDGE,"E17.rect.right"),sQuery(id+"F0.wireOp",EDGE,"E24.left")])],"isStart":false});
            var Q82;
            Q82=makeQuery(id+"F1.opExtrude","CAP_EDGE",EDGE,{"disambiguationData":[OSD([sQuery(id+"F0.wireOp",EDGE,"E17.rect.left"),sQuery(id+"F0.wireOp",EDGE,"E26.left")])],"isStart":false});
            var Q83;
            {var subQ0=sQuery(id+"F0.wireOp",EDGE,"E20.rect.bottom");var subQ1=sQuery(id+"F0.wireOp",EDGE,"E17.rect.left");Q83=makeQuery(id+"F3.opFillet","BLEND_EDGE",EDGE,{"blendedFrom":[makeQuery(id+"F1.opExtrude","SWEPT_EDGE",EDGE,{"disambiguationData":[OSD([subQ1,subQ0])]}),makeQuery(id+"F1.opExtrude","CAP_FACE",FACE,{"disambiguationData":[OSD([sQuery(id+"F0.wireOp",EDGE,"E0"),sQuery(id+"F0.wireOp",EDGE,"E1"),sQuery(id+"F0.wireOp",EDGE,"E2"),sQuery(id+"F0.wireOp",EDGE,"E3"),sQuery(id+"F0.wireOp",EDGE,"E4"),sQuery(id+"F0.wireOp",EDGE,"E5"),sQuery(id+"F0.wireOp",EDGE,"E6"),sQuery(id+"F0.wireOp",EDGE,"E7"),sQuery(id+"F0.wireOp",EDGE,"E8"),sQuery(id+"F0.wireOp",EDGE,"E9"),sQuery(id+"F0.wireOp",EDGE,"E10"),sQuery(id+"F0.wireOp",EDGE,"E11"),sQuery(id+"F0.wireOp",EDGE,"E12"),sQuery(id+"F0.wireOp",EDGE,"E13"),sQuery(id+"F0.wireOp",EDGE,"E14"),sQuery(id+"F0.wireOp",EDGE,"E15"),sQuery(id+"F0.wireOp",EDGE,"E17.rect.bottom"),sQuery(id+"F0.wireOp",EDGE,"E17.rect.top"),subQ1,sQuery(id+"F0.wireOp",EDGE,"E17.rect.right"),sQuery(id+"F0.wireOp",EDGE,"E18.rect.bottom"),sQuery(id+"F0.wireOp",EDGE,"E18.rect.top"),sQuery(id+"F0.wireOp",EDGE,"E18.rect.left"),sQuery(id+"F0.wireOp",EDGE,"E18.rect.right"),sQuery(id+"F0.wireOp",EDGE,"E19.rect.left"),sQuery(id+"F0.wireOp",EDGE,"E19.rect.right"),subQ0,sQuery(id+"F0.wireOp",EDGE,"E20.rect.top"),sQuery(id+"F0.wireOp",EDGE,"E23.top"),sQuery(id+"F0.wireOp",EDGE,"E23.left"),sQuery(id+"F0.wireOp",EDGE,"E23.right"),sQuery(id+"F0.wireOp",EDGE,"E24.top"),sQuery(id+"F0.wireOp",EDGE,"E24.left"),sQuery(id+"F0.wireOp",EDGE,"E24.right"),sQuery(id+"F0.wireOp",EDGE,"E25.top"),sQuery(id+"F0.wireOp",EDGE,"E25.left"),sQuery(id+"F0.wireOp",EDGE,"E25.right"),sQuery(id+"F0.wireOp",EDGE,"E26.top"),sQuery(id+"F0.wireOp",EDGE,"E26.left"),sQuery(id+"F0.wireOp",EDGE,"E26.right")])],"isStart":false})],"blendedInto":[makeQuery(id+"F1.opExtrude","CAP_FACE",FACE,{"disambiguationData":[OSD([sQuery(id+"F0.wireOp",EDGE,"E0"),sQuery(id+"F0.wireOp",EDGE,"E1"),sQuery(id+"F0.wireOp",EDGE,"E2"),sQuery(id+"F0.wireOp",EDGE,"E3"),sQuery(id+"F0.wireOp",EDGE,"E4"),sQuery(id+"F0.wireOp",EDGE,"E5"),sQuery(id+"F0.wireOp",EDGE,"E6"),sQuery(id+"F0.wireOp",EDGE,"E7"),sQuery(id+"F0.wireOp",EDGE,"E8"),sQuery(id+"F0.wireOp",EDGE,"E9"),sQuery(id+"F0.wireOp",EDGE,"E10"),sQuery(id+"F0.wireOp",EDGE,"E11"),sQuery(id+"F0.wireOp",EDGE,"E12"),sQuery(id+"F0.wireOp",EDGE,"E13"),sQuery(id+"F0.wireOp",EDGE,"E14"),sQuery(id+"F0.wireOp",EDGE,"E15"),sQuery(id+"F0.wireOp",EDGE,"E17.rect.bottom"),sQuery(id+"F0.wireOp",EDGE,"E17.rect.top"),subQ1,sQuery(id+"F0.wireOp",EDGE,"E17.rect.right"),sQuery(id+"F0.wireOp",EDGE,"E18.rect.bottom"),sQuery(id+"F0.wireOp",EDGE,"E18.rect.top"),sQuery(id+"F0.wireOp",EDGE,"E18.rect.left"),sQuery(id+"F0.wireOp",EDGE,"E18.rect.right"),sQuery(id+"F0.wireOp",EDGE,"E19.rect.left"),sQuery(id+"F0.wireOp",EDGE,"E19.rect.right"),subQ0,sQuery(id+"F0.wireOp",EDGE,"E20.rect.top"),sQuery(id+"F0.wireOp",EDGE,"E23.top"),sQuery(id+"F0.wireOp",EDGE,"E23.left"),sQuery(id+"F0.wireOp",EDGE,"E23.right"),sQuery(id+"F0.wireOp",EDGE,"E24.top"),sQuery(id+"F0.wireOp",EDGE,"E24.left"),sQuery(id+"F0.wireOp",EDGE,"E24.right"),sQuery(id+"F0.wireOp",EDGE,"E25.top"),sQuery(id+"F0.wireOp",EDGE,"E25.left"),sQuery(id+"F0.wireOp",EDGE,"E25.right"),sQuery(id+"F0.wireOp",EDGE,"E26.top"),sQuery(id+"F0.wireOp",EDGE,"E26.left"),sQuery(id+"F0.wireOp",EDGE,"E26.right")])],"isStart":false})]});}
            var Q84;
            {var subQ0=sQuery(id+"F0.wireOp",EDGE,"E20.rect.bottom");Q84=makeQuery(id+"F1.opExtrude","CAP_EDGE",EDGE,{"disambiguationData":[OSD([subQ0]),TDD([makeQuery(id+"F0.imprint","IMPRINT",EDGE,{"disambiguationData":[TD([[makeQuery(id+"F0.imprint","INTERSECT",VERTEX,{"derivedFrom":[sQuery(id+"F0.wireOp",EDGE,"E12"),subQ0]}),-1.0]])],"derivedFrom":subQ0})])],"isStart":false});}
            var Q85;
            {var subQ0=sQuery(id+"F0.wireOp",EDGE,"E20.rect.bottom");var subQ1=sQuery(id+"F0.wireOp",EDGE,"E12");Q85=makeQuery(id+"F3.opFillet","BLEND_EDGE",EDGE,{"blendedFrom":[makeQuery(id+"F1.opExtrude","SWEPT_EDGE",EDGE,{"disambiguationData":[OSD([subQ1,subQ0])]}),makeQuery(id+"F1.opExtrude","CAP_FACE",FACE,{"disambiguationData":[OSD([sQuery(id+"F0.wireOp",EDGE,"E0"),sQuery(id+"F0.wireOp",EDGE,"E1"),sQuery(id+"F0.wireOp",EDGE,"E2"),sQuery(id+"F0.wireOp",EDGE,"E3"),sQuery(id+"F0.wireOp",EDGE,"E4"),sQuery(id+"F0.wireOp",EDGE,"E5"),sQuery(id+"F0.wireOp",EDGE,"E6"),sQuery(id+"F0.wireOp",EDGE,"E7"),sQuery(id+"F0.wireOp",EDGE,"E8"),sQuery(id+"F0.wireOp",EDGE,"E9"),sQuery(id+"F0.wireOp",EDGE,"E10"),sQuery(id+"F0.wireOp",EDGE,"E11"),subQ1,sQuery(id+"F0.wireOp",EDGE,"E13"),sQuery(id+"F0.wireOp",EDGE,"E14"),sQuery(id+"F0.wireOp",EDGE,"E15"),sQuery(id+"F0.wireOp",EDGE,"E17.rect.bottom"),sQuery(id+"F0.wireOp",EDGE,"E17.rect.top"),sQuery(id+"F0.wireOp",EDGE,"E17.rect.left"),sQuery(id+"F0.wireOp",EDGE,"E17.rect.right"),sQuery(id+"F0.wireOp",EDGE,"E18.rect.bottom"),sQuery(id+"F0.wireOp",EDGE,"E18.rect.top"),sQuery(id+"F0.wireOp",EDGE,"E18.rect.left"),sQuery(id+"F0.wireOp",EDGE,"E18.rect.right"),sQuery(id+"F0.wireOp",EDGE,"E19.rect.left"),sQuery(id+"F0.wireOp",EDGE,"E19.rect.right"),subQ0,sQuery(id+"F0.wireOp",EDGE,"E20.rect.top"),sQuery(id+"F0.wireOp",EDGE,"E23.top"),sQuery(id+"F0.wireOp",EDGE,"E23.left"),sQuery(id+"F0.wireOp",EDGE,"E23.right"),sQuery(id+"F0.wireOp",EDGE,"E24.top"),sQuery(id+"F0.wireOp",EDGE,"E24.left"),sQuery(id+"F0.wireOp",EDGE,"E24.right"),sQuery(id+"F0.wireOp",EDGE,"E25.top"),sQuery(id+"F0.wireOp",EDGE,"E25.left"),sQuery(id+"F0.wireOp",EDGE,"E25.right"),sQuery(id+"F0.wireOp",EDGE,"E26.top"),sQuery(id+"F0.wireOp",EDGE,"E26.left"),sQuery(id+"F0.wireOp",EDGE,"E26.right")])],"isStart":false})],"blendedInto":[makeQuery(id+"F1.opExtrude","CAP_FACE",FACE,{"disambiguationData":[OSD([sQuery(id+"F0.wireOp",EDGE,"E0"),sQuery(id+"F0.wireOp",EDGE,"E1"),sQuery(id+"F0.wireOp",EDGE,"E2"),sQuery(id+"F0.wireOp",EDGE,"E3"),sQuery(id+"F0.wireOp",EDGE,"E4"),sQuery(id+"F0.wireOp",EDGE,"E5"),sQuery(id+"F0.wireOp",EDGE,"E6"),sQuery(id+"F0.wireOp",EDGE,"E7"),sQuery(id+"F0.wireOp",EDGE,"E8"),sQuery(id+"F0.wireOp",EDGE,"E9"),sQuery(id+"F0.wireOp",EDGE,"E10"),sQuery(id+"F0.wireOp",EDGE,"E11"),subQ1,sQuery(id+"F0.wireOp",EDGE,"E13"),sQuery(id+"F0.wireOp",EDGE,"E14"),sQuery(id+"F0.wireOp",EDGE,"E15"),sQuery(id+"F0.wireOp",EDGE,"E17.rect.bottom"),sQuery(id+"F0.wireOp",EDGE,"E17.rect.top"),sQuery(id+"F0.wireOp",EDGE,"E17.rect.left"),sQuery(id+"F0.wireOp",EDGE,"E17.rect.right"),sQuery(id+"F0.wireOp",EDGE,"E18.rect.bottom"),sQuery(id+"F0.wireOp",EDGE,"E18.rect.top"),sQuery(id+"F0.wireOp",EDGE,"E18.rect.left"),sQuery(id+"F0.wireOp",EDGE,"E18.rect.right"),sQuery(id+"F0.wireOp",EDGE,"E19.rect.left"),sQuery(id+"F0.wireOp",EDGE,"E19.rect.right"),subQ0,sQuery(id+"F0.wireOp",EDGE,"E20.rect.top"),sQuery(id+"F0.wireOp",EDGE,"E23.top"),sQuery(id+"F0.wireOp",EDGE,"E23.left"),sQuery(id+"F0.wireOp",EDGE,"E23.right"),sQuery(id+"F0.wireOp",EDGE,"E24.top"),sQuery(id+"F0.wireOp",EDGE,"E24.left"),sQuery(id+"F0.wireOp",EDGE,"E24.right"),sQuery(id+"F0.wireOp",EDGE,"E25.top"),sQuery(id+"F0.wireOp",EDGE,"E25.left"),sQuery(id+"F0.wireOp",EDGE,"E25.right"),sQuery(id+"F0.wireOp",EDGE,"E26.top"),sQuery(id+"F0.wireOp",EDGE,"E26.left"),sQuery(id+"F0.wireOp",EDGE,"E26.right")])],"isStart":false})]});}
            var Q86;
            {var subQ0=sQuery(id+"F0.wireOp",EDGE,"E12");var subQ1=makeQuery(id+"F0.imprint","INTERSECT",VERTEX,{"disambiguationData":[OD(1.0)],"derivedFrom":[sQuery(id+"F0.wireOp",EDGE,"E7"),subQ0]});Q86=makeQuery(id+"F1.opExtrude","CAP_EDGE",EDGE,{"disambiguationData":[OSD([subQ0]),TDD([makeQuery(id+"F0.imprint","IMPRINT",EDGE,{"disambiguationData":[TD([[makeQuery(id+"F0.imprint","INTERSECT",VERTEX,{"disambiguationData":[OD(1.0)],"derivedFrom":[sQuery(id+"F0.wireOp",EDGE,"E1"),subQ0]}),-1.0]])],"derivedFrom":subQ0}),makeQuery(id+"F0.imprint","IMPRINT",EDGE,{"disambiguationData":[TD([[subQ1,-1.0]])],"derivedFrom":subQ0})])],"isStart":false});}
            var Q87;
            {var subQ0=sQuery(id+"F0.wireOp",EDGE,"E10");var subQ1=makeQuery(id+"F0.imprint","INTERSECT",VERTEX,{"disambiguationData":[OD(1.0)],"derivedFrom":[sQuery(id+"F0.wireOp",EDGE,"E7"),subQ0]});Q87=makeQuery(id+"F1.opExtrude","CAP_EDGE",EDGE,{"disambiguationData":[OSD([subQ0]),TDD([makeQuery(id+"F0.imprint","IMPRINT",EDGE,{"disambiguationData":[TD([[subQ1,1.0]])],"derivedFrom":subQ0}),makeQuery(id+"F0.imprint","IMPRINT",EDGE,{"disambiguationData":[TD([[makeQuery(id+"F0.imprint","INTERSECT",VERTEX,{"disambiguationData":[OD(1.0)],"derivedFrom":[sQuery(id+"F0.wireOp",EDGE,"E1"),subQ0]}),1.0]])],"derivedFrom":subQ0})])],"isStart":false});}
            var Q88;
            {var subQ0=sQuery(id+"F0.wireOp",EDGE,"E19.rect.left");var subQ1=sQuery(id+"F0.wireOp",EDGE,"E10");Q88=makeQuery(id+"F3.opFillet","BLEND_EDGE",EDGE,{"blendedFrom":[makeQuery(id+"F1.opExtrude","SWEPT_EDGE",EDGE,{"disambiguationData":[OSD([subQ1,subQ0])]}),makeQuery(id+"F1.opExtrude","CAP_FACE",FACE,{"disambiguationData":[OSD([sQuery(id+"F0.wireOp",EDGE,"E0"),sQuery(id+"F0.wireOp",EDGE,"E1"),sQuery(id+"F0.wireOp",EDGE,"E2"),sQuery(id+"F0.wireOp",EDGE,"E3"),sQuery(id+"F0.wireOp",EDGE,"E4"),sQuery(id+"F0.wireOp",EDGE,"E5"),sQuery(id+"F0.wireOp",EDGE,"E6"),sQuery(id+"F0.wireOp",EDGE,"E7"),sQuery(id+"F0.wireOp",EDGE,"E8"),sQuery(id+"F0.wireOp",EDGE,"E9"),subQ1,sQuery(id+"F0.wireOp",EDGE,"E11"),sQuery(id+"F0.wireOp",EDGE,"E12"),sQuery(id+"F0.wireOp",EDGE,"E13"),sQuery(id+"F0.wireOp",EDGE,"E14"),sQuery(id+"F0.wireOp",EDGE,"E15"),sQuery(id+"F0.wireOp",EDGE,"E17.rect.bottom"),sQuery(id+"F0.wireOp",EDGE,"E17.rect.top"),sQuery(id+"F0.wireOp",EDGE,"E17.rect.left"),sQuery(id+"F0.wireOp",EDGE,"E17.rect.right"),sQuery(id+"F0.wireOp",EDGE,"E18.rect.bottom"),sQuery(id+"F0.wireOp",EDGE,"E18.rect.top"),sQuery(id+"F0.wireOp",EDGE,"E18.rect.left"),sQuery(id+"F0.wireOp",EDGE,"E18.rect.right"),subQ0,sQuery(id+"F0.wireOp",EDGE,"E19.rect.right"),sQuery(id+"F0.wireOp",EDGE,"E20.rect.bottom"),sQuery(id+"F0.wireOp",EDGE,"E20.rect.top"),sQuery(id+"F0.wireOp",EDGE,"E23.top"),sQuery(id+"F0.wireOp",EDGE,"E23.left"),sQuery(id+"F0.wireOp",EDGE,"E23.right"),sQuery(id+"F0.wireOp",EDGE,"E24.top"),sQuery(id+"F0.wireOp",EDGE,"E24.left"),sQuery(id+"F0.wireOp",EDGE,"E24.right"),sQuery(id+"F0.wireOp",EDGE,"E25.top"),sQuery(id+"F0.wireOp",EDGE,"E25.left"),sQuery(id+"F0.wireOp",EDGE,"E25.right"),sQuery(id+"F0.wireOp",EDGE,"E26.top"),sQuery(id+"F0.wireOp",EDGE,"E26.left"),sQuery(id+"F0.wireOp",EDGE,"E26.right")])],"isStart":false})],"blendedInto":[makeQuery(id+"F1.opExtrude","CAP_FACE",FACE,{"disambiguationData":[OSD([sQuery(id+"F0.wireOp",EDGE,"E0"),sQuery(id+"F0.wireOp",EDGE,"E1"),sQuery(id+"F0.wireOp",EDGE,"E2"),sQuery(id+"F0.wireOp",EDGE,"E3"),sQuery(id+"F0.wireOp",EDGE,"E4"),sQuery(id+"F0.wireOp",EDGE,"E5"),sQuery(id+"F0.wireOp",EDGE,"E6"),sQuery(id+"F0.wireOp",EDGE,"E7"),sQuery(id+"F0.wireOp",EDGE,"E8"),sQuery(id+"F0.wireOp",EDGE,"E9"),subQ1,sQuery(id+"F0.wireOp",EDGE,"E11"),sQuery(id+"F0.wireOp",EDGE,"E12"),sQuery(id+"F0.wireOp",EDGE,"E13"),sQuery(id+"F0.wireOp",EDGE,"E14"),sQuery(id+"F0.wireOp",EDGE,"E15"),sQuery(id+"F0.wireOp",EDGE,"E17.rect.bottom"),sQuery(id+"F0.wireOp",EDGE,"E17.rect.top"),sQuery(id+"F0.wireOp",EDGE,"E17.rect.left"),sQuery(id+"F0.wireOp",EDGE,"E17.rect.right"),sQuery(id+"F0.wireOp",EDGE,"E18.rect.bottom"),sQuery(id+"F0.wireOp",EDGE,"E18.rect.top"),sQuery(id+"F0.wireOp",EDGE,"E18.rect.left"),sQuery(id+"F0.wireOp",EDGE,"E18.rect.right"),subQ0,sQuery(id+"F0.wireOp",EDGE,"E19.rect.right"),sQuery(id+"F0.wireOp",EDGE,"E20.rect.bottom"),sQuery(id+"F0.wireOp",EDGE,"E20.rect.top"),sQuery(id+"F0.wireOp",EDGE,"E23.top"),sQuery(id+"F0.wireOp",EDGE,"E23.left"),sQuery(id+"F0.wireOp",EDGE,"E23.right"),sQuery(id+"F0.wireOp",EDGE,"E24.top"),sQuery(id+"F0.wireOp",EDGE,"E24.left"),sQuery(id+"F0.wireOp",EDGE,"E24.right"),sQuery(id+"F0.wireOp",EDGE,"E25.top"),sQuery(id+"F0.wireOp",EDGE,"E25.left"),sQuery(id+"F0.wireOp",EDGE,"E25.right"),sQuery(id+"F0.wireOp",EDGE,"E26.top"),sQuery(id+"F0.wireOp",EDGE,"E26.left"),sQuery(id+"F0.wireOp",EDGE,"E26.right")])],"isStart":false})]});}
            var Q89;
            {var subQ0=sQuery(id+"F0.wireOp",EDGE,"E19.rect.left");Q89=makeQuery(id+"F1.opExtrude","CAP_EDGE",EDGE,{"disambiguationData":[OSD([subQ0]),TDD([makeQuery(id+"F0.imprint","IMPRINT",EDGE,{"disambiguationData":[TD([[makeQuery(id+"F0.imprint","INTERSECT",VERTEX,{"derivedFrom":[sQuery(id+"F0.wireOp",EDGE,"E10"),subQ0]}),-1.0]])],"derivedFrom":subQ0})])],"isStart":false});}
            var Q90;
            {var subQ0=sQuery(id+"F0.wireOp",EDGE,"E19.rect.left");var subQ1=sQuery(id+"F0.wireOp",EDGE,"E17.rect.bottom");Q90=makeQuery(id+"F3.opFillet","BLEND_EDGE",EDGE,{"blendedFrom":[makeQuery(id+"F1.opExtrude","SWEPT_EDGE",EDGE,{"disambiguationData":[OSD([subQ1,subQ0])]}),makeQuery(id+"F1.opExtrude","CAP_FACE",FACE,{"disambiguationData":[OSD([sQuery(id+"F0.wireOp",EDGE,"E0"),sQuery(id+"F0.wireOp",EDGE,"E1"),sQuery(id+"F0.wireOp",EDGE,"E2"),sQuery(id+"F0.wireOp",EDGE,"E3"),sQuery(id+"F0.wireOp",EDGE,"E4"),sQuery(id+"F0.wireOp",EDGE,"E5"),sQuery(id+"F0.wireOp",EDGE,"E6"),sQuery(id+"F0.wireOp",EDGE,"E7"),sQuery(id+"F0.wireOp",EDGE,"E8"),sQuery(id+"F0.wireOp",EDGE,"E9"),sQuery(id+"F0.wireOp",EDGE,"E10"),sQuery(id+"F0.wireOp",EDGE,"E11"),sQuery(id+"F0.wireOp",EDGE,"E12"),sQuery(id+"F0.wireOp",EDGE,"E13"),sQuery(id+"F0.wireOp",EDGE,"E14"),sQuery(id+"F0.wireOp",EDGE,"E15"),subQ1,sQuery(id+"F0.wireOp",EDGE,"E17.rect.top"),sQuery(id+"F0.wireOp",EDGE,"E17.rect.left"),sQuery(id+"F0.wireOp",EDGE,"E17.rect.right"),sQuery(id+"F0.wireOp",EDGE,"E18.rect.bottom"),sQuery(id+"F0.wireOp",EDGE,"E18.rect.top"),sQuery(id+"F0.wireOp",EDGE,"E18.rect.left"),sQuery(id+"F0.wireOp",EDGE,"E18.rect.right"),subQ0,sQuery(id+"F0.wireOp",EDGE,"E19.rect.right"),sQuery(id+"F0.wireOp",EDGE,"E20.rect.bottom"),sQuery(id+"F0.wireOp",EDGE,"E20.rect.top"),sQuery(id+"F0.wireOp",EDGE,"E23.top"),sQuery(id+"F0.wireOp",EDGE,"E23.left"),sQuery(id+"F0.wireOp",EDGE,"E23.right"),sQuery(id+"F0.wireOp",EDGE,"E24.top"),sQuery(id+"F0.wireOp",EDGE,"E24.left"),sQuery(id+"F0.wireOp",EDGE,"E24.right"),sQuery(id+"F0.wireOp",EDGE,"E25.top"),sQuery(id+"F0.wireOp",EDGE,"E25.left"),sQuery(id+"F0.wireOp",EDGE,"E25.right"),sQuery(id+"F0.wireOp",EDGE,"E26.top"),sQuery(id+"F0.wireOp",EDGE,"E26.left"),sQuery(id+"F0.wireOp",EDGE,"E26.right")])],"isStart":false})],"blendedInto":[makeQuery(id+"F1.opExtrude","CAP_FACE",FACE,{"disambiguationData":[OSD([sQuery(id+"F0.wireOp",EDGE,"E0"),sQuery(id+"F0.wireOp",EDGE,"E1"),sQuery(id+"F0.wireOp",EDGE,"E2"),sQuery(id+"F0.wireOp",EDGE,"E3"),sQuery(id+"F0.wireOp",EDGE,"E4"),sQuery(id+"F0.wireOp",EDGE,"E5"),sQuery(id+"F0.wireOp",EDGE,"E6"),sQuery(id+"F0.wireOp",EDGE,"E7"),sQuery(id+"F0.wireOp",EDGE,"E8"),sQuery(id+"F0.wireOp",EDGE,"E9"),sQuery(id+"F0.wireOp",EDGE,"E10"),sQuery(id+"F0.wireOp",EDGE,"E11"),sQuery(id+"F0.wireOp",EDGE,"E12"),sQuery(id+"F0.wireOp",EDGE,"E13"),sQuery(id+"F0.wireOp",EDGE,"E14"),sQuery(id+"F0.wireOp",EDGE,"E15"),subQ1,sQuery(id+"F0.wireOp",EDGE,"E17.rect.top"),sQuery(id+"F0.wireOp",EDGE,"E17.rect.left"),sQuery(id+"F0.wireOp",EDGE,"E17.rect.right"),sQuery(id+"F0.wireOp",EDGE,"E18.rect.bottom"),sQuery(id+"F0.wireOp",EDGE,"E18.rect.top"),sQuery(id+"F0.wireOp",EDGE,"E18.rect.left"),sQuery(id+"F0.wireOp",EDGE,"E18.rect.right"),subQ0,sQuery(id+"F0.wireOp",EDGE,"E19.rect.right"),sQuery(id+"F0.wireOp",EDGE,"E20.rect.bottom"),sQuery(id+"F0.wireOp",EDGE,"E20.rect.top"),sQuery(id+"F0.wireOp",EDGE,"E23.top"),sQuery(id+"F0.wireOp",EDGE,"E23.left"),sQuery(id+"F0.wireOp",EDGE,"E23.right"),sQuery(id+"F0.wireOp",EDGE,"E24.top"),sQuery(id+"F0.wireOp",EDGE,"E24.left"),sQuery(id+"F0.wireOp",EDGE,"E24.right"),sQuery(id+"F0.wireOp",EDGE,"E25.top"),sQuery(id+"F0.wireOp",EDGE,"E25.left"),sQuery(id+"F0.wireOp",EDGE,"E25.right"),sQuery(id+"F0.wireOp",EDGE,"E26.top"),sQuery(id+"F0.wireOp",EDGE,"E26.left"),sQuery(id+"F0.wireOp",EDGE,"E26.right")])],"isStart":false})]});}
            var Q91;
            {var subQ0=sQuery(id+"F0.wireOp",EDGE,"E17.rect.bottom");Q91=makeQuery(id+"F1.opExtrude","CAP_EDGE",EDGE,{"disambiguationData":[OSD([subQ0]),TDD([makeQuery(id+"F0.imprint","IMPRINT",EDGE,{"disambiguationData":[TD([[makeQuery(id+"F0.imprint","INTERSECT",VERTEX,{"derivedFrom":[subQ0,sQuery(id+"F0.wireOp",EDGE,"E19.rect.left")]}),1.0]])],"derivedFrom":subQ0})])],"isStart":false});}
            var Q92;
            Q92=makeQuery(id+"F1.opExtrude","CAP_EDGE",EDGE,{"disambiguationData":[OSD([sQuery(id+"F0.wireOp",EDGE,"E26.right")])],"isStart":false});
            var Q93;
            Q93=makeQuery(id+"F1.opExtrude","CAP_EDGE",EDGE,{"disambiguationData":[OSD([sQuery(id+"F0.wireOp",EDGE,"E23.right")])],"isStart":false});
            var Q94;
            {var subQ0=sQuery(id+"F0.wireOp",EDGE,"E17.rect.bottom");Q94=makeQuery(id+"F1.opExtrude","CAP_EDGE",EDGE,{"disambiguationData":[OSD([subQ0]),TDD([makeQuery(id+"F0.imprint","IMPRINT",EDGE,{"disambiguationData":[TD([[makeQuery(id+"F0.imprint","INTERSECT",VERTEX,{"derivedFrom":[subQ0,sQuery(id+"F0.wireOp",EDGE,"E19.rect.right")]}),-1.0]])],"derivedFrom":subQ0})])],"isStart":false});}
            var Q95;
            {var subQ0=sQuery(id+"F0.wireOp",EDGE,"E19.rect.right");var subQ1=sQuery(id+"F0.wireOp",EDGE,"E17.rect.bottom");Q95=makeQuery(id+"F3.opFillet","BLEND_EDGE",EDGE,{"blendedFrom":[makeQuery(id+"F1.opExtrude","SWEPT_EDGE",EDGE,{"disambiguationData":[OSD([subQ1,subQ0])]}),makeQuery(id+"F1.opExtrude","CAP_FACE",FACE,{"disambiguationData":[OSD([sQuery(id+"F0.wireOp",EDGE,"E0"),sQuery(id+"F0.wireOp",EDGE,"E1"),sQuery(id+"F0.wireOp",EDGE,"E2"),sQuery(id+"F0.wireOp",EDGE,"E3"),sQuery(id+"F0.wireOp",EDGE,"E4"),sQuery(id+"F0.wireOp",EDGE,"E5"),sQuery(id+"F0.wireOp",EDGE,"E6"),sQuery(id+"F0.wireOp",EDGE,"E7"),sQuery(id+"F0.wireOp",EDGE,"E8"),sQuery(id+"F0.wireOp",EDGE,"E9"),sQuery(id+"F0.wireOp",EDGE,"E10"),sQuery(id+"F0.wireOp",EDGE,"E11"),sQuery(id+"F0.wireOp",EDGE,"E12"),sQuery(id+"F0.wireOp",EDGE,"E13"),sQuery(id+"F0.wireOp",EDGE,"E14"),sQuery(id+"F0.wireOp",EDGE,"E15"),subQ1,sQuery(id+"F0.wireOp",EDGE,"E17.rect.top"),sQuery(id+"F0.wireOp",EDGE,"E17.rect.left"),sQuery(id+"F0.wireOp",EDGE,"E17.rect.right"),sQuery(id+"F0.wireOp",EDGE,"E18.rect.bottom"),sQuery(id+"F0.wireOp",EDGE,"E18.rect.top"),sQuery(id+"F0.wireOp",EDGE,"E18.rect.left"),sQuery(id+"F0.wireOp",EDGE,"E18.rect.right"),sQuery(id+"F0.wireOp",EDGE,"E19.rect.left"),subQ0,sQuery(id+"F0.wireOp",EDGE,"E20.rect.bottom"),sQuery(id+"F0.wireOp",EDGE,"E20.rect.top"),sQuery(id+"F0.wireOp",EDGE,"E23.top"),sQuery(id+"F0.wireOp",EDGE,"E23.left"),sQuery(id+"F0.wireOp",EDGE,"E23.right"),sQuery(id+"F0.wireOp",EDGE,"E24.top"),sQuery(id+"F0.wireOp",EDGE,"E24.left"),sQuery(id+"F0.wireOp",EDGE,"E24.right"),sQuery(id+"F0.wireOp",EDGE,"E25.top"),sQuery(id+"F0.wireOp",EDGE,"E25.left"),sQuery(id+"F0.wireOp",EDGE,"E25.right"),sQuery(id+"F0.wireOp",EDGE,"E26.top"),sQuery(id+"F0.wireOp",EDGE,"E26.left"),sQuery(id+"F0.wireOp",EDGE,"E26.right")])],"isStart":false})],"blendedInto":[makeQuery(id+"F1.opExtrude","CAP_FACE",FACE,{"disambiguationData":[OSD([sQuery(id+"F0.wireOp",EDGE,"E0"),sQuery(id+"F0.wireOp",EDGE,"E1"),sQuery(id+"F0.wireOp",EDGE,"E2"),sQuery(id+"F0.wireOp",EDGE,"E3"),sQuery(id+"F0.wireOp",EDGE,"E4"),sQuery(id+"F0.wireOp",EDGE,"E5"),sQuery(id+"F0.wireOp",EDGE,"E6"),sQuery(id+"F0.wireOp",EDGE,"E7"),sQuery(id+"F0.wireOp",EDGE,"E8"),sQuery(id+"F0.wireOp",EDGE,"E9"),sQuery(id+"F0.wireOp",EDGE,"E10"),sQuery(id+"F0.wireOp",EDGE,"E11"),sQuery(id+"F0.wireOp",EDGE,"E12"),sQuery(id+"F0.wireOp",EDGE,"E13"),sQuery(id+"F0.wireOp",EDGE,"E14"),sQuery(id+"F0.wireOp",EDGE,"E15"),subQ1,sQuery(id+"F0.wireOp",EDGE,"E17.rect.top"),sQuery(id+"F0.wireOp",EDGE,"E17.rect.left"),sQuery(id+"F0.wireOp",EDGE,"E17.rect.right"),sQuery(id+"F0.wireOp",EDGE,"E18.rect.bottom"),sQuery(id+"F0.wireOp",EDGE,"E18.rect.top"),sQuery(id+"F0.wireOp",EDGE,"E18.rect.left"),sQuery(id+"F0.wireOp",EDGE,"E18.rect.right"),sQuery(id+"F0.wireOp",EDGE,"E19.rect.left"),subQ0,sQuery(id+"F0.wireOp",EDGE,"E20.rect.bottom"),sQuery(id+"F0.wireOp",EDGE,"E20.rect.top"),sQuery(id+"F0.wireOp",EDGE,"E23.top"),sQuery(id+"F0.wireOp",EDGE,"E23.left"),sQuery(id+"F0.wireOp",EDGE,"E23.right"),sQuery(id+"F0.wireOp",EDGE,"E24.top"),sQuery(id+"F0.wireOp",EDGE,"E24.left"),sQuery(id+"F0.wireOp",EDGE,"E24.right"),sQuery(id+"F0.wireOp",EDGE,"E25.top"),sQuery(id+"F0.wireOp",EDGE,"E25.left"),sQuery(id+"F0.wireOp",EDGE,"E25.right"),sQuery(id+"F0.wireOp",EDGE,"E26.top"),sQuery(id+"F0.wireOp",EDGE,"E26.left"),sQuery(id+"F0.wireOp",EDGE,"E26.right")])],"isStart":false})]});}
            var Q96;
            {var subQ0=sQuery(id+"F0.wireOp",EDGE,"E19.rect.right");Q96=makeQuery(id+"F1.opExtrude","CAP_EDGE",EDGE,{"disambiguationData":[OSD([subQ0]),TDD([makeQuery(id+"F0.imprint","IMPRINT",EDGE,{"disambiguationData":[TD([[makeQuery(id+"F0.imprint","INTERSECT",VERTEX,{"derivedFrom":[sQuery(id+"F0.wireOp",EDGE,"E10"),subQ0]}),-1.0]])],"derivedFrom":subQ0})])],"isStart":false});}
            var Q97;
            {var subQ0=sQuery(id+"F0.wireOp",EDGE,"E19.rect.right");var subQ1=sQuery(id+"F0.wireOp",EDGE,"E10");Q97=makeQuery(id+"F3.opFillet","BLEND_EDGE",EDGE,{"blendedFrom":[makeQuery(id+"F1.opExtrude","SWEPT_EDGE",EDGE,{"disambiguationData":[OSD([subQ1,subQ0])]}),makeQuery(id+"F1.opExtrude","CAP_FACE",FACE,{"disambiguationData":[OSD([sQuery(id+"F0.wireOp",EDGE,"E0"),sQuery(id+"F0.wireOp",EDGE,"E1"),sQuery(id+"F0.wireOp",EDGE,"E2"),sQuery(id+"F0.wireOp",EDGE,"E3"),sQuery(id+"F0.wireOp",EDGE,"E4"),sQuery(id+"F0.wireOp",EDGE,"E5"),sQuery(id+"F0.wireOp",EDGE,"E6"),sQuery(id+"F0.wireOp",EDGE,"E7"),sQuery(id+"F0.wireOp",EDGE,"E8"),sQuery(id+"F0.wireOp",EDGE,"E9"),subQ1,sQuery(id+"F0.wireOp",EDGE,"E11"),sQuery(id+"F0.wireOp",EDGE,"E12"),sQuery(id+"F0.wireOp",EDGE,"E13"),sQuery(id+"F0.wireOp",EDGE,"E14"),sQuery(id+"F0.wireOp",EDGE,"E15"),sQuery(id+"F0.wireOp",EDGE,"E17.rect.bottom"),sQuery(id+"F0.wireOp",EDGE,"E17.rect.top"),sQuery(id+"F0.wireOp",EDGE,"E17.rect.left"),sQuery(id+"F0.wireOp",EDGE,"E17.rect.right"),sQuery(id+"F0.wireOp",EDGE,"E18.rect.bottom"),sQuery(id+"F0.wireOp",EDGE,"E18.rect.top"),sQuery(id+"F0.wireOp",EDGE,"E18.rect.left"),sQuery(id+"F0.wireOp",EDGE,"E18.rect.right"),sQuery(id+"F0.wireOp",EDGE,"E19.rect.left"),subQ0,sQuery(id+"F0.wireOp",EDGE,"E20.rect.bottom"),sQuery(id+"F0.wireOp",EDGE,"E20.rect.top"),sQuery(id+"F0.wireOp",EDGE,"E23.top"),sQuery(id+"F0.wireOp",EDGE,"E23.left"),sQuery(id+"F0.wireOp",EDGE,"E23.right"),sQuery(id+"F0.wireOp",EDGE,"E24.top"),sQuery(id+"F0.wireOp",EDGE,"E24.left"),sQuery(id+"F0.wireOp",EDGE,"E24.right"),sQuery(id+"F0.wireOp",EDGE,"E25.top"),sQuery(id+"F0.wireOp",EDGE,"E25.left"),sQuery(id+"F0.wireOp",EDGE,"E25.right"),sQuery(id+"F0.wireOp",EDGE,"E26.top"),sQuery(id+"F0.wireOp",EDGE,"E26.left"),sQuery(id+"F0.wireOp",EDGE,"E26.right")])],"isStart":false})],"blendedInto":[makeQuery(id+"F1.opExtrude","CAP_FACE",FACE,{"disambiguationData":[OSD([sQuery(id+"F0.wireOp",EDGE,"E0"),sQuery(id+"F0.wireOp",EDGE,"E1"),sQuery(id+"F0.wireOp",EDGE,"E2"),sQuery(id+"F0.wireOp",EDGE,"E3"),sQuery(id+"F0.wireOp",EDGE,"E4"),sQuery(id+"F0.wireOp",EDGE,"E5"),sQuery(id+"F0.wireOp",EDGE,"E6"),sQuery(id+"F0.wireOp",EDGE,"E7"),sQuery(id+"F0.wireOp",EDGE,"E8"),sQuery(id+"F0.wireOp",EDGE,"E9"),subQ1,sQuery(id+"F0.wireOp",EDGE,"E11"),sQuery(id+"F0.wireOp",EDGE,"E12"),sQuery(id+"F0.wireOp",EDGE,"E13"),sQuery(id+"F0.wireOp",EDGE,"E14"),sQuery(id+"F0.wireOp",EDGE,"E15"),sQuery(id+"F0.wireOp",EDGE,"E17.rect.bottom"),sQuery(id+"F0.wireOp",EDGE,"E17.rect.top"),sQuery(id+"F0.wireOp",EDGE,"E17.rect.left"),sQuery(id+"F0.wireOp",EDGE,"E17.rect.right"),sQuery(id+"F0.wireOp",EDGE,"E18.rect.bottom"),sQuery(id+"F0.wireOp",EDGE,"E18.rect.top"),sQuery(id+"F0.wireOp",EDGE,"E18.rect.left"),sQuery(id+"F0.wireOp",EDGE,"E18.rect.right"),sQuery(id+"F0.wireOp",EDGE,"E19.rect.left"),subQ0,sQuery(id+"F0.wireOp",EDGE,"E20.rect.bottom"),sQuery(id+"F0.wireOp",EDGE,"E20.rect.top"),sQuery(id+"F0.wireOp",EDGE,"E23.top"),sQuery(id+"F0.wireOp",EDGE,"E23.left"),sQuery(id+"F0.wireOp",EDGE,"E23.right"),sQuery(id+"F0.wireOp",EDGE,"E24.top"),sQuery(id+"F0.wireOp",EDGE,"E24.left"),sQuery(id+"F0.wireOp",EDGE,"E24.right"),sQuery(id+"F0.wireOp",EDGE,"E25.top"),sQuery(id+"F0.wireOp",EDGE,"E25.left"),sQuery(id+"F0.wireOp",EDGE,"E25.right"),sQuery(id+"F0.wireOp",EDGE,"E26.top"),sQuery(id+"F0.wireOp",EDGE,"E26.left"),sQuery(id+"F0.wireOp",EDGE,"E26.right")])],"isStart":false})]});}
            var Q98;
            {var subQ0=sQuery(id+"F0.wireOp",EDGE,"E10");var subQ1=makeQuery(id+"F0.imprint","INTERSECT",VERTEX,{"disambiguationData":[OD(1.0)],"derivedFrom":[sQuery(id+"F0.wireOp",EDGE,"E4"),subQ0]});Q98=makeQuery(id+"F1.opExtrude","CAP_EDGE",EDGE,{"disambiguationData":[OSD([subQ0]),TDD([makeQuery(id+"F0.imprint","IMPRINT",EDGE,{"disambiguationData":[TD([[makeQuery(id+"F0.imprint","INTERSECT",VERTEX,{"disambiguationData":[OD(1.0)],"derivedFrom":[sQuery(id+"F0.wireOp",EDGE,"E0"),subQ0]}),-1.0]])],"derivedFrom":subQ0}),makeQuery(id+"F0.imprint","IMPRINT",EDGE,{"disambiguationData":[TD([[subQ1,-1.0]])],"derivedFrom":subQ0})])],"isStart":false});}
            var Q99;
            {var subQ0=sQuery(id+"F0.wireOp",EDGE,"E8");var subQ1=makeQuery(id+"F0.imprint","INTERSECT",VERTEX,{"disambiguationData":[OD(1.0)],"derivedFrom":[sQuery(id+"F0.wireOp",EDGE,"E4"),subQ0]});Q99=makeQuery(id+"F1.opExtrude","CAP_EDGE",EDGE,{"disambiguationData":[OSD([subQ0]),TDD([makeQuery(id+"F0.imprint","IMPRINT",EDGE,{"disambiguationData":[TD([[subQ1,1.0]])],"derivedFrom":subQ0}),makeQuery(id+"F0.imprint","IMPRINT",EDGE,{"disambiguationData":[TD([[makeQuery(id+"F0.imprint","INTERSECT",VERTEX,{"disambiguationData":[OD(1.0)],"derivedFrom":[sQuery(id+"F0.wireOp",EDGE,"E0"),subQ0]}),1.0]])],"derivedFrom":subQ0})])],"isStart":false});}
            var Q100;
            {var subQ0=sQuery(id+"F0.wireOp",EDGE,"E20.rect.bottom");var subQ1=sQuery(id+"F0.wireOp",EDGE,"E8");Q100=makeQuery(id+"F3.opFillet","BLEND_EDGE",EDGE,{"blendedFrom":[makeQuery(id+"F1.opExtrude","SWEPT_EDGE",EDGE,{"disambiguationData":[OSD([subQ1,subQ0])]}),makeQuery(id+"F1.opExtrude","CAP_FACE",FACE,{"disambiguationData":[OSD([sQuery(id+"F0.wireOp",EDGE,"E0"),sQuery(id+"F0.wireOp",EDGE,"E1"),sQuery(id+"F0.wireOp",EDGE,"E2"),sQuery(id+"F0.wireOp",EDGE,"E3"),sQuery(id+"F0.wireOp",EDGE,"E4"),sQuery(id+"F0.wireOp",EDGE,"E5"),sQuery(id+"F0.wireOp",EDGE,"E6"),sQuery(id+"F0.wireOp",EDGE,"E7"),subQ1,sQuery(id+"F0.wireOp",EDGE,"E9"),sQuery(id+"F0.wireOp",EDGE,"E10"),sQuery(id+"F0.wireOp",EDGE,"E11"),sQuery(id+"F0.wireOp",EDGE,"E12"),sQuery(id+"F0.wireOp",EDGE,"E13"),sQuery(id+"F0.wireOp",EDGE,"E14"),sQuery(id+"F0.wireOp",EDGE,"E15"),sQuery(id+"F0.wireOp",EDGE,"E17.rect.bottom"),sQuery(id+"F0.wireOp",EDGE,"E17.rect.top"),sQuery(id+"F0.wireOp",EDGE,"E17.rect.left"),sQuery(id+"F0.wireOp",EDGE,"E17.rect.right"),sQuery(id+"F0.wireOp",EDGE,"E18.rect.bottom"),sQuery(id+"F0.wireOp",EDGE,"E18.rect.top"),sQuery(id+"F0.wireOp",EDGE,"E18.rect.left"),sQuery(id+"F0.wireOp",EDGE,"E18.rect.right"),sQuery(id+"F0.wireOp",EDGE,"E19.rect.left"),sQuery(id+"F0.wireOp",EDGE,"E19.rect.right"),subQ0,sQuery(id+"F0.wireOp",EDGE,"E20.rect.top"),sQuery(id+"F0.wireOp",EDGE,"E23.top"),sQuery(id+"F0.wireOp",EDGE,"E23.left"),sQuery(id+"F0.wireOp",EDGE,"E23.right"),sQuery(id+"F0.wireOp",EDGE,"E24.top"),sQuery(id+"F0.wireOp",EDGE,"E24.left"),sQuery(id+"F0.wireOp",EDGE,"E24.right"),sQuery(id+"F0.wireOp",EDGE,"E25.top"),sQuery(id+"F0.wireOp",EDGE,"E25.left"),sQuery(id+"F0.wireOp",EDGE,"E25.right"),sQuery(id+"F0.wireOp",EDGE,"E26.top"),sQuery(id+"F0.wireOp",EDGE,"E26.left"),sQuery(id+"F0.wireOp",EDGE,"E26.right")])],"isStart":false})],"blendedInto":[makeQuery(id+"F1.opExtrude","CAP_FACE",FACE,{"disambiguationData":[OSD([sQuery(id+"F0.wireOp",EDGE,"E0"),sQuery(id+"F0.wireOp",EDGE,"E1"),sQuery(id+"F0.wireOp",EDGE,"E2"),sQuery(id+"F0.wireOp",EDGE,"E3"),sQuery(id+"F0.wireOp",EDGE,"E4"),sQuery(id+"F0.wireOp",EDGE,"E5"),sQuery(id+"F0.wireOp",EDGE,"E6"),sQuery(id+"F0.wireOp",EDGE,"E7"),subQ1,sQuery(id+"F0.wireOp",EDGE,"E9"),sQuery(id+"F0.wireOp",EDGE,"E10"),sQuery(id+"F0.wireOp",EDGE,"E11"),sQuery(id+"F0.wireOp",EDGE,"E12"),sQuery(id+"F0.wireOp",EDGE,"E13"),sQuery(id+"F0.wireOp",EDGE,"E14"),sQuery(id+"F0.wireOp",EDGE,"E15"),sQuery(id+"F0.wireOp",EDGE,"E17.rect.bottom"),sQuery(id+"F0.wireOp",EDGE,"E17.rect.top"),sQuery(id+"F0.wireOp",EDGE,"E17.rect.left"),sQuery(id+"F0.wireOp",EDGE,"E17.rect.right"),sQuery(id+"F0.wireOp",EDGE,"E18.rect.bottom"),sQuery(id+"F0.wireOp",EDGE,"E18.rect.top"),sQuery(id+"F0.wireOp",EDGE,"E18.rect.left"),sQuery(id+"F0.wireOp",EDGE,"E18.rect.right"),sQuery(id+"F0.wireOp",EDGE,"E19.rect.left"),sQuery(id+"F0.wireOp",EDGE,"E19.rect.right"),subQ0,sQuery(id+"F0.wireOp",EDGE,"E20.rect.top"),sQuery(id+"F0.wireOp",EDGE,"E23.top"),sQuery(id+"F0.wireOp",EDGE,"E23.left"),sQuery(id+"F0.wireOp",EDGE,"E23.right"),sQuery(id+"F0.wireOp",EDGE,"E24.top"),sQuery(id+"F0.wireOp",EDGE,"E24.left"),sQuery(id+"F0.wireOp",EDGE,"E24.right"),sQuery(id+"F0.wireOp",EDGE,"E25.top"),sQuery(id+"F0.wireOp",EDGE,"E25.left"),sQuery(id+"F0.wireOp",EDGE,"E25.right"),sQuery(id+"F0.wireOp",EDGE,"E26.top"),sQuery(id+"F0.wireOp",EDGE,"E26.left"),sQuery(id+"F0.wireOp",EDGE,"E26.right")])],"isStart":false})]});}
            var Q101;
            {var subQ0=sQuery(id+"F0.wireOp",EDGE,"E20.rect.bottom");Q101=makeQuery(id+"F1.opExtrude","CAP_EDGE",EDGE,{"disambiguationData":[OSD([subQ0]),TDD([makeQuery(id+"F0.imprint","IMPRINT",EDGE,{"disambiguationData":[TD([[makeQuery(id+"F0.imprint","INTERSECT",VERTEX,{"derivedFrom":[sQuery(id+"F0.wireOp",EDGE,"E8"),subQ0]}),1.0]])],"derivedFrom":subQ0})])],"isStart":false});}
            var Q102;
            {var subQ0=sQuery(id+"F0.wireOp",EDGE,"E20.rect.bottom");var subQ1=sQuery(id+"F0.wireOp",EDGE,"E17.rect.right");Q102=makeQuery(id+"F3.opFillet","BLEND_EDGE",EDGE,{"blendedFrom":[makeQuery(id+"F1.opExtrude","SWEPT_EDGE",EDGE,{"disambiguationData":[OSD([subQ1,subQ0])]}),makeQuery(id+"F1.opExtrude","CAP_FACE",FACE,{"disambiguationData":[OSD([sQuery(id+"F0.wireOp",EDGE,"E0"),sQuery(id+"F0.wireOp",EDGE,"E1"),sQuery(id+"F0.wireOp",EDGE,"E2"),sQuery(id+"F0.wireOp",EDGE,"E3"),sQuery(id+"F0.wireOp",EDGE,"E4"),sQuery(id+"F0.wireOp",EDGE,"E5"),sQuery(id+"F0.wireOp",EDGE,"E6"),sQuery(id+"F0.wireOp",EDGE,"E7"),sQuery(id+"F0.wireOp",EDGE,"E8"),sQuery(id+"F0.wireOp",EDGE,"E9"),sQuery(id+"F0.wireOp",EDGE,"E10"),sQuery(id+"F0.wireOp",EDGE,"E11"),sQuery(id+"F0.wireOp",EDGE,"E12"),sQuery(id+"F0.wireOp",EDGE,"E13"),sQuery(id+"F0.wireOp",EDGE,"E14"),sQuery(id+"F0.wireOp",EDGE,"E15"),sQuery(id+"F0.wireOp",EDGE,"E17.rect.bottom"),sQuery(id+"F0.wireOp",EDGE,"E17.rect.top"),sQuery(id+"F0.wireOp",EDGE,"E17.rect.left"),subQ1,sQuery(id+"F0.wireOp",EDGE,"E18.rect.bottom"),sQuery(id+"F0.wireOp",EDGE,"E18.rect.top"),sQuery(id+"F0.wireOp",EDGE,"E18.rect.left"),sQuery(id+"F0.wireOp",EDGE,"E18.rect.right"),sQuery(id+"F0.wireOp",EDGE,"E19.rect.left"),sQuery(id+"F0.wireOp",EDGE,"E19.rect.right"),subQ0,sQuery(id+"F0.wireOp",EDGE,"E20.rect.top"),sQuery(id+"F0.wireOp",EDGE,"E23.top"),sQuery(id+"F0.wireOp",EDGE,"E23.left"),sQuery(id+"F0.wireOp",EDGE,"E23.right"),sQuery(id+"F0.wireOp",EDGE,"E24.top"),sQuery(id+"F0.wireOp",EDGE,"E24.left"),sQuery(id+"F0.wireOp",EDGE,"E24.right"),sQuery(id+"F0.wireOp",EDGE,"E25.top"),sQuery(id+"F0.wireOp",EDGE,"E25.left"),sQuery(id+"F0.wireOp",EDGE,"E25.right"),sQuery(id+"F0.wireOp",EDGE,"E26.top"),sQuery(id+"F0.wireOp",EDGE,"E26.left"),sQuery(id+"F0.wireOp",EDGE,"E26.right")])],"isStart":false})],"blendedInto":[makeQuery(id+"F1.opExtrude","CAP_FACE",FACE,{"disambiguationData":[OSD([sQuery(id+"F0.wireOp",EDGE,"E0"),sQuery(id+"F0.wireOp",EDGE,"E1"),sQuery(id+"F0.wireOp",EDGE,"E2"),sQuery(id+"F0.wireOp",EDGE,"E3"),sQuery(id+"F0.wireOp",EDGE,"E4"),sQuery(id+"F0.wireOp",EDGE,"E5"),sQuery(id+"F0.wireOp",EDGE,"E6"),sQuery(id+"F0.wireOp",EDGE,"E7"),sQuery(id+"F0.wireOp",EDGE,"E8"),sQuery(id+"F0.wireOp",EDGE,"E9"),sQuery(id+"F0.wireOp",EDGE,"E10"),sQuery(id+"F0.wireOp",EDGE,"E11"),sQuery(id+"F0.wireOp",EDGE,"E12"),sQuery(id+"F0.wireOp",EDGE,"E13"),sQuery(id+"F0.wireOp",EDGE,"E14"),sQuery(id+"F0.wireOp",EDGE,"E15"),sQuery(id+"F0.wireOp",EDGE,"E17.rect.bottom"),sQuery(id+"F0.wireOp",EDGE,"E17.rect.top"),sQuery(id+"F0.wireOp",EDGE,"E17.rect.left"),subQ1,sQuery(id+"F0.wireOp",EDGE,"E18.rect.bottom"),sQuery(id+"F0.wireOp",EDGE,"E18.rect.top"),sQuery(id+"F0.wireOp",EDGE,"E18.rect.left"),sQuery(id+"F0.wireOp",EDGE,"E18.rect.right"),sQuery(id+"F0.wireOp",EDGE,"E19.rect.left"),sQuery(id+"F0.wireOp",EDGE,"E19.rect.right"),subQ0,sQuery(id+"F0.wireOp",EDGE,"E20.rect.top"),sQuery(id+"F0.wireOp",EDGE,"E23.top"),sQuery(id+"F0.wireOp",EDGE,"E23.left"),sQuery(id+"F0.wireOp",EDGE,"E23.right"),sQuery(id+"F0.wireOp",EDGE,"E24.top"),sQuery(id+"F0.wireOp",EDGE,"E24.left"),sQuery(id+"F0.wireOp",EDGE,"E24.right"),sQuery(id+"F0.wireOp",EDGE,"E25.top"),sQuery(id+"F0.wireOp",EDGE,"E25.left"),sQuery(id+"F0.wireOp",EDGE,"E25.right"),sQuery(id+"F0.wireOp",EDGE,"E26.top"),sQuery(id+"F0.wireOp",EDGE,"E26.left"),sQuery(id+"F0.wireOp",EDGE,"E26.right")])],"isStart":false})]});}
            var Q103;
            Q103=makeQuery(id+"F1.opExtrude","CAP_EDGE",EDGE,{"disambiguationData":[OSD([sQuery(id+"F0.wireOp",EDGE,"E17.rect.right"),sQuery(id+"F0.wireOp",EDGE,"E23.left")])],"isStart":false});
            fillet(context, id + "F4", {"entities" : qUnion([Q0, Q1, Q2, Q3, Q4, Q5, Q6, Q7, Q8, Q9, Q10, Q11, Q12, Q13, Q14, Q15, Q16, Q17, Q18, Q19, Q20, Q21, Q22, Q23, Q24, Q25, Q26, Q27, Q28, Q29, Q30, Q31, Q32, Q33, Q34, Q35, Q36, Q37, Q38, Q39, Q40, Q41, Q42, Q43, Q44, Q45, Q46, Q47, Q48, Q49, Q50, Q51, Q52, Q53, Q54, Q55, Q56, Q57, Q58, Q59, Q60, Q61, Q62, Q63, Q64, Q65, Q66, Q67, Q68, Q69, Q70, Q71, Q72, Q73, Q74, Q75, Q76, Q77, Q78, Q79, Q80, Q81, Q82, Q83, Q84, Q85, Q86, Q87, Q88, Q89, Q90, Q91, Q92, Q93, Q94, Q95, Q96, Q97, Q98, Q99, Q100, Q101, Q102, Q103]), "radius" : 0.76 * mm, "allowEdgeOverflow" : false});
        }
        {
            var Q0;
            Q0=makeQuery(id+"F1.opExtrude","CAP_EDGE",EDGE,{"disambiguationData":[OSD([sQuery(id+"F0.wireOp",EDGE,"E27.rect.right")])],"isStart":true});
            var Q1;
            Q1=makeQuery(id+"F1.opExtrude","CAP_EDGE",EDGE,{"disambiguationData":[OSD([sQuery(id+"F0.wireOp",EDGE,"E27.rect.bottom")])],"isStart":true});
            var Q2;
            Q2=makeQuery(id+"F1.opExtrude","CAP_EDGE",EDGE,{"disambiguationData":[OSD([sQuery(id+"F0.wireOp",EDGE,"E27.rect.left")])],"isStart":true});
            var Q3;
            {var subQ0=sQuery(id+"F0.wireOp",EDGE,"E27.rect.top");Q3=makeQuery(id+"F1.opExtrude","CAP_EDGE",EDGE,{"disambiguationData":[OSD([subQ0]),TDD([makeQuery(id+"F0.imprint","IMPRINT",EDGE,{"disambiguationData":[TD([[makeQuery(id+"F0.imprint","INTERSECT",VERTEX,{"derivedFrom":[subQ0,sQuery(id+"F0.wireOp",EDGE,"E27.rect.left")]}),-1.0]])],"derivedFrom":subQ0})])],"isStart":true});}
            var Q4;
            {var subQ0=sQuery(id+"F0.wireOp",EDGE,"E27.rect.top");Q4=makeQuery(id+"F1.opExtrude","CAP_EDGE",EDGE,{"disambiguationData":[OSD([subQ0]),TDD([makeQuery(id+"F0.imprint","IMPRINT",EDGE,{"disambiguationData":[TD([[makeQuery(id+"F0.imprint","INTERSECT",VERTEX,{"derivedFrom":[subQ0,sQuery(id+"F0.wireOp",EDGE,"E27.rect.right")]}),1.0]])],"derivedFrom":subQ0})])],"isStart":true});}
            var Q5;
            Q5=makeQuery(id+"F1.opExtrude","SWEPT_EDGE",EDGE,{"disambiguationData":[OSD([sQuery(id+"F0.wireOp",EDGE,"E27.rect.bottom"),sQuery(id+"F0.wireOp",EDGE,"E27.rect.right")])]});
            var Q6;
            Q6=makeQuery(id+"F1.opExtrude","SWEPT_EDGE",EDGE,{"disambiguationData":[OSD([sQuery(id+"F0.wireOp",EDGE,"E27.rect.top"),sQuery(id+"F0.wireOp",EDGE,"E27.rect.right")])]});
            var Q7;
            Q7=makeQuery(id+"F1.opExtrude","CAP_EDGE",EDGE,{"disambiguationData":[OSD([sQuery(id+"F0.wireOp",EDGE,"E27.rect.right")])],"isStart":false});
            var Q8;
            Q8=makeQuery(id+"F1.opExtrude","CAP_EDGE",EDGE,{"disambiguationData":[OSD([sQuery(id+"F0.wireOp",EDGE,"E27.rect.bottom")])],"isStart":false});
            var Q9;
            Q9=makeQuery(id+"F1.opExtrude","SWEPT_EDGE",EDGE,{"disambiguationData":[OSD([sQuery(id+"F0.wireOp",EDGE,"E27.rect.bottom"),sQuery(id+"F0.wireOp",EDGE,"E27.rect.left")])]});
            var Q10;
            Q10=makeQuery(id+"F1.opExtrude","CAP_EDGE",EDGE,{"disambiguationData":[OSD([sQuery(id+"F0.wireOp",EDGE,"E27.rect.left")])],"isStart":false});
            var Q11;
            {var subQ0=sQuery(id+"F0.wireOp",EDGE,"E27.rect.top");Q11=makeQuery(id+"F1.opExtrude","CAP_EDGE",EDGE,{"disambiguationData":[OSD([subQ0]),TDD([makeQuery(id+"F0.imprint","IMPRINT",EDGE,{"disambiguationData":[TD([[makeQuery(id+"F0.imprint","INTERSECT",VERTEX,{"derivedFrom":[subQ0,sQuery(id+"F0.wireOp",EDGE,"E27.rect.left")]}),-1.0]])],"derivedFrom":subQ0})])],"isStart":false});}
            var Q12;
            {var subQ0=sQuery(id+"F0.wireOp",EDGE,"E27.rect.top");Q12=makeQuery(id+"F1.opExtrude","CAP_EDGE",EDGE,{"disambiguationData":[OSD([subQ0]),TDD([makeQuery(id+"F0.imprint","IMPRINT",EDGE,{"disambiguationData":[TD([[makeQuery(id+"F0.imprint","INTERSECT",VERTEX,{"derivedFrom":[subQ0,sQuery(id+"F0.wireOp",EDGE,"E27.rect.right")]}),1.0]])],"derivedFrom":subQ0})])],"isStart":false});}
            var Q13;
            Q13=makeQuery(id+"F1.opExtrude","SWEPT_EDGE",EDGE,{"disambiguationData":[OSD([sQuery(id+"F0.wireOp",EDGE,"E27.rect.top"),sQuery(id+"F0.wireOp",EDGE,"E27.rect.left")])]});
            var Q14;
            Q14=makeQuery(id+"F1.opExtrude","SWEPT_EDGE",EDGE,{"disambiguationData":[OSD([sQuery(id+"F0.wireOp",EDGE,"E30.rect.bottom"),sQuery(id+"F0.wireOp",EDGE,"E30.rect.right")])]});
            var Q15;
            Q15=makeQuery(id+"F1.opExtrude","CAP_EDGE",EDGE,{"disambiguationData":[OSD([sQuery(id+"F0.wireOp",EDGE,"E30.rect.bottom")])],"isStart":false});
            var Q16;
            Q16=makeQuery(id+"F1.opExtrude","SWEPT_EDGE",EDGE,{"disambiguationData":[OSD([sQuery(id+"F0.wireOp",EDGE,"E30.rect.bottom"),sQuery(id+"F0.wireOp",EDGE,"E30.rect.left")])]});
            var Q17;
            Q17=makeQuery(id+"F1.opExtrude","CAP_EDGE",EDGE,{"disambiguationData":[OSD([sQuery(id+"F0.wireOp",EDGE,"E30.rect.bottom")])],"isStart":true});
            var Q18;
            Q18=makeQuery(id+"F1.opExtrude","CAP_EDGE",EDGE,{"disambiguationData":[OSD([sQuery(id+"F0.wireOp",EDGE,"E30.rect.right")])],"isStart":false});
            var Q19;
            Q19=makeQuery(id+"F1.opExtrude","CAP_EDGE",EDGE,{"disambiguationData":[OSD([sQuery(id+"F0.wireOp",EDGE,"E30.rect.left")])],"isStart":false});
            var Q20;
            Q20=makeQuery(id+"F1.opExtrude","CAP_EDGE",EDGE,{"disambiguationData":[OSD([sQuery(id+"F0.wireOp",EDGE,"E30.rect.right")])],"isStart":true});
            var Q21;
            Q21=makeQuery(id+"F1.opExtrude","CAP_EDGE",EDGE,{"disambiguationData":[OSD([sQuery(id+"F0.wireOp",EDGE,"E30.rect.left")])],"isStart":true});
            var Q22;
            {var subQ0=sQuery(id+"F0.wireOp",EDGE,"E30.rect.top");Q22=makeQuery(id+"F1.opExtrude","CAP_EDGE",EDGE,{"disambiguationData":[OSD([subQ0]),TDD([makeQuery(id+"F0.imprint","IMPRINT",EDGE,{"disambiguationData":[TD([[makeQuery(id+"F0.imprint","INTERSECT",VERTEX,{"derivedFrom":[subQ0,sQuery(id+"F0.wireOp",EDGE,"E30.rect.right")]}),1.0]])],"derivedFrom":subQ0})])],"isStart":false});}
            var Q23;
            Q23=makeQuery(id+"F1.opExtrude","SWEPT_EDGE",EDGE,{"disambiguationData":[OSD([sQuery(id+"F0.wireOp",EDGE,"E30.rect.top"),sQuery(id+"F0.wireOp",EDGE,"E30.rect.right")])]});
            var Q24;
            {var subQ0=sQuery(id+"F0.wireOp",EDGE,"E30.rect.top");Q24=makeQuery(id+"F1.opExtrude","CAP_EDGE",EDGE,{"disambiguationData":[OSD([subQ0]),TDD([makeQuery(id+"F0.imprint","IMPRINT",EDGE,{"disambiguationData":[TD([[makeQuery(id+"F0.imprint","INTERSECT",VERTEX,{"derivedFrom":[subQ0,sQuery(id+"F0.wireOp",EDGE,"E30.rect.left")]}),-1.0]])],"derivedFrom":subQ0})])],"isStart":false});}
            var Q25;
            Q25=makeQuery(id+"F1.opExtrude","SWEPT_EDGE",EDGE,{"disambiguationData":[OSD([sQuery(id+"F0.wireOp",EDGE,"E30.rect.top"),sQuery(id+"F0.wireOp",EDGE,"E30.rect.left")])]});
            var Q26;
            {var subQ0=sQuery(id+"F0.wireOp",EDGE,"E30.rect.top");Q26=makeQuery(id+"F1.opExtrude","CAP_EDGE",EDGE,{"disambiguationData":[OSD([subQ0]),TDD([makeQuery(id+"F0.imprint","IMPRINT",EDGE,{"disambiguationData":[TD([[makeQuery(id+"F0.imprint","INTERSECT",VERTEX,{"derivedFrom":[subQ0,sQuery(id+"F0.wireOp",EDGE,"E30.rect.left")]}),-1.0]])],"derivedFrom":subQ0})])],"isStart":true});}
            var Q27;
            {var subQ0=sQuery(id+"F0.wireOp",EDGE,"E30.rect.top");Q27=makeQuery(id+"F1.opExtrude","CAP_EDGE",EDGE,{"disambiguationData":[OSD([subQ0]),TDD([makeQuery(id+"F0.imprint","IMPRINT",EDGE,{"disambiguationData":[TD([[makeQuery(id+"F0.imprint","INTERSECT",VERTEX,{"derivedFrom":[subQ0,sQuery(id+"F0.wireOp",EDGE,"E30.rect.right")]}),1.0]])],"derivedFrom":subQ0})])],"isStart":true});}
            var Q28;
            Q28=makeQuery(id+"F1.opExtrude","CAP_EDGE",EDGE,{"disambiguationData":[OSD([sQuery(id+"F0.wireOp",EDGE,"E28.rect.bottom")])],"isStart":true});
            var Q29;
            Q29=makeQuery(id+"F1.opExtrude","CAP_EDGE",EDGE,{"disambiguationData":[OSD([sQuery(id+"F0.wireOp",EDGE,"E28.rect.right")])],"isStart":true});
            var Q30;
            Q30=makeQuery(id+"F1.opExtrude","CAP_EDGE",EDGE,{"disambiguationData":[OSD([sQuery(id+"F0.wireOp",EDGE,"E28.rect.left")])],"isStart":true});
            var Q31;
            Q31=makeQuery(id+"F1.opExtrude","SWEPT_EDGE",EDGE,{"disambiguationData":[OSD([sQuery(id+"F0.wireOp",EDGE,"E28.rect.bottom"),sQuery(id+"F0.wireOp",EDGE,"E28.rect.left")])]});
            var Q32;
            Q32=makeQuery(id+"F1.opExtrude","SWEPT_EDGE",EDGE,{"disambiguationData":[OSD([sQuery(id+"F0.wireOp",EDGE,"E28.rect.bottom"),sQuery(id+"F0.wireOp",EDGE,"E28.rect.right")])]});
            var Q33;
            Q33=makeQuery(id+"F1.opExtrude","CAP_EDGE",EDGE,{"disambiguationData":[OSD([sQuery(id+"F0.wireOp",EDGE,"E28.rect.bottom")])],"isStart":false});
            var Q34;
            Q34=makeQuery(id+"F1.opExtrude","CAP_EDGE",EDGE,{"disambiguationData":[OSD([sQuery(id+"F0.wireOp",EDGE,"E28.rect.left")])],"isStart":false});
            var Q35;
            Q35=makeQuery(id+"F1.opExtrude","CAP_EDGE",EDGE,{"disambiguationData":[OSD([sQuery(id+"F0.wireOp",EDGE,"E28.rect.right")])],"isStart":false});
            var Q36;
            Q36=makeQuery(id+"F1.opExtrude","SWEPT_EDGE",EDGE,{"disambiguationData":[OSD([sQuery(id+"F0.wireOp",EDGE,"E28.rect.top"),sQuery(id+"F0.wireOp",EDGE,"E28.rect.left")])]});
            var Q37;
            {var subQ0=sQuery(id+"F0.wireOp",EDGE,"E28.rect.top");Q37=makeQuery(id+"F1.opExtrude","CAP_EDGE",EDGE,{"disambiguationData":[OSD([subQ0]),TDD([makeQuery(id+"F0.imprint","IMPRINT",EDGE,{"disambiguationData":[TD([[makeQuery(id+"F0.imprint","INTERSECT",VERTEX,{"derivedFrom":[subQ0,sQuery(id+"F0.wireOp",EDGE,"E28.rect.left")]}),-1.0]])],"derivedFrom":subQ0})])],"isStart":false});}
            var Q38;
            {var subQ0=sQuery(id+"F0.wireOp",EDGE,"E28.rect.top");Q38=makeQuery(id+"F1.opExtrude","CAP_EDGE",EDGE,{"disambiguationData":[OSD([subQ0]),TDD([makeQuery(id+"F0.imprint","IMPRINT",EDGE,{"disambiguationData":[TD([[makeQuery(id+"F0.imprint","INTERSECT",VERTEX,{"derivedFrom":[subQ0,sQuery(id+"F0.wireOp",EDGE,"E28.rect.right")]}),1.0]])],"derivedFrom":subQ0})])],"isStart":false});}
            var Q39;
            Q39=makeQuery(id+"F1.opExtrude","SWEPT_EDGE",EDGE,{"disambiguationData":[OSD([sQuery(id+"F0.wireOp",EDGE,"E28.rect.top"),sQuery(id+"F0.wireOp",EDGE,"E28.rect.right")])]});
            var Q40;
            {var subQ0=sQuery(id+"F0.wireOp",EDGE,"E28.rect.top");Q40=makeQuery(id+"F1.opExtrude","CAP_EDGE",EDGE,{"disambiguationData":[OSD([subQ0]),TDD([makeQuery(id+"F0.imprint","IMPRINT",EDGE,{"disambiguationData":[TD([[makeQuery(id+"F0.imprint","INTERSECT",VERTEX,{"derivedFrom":[subQ0,sQuery(id+"F0.wireOp",EDGE,"E28.rect.left")]}),-1.0]])],"derivedFrom":subQ0})])],"isStart":true});}
            var Q41;
            {var subQ0=sQuery(id+"F0.wireOp",EDGE,"E28.rect.top");Q41=makeQuery(id+"F1.opExtrude","CAP_EDGE",EDGE,{"disambiguationData":[OSD([subQ0]),TDD([makeQuery(id+"F0.imprint","IMPRINT",EDGE,{"disambiguationData":[TD([[makeQuery(id+"F0.imprint","INTERSECT",VERTEX,{"derivedFrom":[subQ0,sQuery(id+"F0.wireOp",EDGE,"E28.rect.right")]}),1.0]])],"derivedFrom":subQ0})])],"isStart":true});}
            var Q42;
            Q42=makeQuery(id+"F1.opExtrude","CAP_EDGE",EDGE,{"disambiguationData":[OSD([sQuery(id+"F0.wireOp",EDGE,"E29.rect.top")])],"isStart":true});
            var Q43;
            Q43=makeQuery(id+"F1.opExtrude","CAP_EDGE",EDGE,{"disambiguationData":[OSD([sQuery(id+"F0.wireOp",EDGE,"E29.rect.left")])],"isStart":true});
            var Q44;
            {var subQ0=sQuery(id+"F0.wireOp",EDGE,"E29.rect.bottom");Q44=makeQuery(id+"F1.opExtrude","CAP_EDGE",EDGE,{"disambiguationData":[OSD([subQ0]),TDD([makeQuery(id+"F0.imprint","IMPRINT",EDGE,{"disambiguationData":[TD([[makeQuery(id+"F0.imprint","INTERSECT",VERTEX,{"derivedFrom":[subQ0,sQuery(id+"F0.wireOp",EDGE,"E29.rect.left")]}),-1.0]])],"derivedFrom":subQ0})])],"isStart":true});}
            var Q45;
            {var subQ0=sQuery(id+"F0.wireOp",EDGE,"E29.rect.bottom");Q45=makeQuery(id+"F1.opExtrude","CAP_EDGE",EDGE,{"disambiguationData":[OSD([subQ0]),TDD([makeQuery(id+"F0.imprint","IMPRINT",EDGE,{"disambiguationData":[TD([[makeQuery(id+"F0.imprint","INTERSECT",VERTEX,{"derivedFrom":[subQ0,sQuery(id+"F0.wireOp",EDGE,"E29.rect.right")]}),1.0]])],"derivedFrom":subQ0})])],"isStart":true});}
            var Q46;
            Q46=makeQuery(id+"F1.opExtrude","CAP_EDGE",EDGE,{"disambiguationData":[OSD([sQuery(id+"F0.wireOp",EDGE,"E29.rect.right")])],"isStart":true});
            var Q47;
            Q47=makeQuery(id+"F1.opExtrude","SWEPT_EDGE",EDGE,{"disambiguationData":[OSD([sQuery(id+"F0.wireOp",EDGE,"E29.rect.top"),sQuery(id+"F0.wireOp",EDGE,"E29.rect.left")])]});
            var Q48;
            Q48=makeQuery(id+"F1.opExtrude","SWEPT_EDGE",EDGE,{"disambiguationData":[OSD([sQuery(id+"F0.wireOp",EDGE,"E29.rect.top"),sQuery(id+"F0.wireOp",EDGE,"E29.rect.right")])]});
            var Q49;
            Q49=makeQuery(id+"F1.opExtrude","CAP_EDGE",EDGE,{"disambiguationData":[OSD([sQuery(id+"F0.wireOp",EDGE,"E29.rect.top")])],"isStart":false});
            var Q50;
            Q50=makeQuery(id+"F1.opExtrude","SWEPT_EDGE",EDGE,{"disambiguationData":[OSD([sQuery(id+"F0.wireOp",EDGE,"E29.rect.bottom"),sQuery(id+"F0.wireOp",EDGE,"E29.rect.left")])]});
            var Q51;
            Q51=makeQuery(id+"F1.opExtrude","SWEPT_EDGE",EDGE,{"disambiguationData":[OSD([sQuery(id+"F0.wireOp",EDGE,"E29.rect.bottom"),sQuery(id+"F0.wireOp",EDGE,"E29.rect.right")])]});
            var Q52;
            Q52=makeQuery(id+"F1.opExtrude","CAP_EDGE",EDGE,{"disambiguationData":[OSD([sQuery(id+"F0.wireOp",EDGE,"E29.rect.right")])],"isStart":false});
            var Q53;
            {var subQ0=sQuery(id+"F0.wireOp",EDGE,"E29.rect.bottom");Q53=makeQuery(id+"F1.opExtrude","CAP_EDGE",EDGE,{"disambiguationData":[OSD([subQ0]),TDD([makeQuery(id+"F0.imprint","IMPRINT",EDGE,{"disambiguationData":[TD([[makeQuery(id+"F0.imprint","INTERSECT",VERTEX,{"derivedFrom":[subQ0,sQuery(id+"F0.wireOp",EDGE,"E29.rect.right")]}),1.0]])],"derivedFrom":subQ0})])],"isStart":false});}
            var Q54;
            {var subQ0=sQuery(id+"F0.wireOp",EDGE,"E29.rect.bottom");Q54=makeQuery(id+"F1.opExtrude","CAP_EDGE",EDGE,{"disambiguationData":[OSD([subQ0]),TDD([makeQuery(id+"F0.imprint","IMPRINT",EDGE,{"disambiguationData":[TD([[makeQuery(id+"F0.imprint","INTERSECT",VERTEX,{"derivedFrom":[subQ0,sQuery(id+"F0.wireOp",EDGE,"E29.rect.left")]}),-1.0]])],"derivedFrom":subQ0})])],"isStart":false});}
            var Q55;
            Q55=makeQuery(id+"F1.opExtrude","CAP_EDGE",EDGE,{"disambiguationData":[OSD([sQuery(id+"F0.wireOp",EDGE,"E29.rect.left")])],"isStart":false});
            fillet(context, id + "F5", {"entities" : qUnion([Q0, Q1, Q2, Q3, Q4, Q5, Q6, Q7, Q8, Q9, Q10, Q11, Q12, Q13, Q14, Q15, Q16, Q17, Q18, Q19, Q20, Q21, Q22, Q23, Q24, Q25, Q26, Q27, Q28, Q29, Q30, Q31, Q32, Q33, Q34, Q35, Q36, Q37, Q38, Q39, Q40, Q41, Q42, Q43, Q44, Q45, Q46, Q47, Q48, Q49, Q50, Q51, Q52, Q53, Q54, Q55]), "radius" : 0.64 * mm, "tangentPropagation" : true, "allowEdgeOverflow" : false});
        }
        {
            var Q0;
            Q0=makeQuery(id+"F1.opExtrude","SWEPT_EDGE",EDGE,{"disambiguationData":[OSD([sQuery(id+"F0.wireOp",EDGE,"E26.left"),sQuery(id+"F0.wireOp",EDGE,"E28.rect.top")])]});
            var Q1;
            Q1=makeQuery(id+"F1.opExtrude","SWEPT_EDGE",EDGE,{"disambiguationData":[OSD([sQuery(id+"F0.wireOp",EDGE,"E26.right"),sQuery(id+"F0.wireOp",EDGE,"E28.rect.top")])]});
            var Q2;
            Q2=makeQuery(id+"F1.opExtrude","SWEPT_EDGE",EDGE,{"disambiguationData":[OSD([sQuery(id+"F0.wireOp",EDGE,"E23.left"),sQuery(id+"F0.wireOp",EDGE,"E27.rect.top")])]});
            var Q3;
            Q3=makeQuery(id+"F1.opExtrude","SWEPT_EDGE",EDGE,{"disambiguationData":[OSD([sQuery(id+"F0.wireOp",EDGE,"E23.right"),sQuery(id+"F0.wireOp",EDGE,"E27.rect.top")])]});
            var Q4;
            Q4=makeQuery(id+"F1.opExtrude","SWEPT_EDGE",EDGE,{"disambiguationData":[OSD([sQuery(id+"F0.wireOp",EDGE,"E25.left"),sQuery(id+"F0.wireOp",EDGE,"E29.rect.bottom")])]});
            var Q5;
            Q5=makeQuery(id+"F1.opExtrude","SWEPT_EDGE",EDGE,{"disambiguationData":[OSD([sQuery(id+"F0.wireOp",EDGE,"E24.right"),sQuery(id+"F0.wireOp",EDGE,"E30.rect.top")])]});
            var Q6;
            Q6=makeQuery(id+"F1.opExtrude","SWEPT_EDGE",EDGE,{"disambiguationData":[OSD([sQuery(id+"F0.wireOp",EDGE,"E24.left"),sQuery(id+"F0.wireOp",EDGE,"E30.rect.top")])]});
            var Q7;
            Q7=makeQuery(id+"F1.opExtrude","SWEPT_EDGE",EDGE,{"disambiguationData":[OSD([sQuery(id+"F0.wireOp",EDGE,"E25.right"),sQuery(id+"F0.wireOp",EDGE,"E29.rect.bottom")])]});
            fillet(context, id + "F6", {"entities" : qUnion([Q0, Q1, Q2, Q3, Q4, Q5, Q6, Q7]), "radius" : 0.5 * mm, "tangentPropagation" : true, "allowEdgeOverflow" : false});
        }
    });
